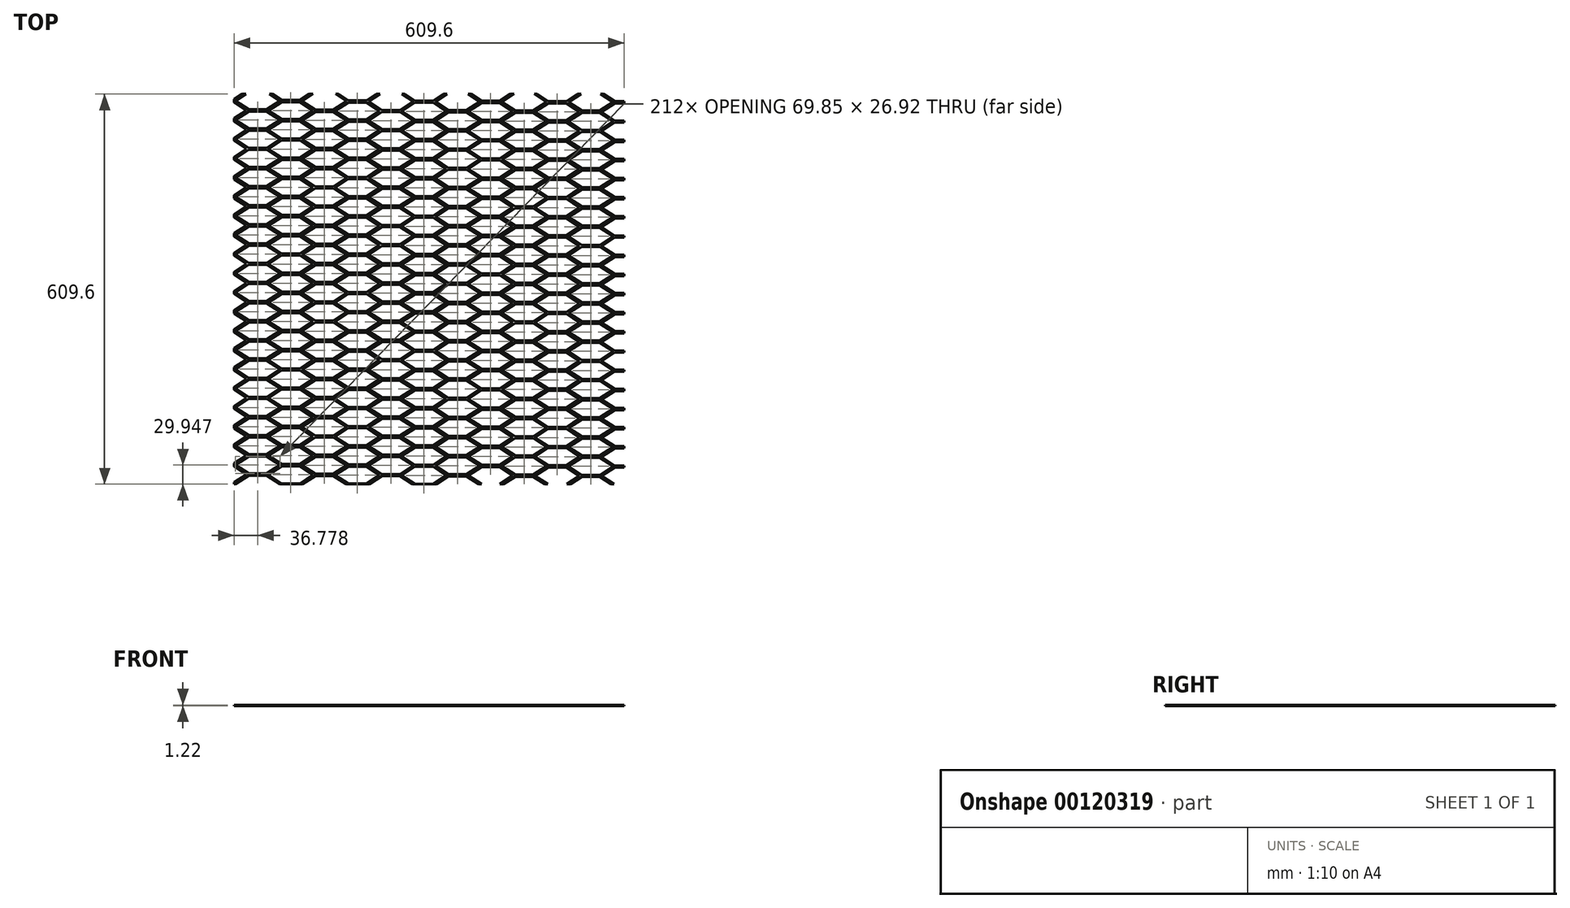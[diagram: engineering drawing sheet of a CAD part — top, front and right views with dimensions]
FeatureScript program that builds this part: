
annotation { "Feature Type Name" : "Feature", "Feature Type Description" : "" }
export const myFeature = defineFeature(function(context is Context, id is Id, definition is map)
    precondition{}
    {
        {
            var Q0;
            Q0=qCreatedBy(makeId("Top.planeOp"),FACE);
            var sketch = newSketch(context, id + "F0", { "sketchPlane" : qUnion([Q0])});
            skLineSegment(sketch, "E0", {"start": v(1.85, 0) * mm, "end": v(22.6, 13.46) * mm});
            skLineSegment(sketch, "E1", {"start": v(22.6, 13.46) * mm, "end": v(50.96, 13.46) * mm});
            skLineSegment(sketch, "E2", {"start": v(50.96, 13.46) * mm, "end": v(71.7, 0) * mm});
            skLineSegment(sketch, "E3", {"start": v(71.7, 0) * mm, "end": v(50.96, -13.46) * mm});
            skLineSegment(sketch, "E4", {"start": v(50.96, -13.46) * mm, "end": v(22.6, -13.46) * mm});
            skLineSegment(sketch, "E5", {"start": v(22.6, -13.46) * mm, "end": v(1.85, 0) * mm});
            skLineSegment(sketch, "E6.0", {"start": v(19.33, -14.95) * mm, "end": v(-1.41, -1.49) * mm});
            skLineSegment(sketch, "E7", {"start": v(-1.41, -1.49) * mm, "end": v(-29.78, -1.49) * mm});
            skLineSegment(sketch, "E8", {"start": v(-29.78, -1.49) * mm, "end": v(-50.52, -14.95) * mm});
            skLineSegment(sketch, "E9", {"start": v(-50.52, -14.95) * mm, "end": v(-29.78, -28.4) * mm});
            skLineSegment(sketch, "E10", {"start": v(-29.78, -28.4) * mm, "end": v(-1.41, -28.4) * mm});
            skLineSegment(sketch, "E11", {"start": v(-1.41, -28.4) * mm, "end": v(19.33, -14.95) * mm});
            skLineSegment(sketch, "E12.0.1.0", {"start": v(1.85, 29.95) * mm, "end": v(22.6, 43.4) * mm});
            skLineSegment(sketch, "E12.0.1.1", {"start": v(22.6, 43.4) * mm, "end": v(50.96, 43.4) * mm});
            skLineSegment(sketch, "E12.0.1.2", {"start": v(50.96, 43.4) * mm, "end": v(71.7, 29.95) * mm});
            skLineSegment(sketch, "E12.0.1.3", {"start": v(22.6, 16.48) * mm, "end": v(1.85, 29.95) * mm});
            skLineSegment(sketch, "E12.0.1.4", {"start": v(71.7, 29.95) * mm, "end": v(50.96, 16.48) * mm});
            skLineSegment(sketch, "E12.0.1.5", {"start": v(19.33, 15) * mm, "end": v(-1.41, 28.46) * mm});
            skLineSegment(sketch, "E12.0.1.6", {"start": v(50.96, 16.48) * mm, "end": v(22.6, 16.48) * mm});
            skLineSegment(sketch, "E12.0.1.7", {"start": v(-1.41, 28.46) * mm, "end": v(-29.78, 28.46) * mm});
            skLineSegment(sketch, "E12.0.1.8", {"start": v(-29.78, 28.46) * mm, "end": v(-50.52, 15) * mm});
            skLineSegment(sketch, "E12.0.1.9", {"start": v(-50.52, 15) * mm, "end": v(-29.78, 1.54) * mm});
            skLineSegment(sketch, "E12.0.1.10", {"start": v(-29.78, 1.54) * mm, "end": v(-1.41, 1.54) * mm});
            skLineSegment(sketch, "E12.0.1.11", {"start": v(-1.41, 1.54) * mm, "end": v(19.33, 15) * mm});
            skLineSegment(sketch, "E12.1.0.0", {"start": v(105.98, -0.4) * mm, "end": v(126.72, 13.06) * mm});
            skLineSegment(sketch, "E12.1.0.1", {"start": v(126.72, 13.06) * mm, "end": v(155.1, 13.06) * mm});
            skLineSegment(sketch, "E12.1.0.2", {"start": v(155.1, 13.06) * mm, "end": v(175.83, -0.4) * mm});
            skLineSegment(sketch, "E12.1.0.3", {"start": v(126.72, -13.87) * mm, "end": v(105.98, -0.4) * mm});
            skLineSegment(sketch, "E12.1.0.4", {"start": v(175.83, -0.4) * mm, "end": v(155.1, -13.87) * mm});
            skLineSegment(sketch, "E12.1.0.5", {"start": v(123.46, -15.35) * mm, "end": v(102.72, -1.89) * mm});
            skLineSegment(sketch, "E12.1.0.6", {"start": v(155.1, -13.87) * mm, "end": v(126.72, -13.87) * mm});
            skLineSegment(sketch, "E12.1.0.7", {"start": v(102.72, -1.89) * mm, "end": v(74.34, -1.89) * mm});
            skLineSegment(sketch, "E12.1.0.8", {"start": v(74.34, -1.89) * mm, "end": v(53.6, -15.35) * mm});
            skLineSegment(sketch, "E12.1.0.9", {"start": v(53.6, -15.35) * mm, "end": v(74.34, -28.81) * mm});
            skLineSegment(sketch, "E12.1.0.10", {"start": v(74.34, -28.81) * mm, "end": v(102.72, -28.81) * mm});
            skLineSegment(sketch, "E12.1.0.11", {"start": v(102.72, -28.81) * mm, "end": v(123.46, -15.35) * mm});
            skLineSegment(sketch, "E12.1.1.0", {"start": v(105.98, 29.54) * mm, "end": v(126.72, 43) * mm});
            skLineSegment(sketch, "E12.1.1.1", {"start": v(126.72, 43) * mm, "end": v(155.1, 43) * mm});
            skLineSegment(sketch, "E12.1.1.2", {"start": v(155.1, 43) * mm, "end": v(175.83, 29.54) * mm});
            skLineSegment(sketch, "E12.1.1.3", {"start": v(126.72, 16.08) * mm, "end": v(105.98, 29.54) * mm});
            skLineSegment(sketch, "E12.1.1.4", {"start": v(175.83, 29.54) * mm, "end": v(155.1, 16.08) * mm});
            skLineSegment(sketch, "E12.1.1.5", {"start": v(123.46, 14.6) * mm, "end": v(102.72, 28.06) * mm});
            skLineSegment(sketch, "E12.1.1.6", {"start": v(155.1, 16.08) * mm, "end": v(126.72, 16.08) * mm});
            skLineSegment(sketch, "E12.1.1.7", {"start": v(102.72, 28.06) * mm, "end": v(74.34, 28.06) * mm});
            skLineSegment(sketch, "E12.1.1.8", {"start": v(74.34, 28.06) * mm, "end": v(53.6, 14.6) * mm});
            skLineSegment(sketch, "E12.1.1.9", {"start": v(53.6, 14.6) * mm, "end": v(74.34, 1.13) * mm});
            skLineSegment(sketch, "E12.1.1.10", {"start": v(74.34, 1.13) * mm, "end": v(102.72, 1.13) * mm});
            skLineSegment(sketch, "E12.1.1.11", {"start": v(102.72, 1.13) * mm, "end": v(123.46, 14.6) * mm});
            skLineSegment(sketch, "E12.2.0.0", {"start": v(210.1, -0.8) * mm, "end": v(230.85, 12.66) * mm});
            skLineSegment(sketch, "E12.2.0.1", {"start": v(230.85, 12.66) * mm, "end": v(259.22, 12.66) * mm});
            skLineSegment(sketch, "E12.2.0.2", {"start": v(259.22, 12.66) * mm, "end": v(279.96, -0.8) * mm});
            skLineSegment(sketch, "E12.2.0.3", {"start": v(230.85, -14.27) * mm, "end": v(210.1, -0.8) * mm});
            skLineSegment(sketch, "E12.2.0.4", {"start": v(279.96, -0.8) * mm, "end": v(259.22, -14.27) * mm});
            skLineSegment(sketch, "E12.2.0.5", {"start": v(227.58, -15.75) * mm, "end": v(206.85, -2.3) * mm});
            skLineSegment(sketch, "E12.2.0.6", {"start": v(259.22, -14.27) * mm, "end": v(230.85, -14.27) * mm});
            skLineSegment(sketch, "E12.2.0.7", {"start": v(206.85, -2.3) * mm, "end": v(178.47, -2.3) * mm});
            skLineSegment(sketch, "E12.2.0.8", {"start": v(178.47, -2.3) * mm, "end": v(157.73, -15.75) * mm});
            skLineSegment(sketch, "E12.2.0.9", {"start": v(157.73, -15.75) * mm, "end": v(178.47, -29.22) * mm});
            skLineSegment(sketch, "E12.2.0.10", {"start": v(178.47, -29.22) * mm, "end": v(206.85, -29.22) * mm});
            skLineSegment(sketch, "E12.2.0.11", {"start": v(206.85, -29.22) * mm, "end": v(227.58, -15.75) * mm});
            skLineSegment(sketch, "E12.2.1.0", {"start": v(210.1, 29.14) * mm, "end": v(230.85, 42.6) * mm});
            skLineSegment(sketch, "E12.2.1.1", {"start": v(230.85, 42.6) * mm, "end": v(259.22, 42.6) * mm});
            skLineSegment(sketch, "E12.2.1.2", {"start": v(259.22, 42.6) * mm, "end": v(279.96, 29.14) * mm});
            skLineSegment(sketch, "E12.2.1.3", {"start": v(230.85, 15.68) * mm, "end": v(210.1, 29.14) * mm});
            skLineSegment(sketch, "E12.2.1.4", {"start": v(279.96, 29.14) * mm, "end": v(259.22, 15.68) * mm});
            skLineSegment(sketch, "E12.2.1.5", {"start": v(227.58, 14.2) * mm, "end": v(206.85, 27.65) * mm});
            skLineSegment(sketch, "E12.2.1.6", {"start": v(259.22, 15.68) * mm, "end": v(230.85, 15.68) * mm});
            skLineSegment(sketch, "E12.2.1.7", {"start": v(206.85, 27.65) * mm, "end": v(178.47, 27.65) * mm});
            skLineSegment(sketch, "E12.2.1.8", {"start": v(178.47, 27.65) * mm, "end": v(157.73, 14.2) * mm});
            skLineSegment(sketch, "E12.2.1.9", {"start": v(157.73, 14.2) * mm, "end": v(178.47, 0.73) * mm});
            skLineSegment(sketch, "E12.2.1.10", {"start": v(178.47, 0.73) * mm, "end": v(206.85, 0.73) * mm});
            skLineSegment(sketch, "E12.2.1.11", {"start": v(206.85, 0.73) * mm, "end": v(227.58, 14.2) * mm});
            skLineSegment(sketch, "E12.direction1", {"start": v(-50.52, -14.95) * mm, "end": v(53.6, -15.35) * mm, "construction": true});
            skLineSegment(sketch, "E12.direction2", {"start": v(-50.52, -14.95) * mm, "end": v(-50.52, 15) * mm, "construction": true});
            skLineSegment(sketch, "E13.0.3.0", {"start": v(314.24, -1.21) * mm, "end": v(334.98, 12.25) * mm});
            skLineSegment(sketch, "E13.3.3.0", {"start": v(334.98, 12.25) * mm, "end": v(363.35, 12.25) * mm});
            skLineSegment(sketch, "E13.6.3.0", {"start": v(363.35, 12.25) * mm, "end": v(384.09, -1.21) * mm});
            skLineSegment(sketch, "E13.9.3.0", {"start": v(334.98, -14.67) * mm, "end": v(314.24, -1.21) * mm});
            skLineSegment(sketch, "E13.12.3.0", {"start": v(384.09, -1.21) * mm, "end": v(363.35, -14.67) * mm});
            skLineSegment(sketch, "E13.15.3.0", {"start": v(331.71, -16.16) * mm, "end": v(310.97, -2.7) * mm});
            skLineSegment(sketch, "E13.18.3.0", {"start": v(363.35, -14.67) * mm, "end": v(334.98, -14.67) * mm});
            skLineSegment(sketch, "E13.21.3.0", {"start": v(310.97, -2.7) * mm, "end": v(282.6, -2.7) * mm});
            skLineSegment(sketch, "E13.24.3.0", {"start": v(282.6, -2.7) * mm, "end": v(261.86, -16.16) * mm});
            skLineSegment(sketch, "E13.27.3.0", {"start": v(261.86, -16.16) * mm, "end": v(282.6, -29.62) * mm});
            skLineSegment(sketch, "E13.30.3.0", {"start": v(282.6, -29.62) * mm, "end": v(310.97, -29.62) * mm});
            skLineSegment(sketch, "E13.33.3.0", {"start": v(310.97, -29.62) * mm, "end": v(331.71, -16.16) * mm});
            skLineSegment(sketch, "E13.0.3.1", {"start": v(314.24, 28.74) * mm, "end": v(334.98, 42.2) * mm});
            skLineSegment(sketch, "E13.3.3.1", {"start": v(334.98, 42.2) * mm, "end": v(363.35, 42.2) * mm});
            skLineSegment(sketch, "E13.6.3.1", {"start": v(363.35, 42.2) * mm, "end": v(384.09, 28.74) * mm});
            skLineSegment(sketch, "E13.9.3.1", {"start": v(334.98, 15.27) * mm, "end": v(314.24, 28.74) * mm});
            skLineSegment(sketch, "E13.12.3.1", {"start": v(384.09, 28.74) * mm, "end": v(363.35, 15.27) * mm});
            skLineSegment(sketch, "E13.15.3.1", {"start": v(331.71, 13.79) * mm, "end": v(310.97, 27.25) * mm});
            skLineSegment(sketch, "E13.18.3.1", {"start": v(363.35, 15.27) * mm, "end": v(334.98, 15.27) * mm});
            skLineSegment(sketch, "E13.21.3.1", {"start": v(310.97, 27.25) * mm, "end": v(282.6, 27.25) * mm});
            skLineSegment(sketch, "E13.24.3.1", {"start": v(282.6, 27.25) * mm, "end": v(261.86, 13.79) * mm});
            skLineSegment(sketch, "E13.27.3.1", {"start": v(261.86, 13.79) * mm, "end": v(282.6, 0.33) * mm});
            skLineSegment(sketch, "E13.30.3.1", {"start": v(282.6, 0.33) * mm, "end": v(310.97, 0.33) * mm});
            skLineSegment(sketch, "E13.33.3.1", {"start": v(310.97, 0.33) * mm, "end": v(331.71, 13.79) * mm});
            skLineSegment(sketch, "E13.0.4.0", {"start": v(418.37, -1.61) * mm, "end": v(439.1, 11.85) * mm});
            skLineSegment(sketch, "E13.3.4.0", {"start": v(439.1, 11.85) * mm, "end": v(467.48, 11.85) * mm});
            skLineSegment(sketch, "E13.6.4.0", {"start": v(467.48, 11.85) * mm, "end": v(488.22, -1.61) * mm});
            skLineSegment(sketch, "E13.9.4.0", {"start": v(439.1, -15.08) * mm, "end": v(418.37, -1.61) * mm});
            skLineSegment(sketch, "E13.12.4.0", {"start": v(488.22, -1.61) * mm, "end": v(467.48, -15.08) * mm});
            skLineSegment(sketch, "E13.15.4.0", {"start": v(435.84, -16.56) * mm, "end": v(415.1, -3.1) * mm});
            skLineSegment(sketch, "E13.18.4.0", {"start": v(467.48, -15.08) * mm, "end": v(439.1, -15.08) * mm});
            skLineSegment(sketch, "E13.21.4.0", {"start": v(415.1, -3.1) * mm, "end": v(386.73, -3.1) * mm});
            skLineSegment(sketch, "E13.24.4.0", {"start": v(386.73, -3.1) * mm, "end": v(366, -16.56) * mm});
            skLineSegment(sketch, "E13.27.4.0", {"start": v(366, -16.56) * mm, "end": v(386.73, -30.02) * mm});
            skLineSegment(sketch, "E13.30.4.0", {"start": v(386.73, -30.02) * mm, "end": v(415.1, -30.02) * mm});
            skLineSegment(sketch, "E13.33.4.0", {"start": v(415.1, -30.02) * mm, "end": v(435.84, -16.56) * mm});
            skLineSegment(sketch, "E13.0.4.1", {"start": v(418.37, 28.33) * mm, "end": v(439.1, 41.8) * mm});
            skLineSegment(sketch, "E13.3.4.1", {"start": v(439.1, 41.8) * mm, "end": v(467.48, 41.8) * mm});
            skLineSegment(sketch, "E13.6.4.1", {"start": v(467.48, 41.8) * mm, "end": v(488.22, 28.33) * mm});
            skLineSegment(sketch, "E13.9.4.1", {"start": v(439.1, 14.87) * mm, "end": v(418.37, 28.33) * mm});
            skLineSegment(sketch, "E13.12.4.1", {"start": v(488.22, 28.33) * mm, "end": v(467.48, 14.87) * mm});
            skLineSegment(sketch, "E13.15.4.1", {"start": v(435.84, 13.39) * mm, "end": v(415.1, 26.85) * mm});
            skLineSegment(sketch, "E13.18.4.1", {"start": v(467.48, 14.87) * mm, "end": v(439.1, 14.87) * mm});
            skLineSegment(sketch, "E13.21.4.1", {"start": v(415.1, 26.85) * mm, "end": v(386.73, 26.85) * mm});
            skLineSegment(sketch, "E13.24.4.1", {"start": v(386.73, 26.85) * mm, "end": v(366, 13.39) * mm});
            skLineSegment(sketch, "E13.27.4.1", {"start": v(366, 13.39) * mm, "end": v(386.73, -0.08) * mm});
            skLineSegment(sketch, "E13.30.4.1", {"start": v(386.73, -0.08) * mm, "end": v(415.1, -0.08) * mm});
            skLineSegment(sketch, "E13.33.4.1", {"start": v(415.1, -0.08) * mm, "end": v(435.84, 13.39) * mm});
            skLineSegment(sketch, "E13.0.5.0", {"start": v(522.5, -2.02) * mm, "end": v(543.23, 11.44) * mm});
            skLineSegment(sketch, "E13.3.5.0", {"start": v(543.23, 11.44) * mm, "end": v(571.6, 11.44) * mm});
            skLineSegment(sketch, "E13.6.5.0", {"start": v(571.6, 11.44) * mm, "end": v(592.34, -2.02) * mm});
            skLineSegment(sketch, "E13.9.5.0", {"start": v(543.23, -15.48) * mm, "end": v(522.5, -2.02) * mm});
            skLineSegment(sketch, "E13.12.5.0", {"start": v(592.34, -2.02) * mm, "end": v(571.6, -15.48) * mm});
            skLineSegment(sketch, "E13.15.5.0", {"start": v(539.97, -16.96) * mm, "end": v(519.23, -3.5) * mm});
            skLineSegment(sketch, "E13.18.5.0", {"start": v(571.6, -15.48) * mm, "end": v(543.23, -15.48) * mm});
            skLineSegment(sketch, "E13.21.5.0", {"start": v(519.23, -3.5) * mm, "end": v(490.86, -3.5) * mm});
            skLineSegment(sketch, "E13.24.5.0", {"start": v(490.86, -3.5) * mm, "end": v(470.12, -16.96) * mm});
            skLineSegment(sketch, "E13.27.5.0", {"start": v(470.12, -16.96) * mm, "end": v(490.86, -30.43) * mm});
            skLineSegment(sketch, "E13.30.5.0", {"start": v(490.86, -30.43) * mm, "end": v(519.23, -30.43) * mm});
            skLineSegment(sketch, "E13.33.5.0", {"start": v(519.23, -30.43) * mm, "end": v(539.97, -16.96) * mm});
            skLineSegment(sketch, "E13.0.5.1", {"start": v(522.5, 27.93) * mm, "end": v(543.23, 41.4) * mm});
            skLineSegment(sketch, "E13.3.5.1", {"start": v(543.23, 41.4) * mm, "end": v(571.6, 41.4) * mm});
            skLineSegment(sketch, "E13.6.5.1", {"start": v(571.6, 41.4) * mm, "end": v(592.34, 27.93) * mm});
            skLineSegment(sketch, "E13.9.5.1", {"start": v(543.23, 14.47) * mm, "end": v(522.5, 27.93) * mm});
            skLineSegment(sketch, "E13.12.5.1", {"start": v(592.34, 27.93) * mm, "end": v(571.6, 14.47) * mm});
            skLineSegment(sketch, "E13.15.5.1", {"start": v(539.97, 12.98) * mm, "end": v(519.23, 26.44) * mm});
            skLineSegment(sketch, "E13.18.5.1", {"start": v(571.6, 14.47) * mm, "end": v(543.23, 14.47) * mm});
            skLineSegment(sketch, "E13.21.5.1", {"start": v(519.23, 26.44) * mm, "end": v(490.86, 26.44) * mm});
            skLineSegment(sketch, "E13.24.5.1", {"start": v(490.86, 26.44) * mm, "end": v(470.12, 12.98) * mm});
            skLineSegment(sketch, "E13.27.5.1", {"start": v(470.12, 12.98) * mm, "end": v(490.86, -0.48) * mm});
            skLineSegment(sketch, "E13.30.5.1", {"start": v(490.86, -0.48) * mm, "end": v(519.23, -0.48) * mm});
            skLineSegment(sketch, "E13.33.5.1", {"start": v(519.23, -0.48) * mm, "end": v(539.97, 12.98) * mm});
            skLineSegment(sketch, "E13.0.6.0", {"start": v(626.62, -2.42) * mm, "end": v(647.36, 11.04) * mm});
            skLineSegment(sketch, "E13.3.6.0", {"start": v(647.36, 11.04) * mm, "end": v(675.73, 11.04) * mm});
            skLineSegment(sketch, "E13.6.6.0", {"start": v(675.73, 11.04) * mm, "end": v(696.47, -2.42) * mm});
            skLineSegment(sketch, "E13.9.6.0", {"start": v(647.36, -15.88) * mm, "end": v(626.62, -2.42) * mm});
            skLineSegment(sketch, "E13.12.6.0", {"start": v(696.47, -2.42) * mm, "end": v(675.73, -15.88) * mm});
            skLineSegment(sketch, "E13.15.6.0", {"start": v(644.1, -17.37) * mm, "end": v(623.36, -3.9) * mm});
            skLineSegment(sketch, "E13.18.6.0", {"start": v(675.73, -15.88) * mm, "end": v(647.36, -15.88) * mm});
            skLineSegment(sketch, "E13.21.6.0", {"start": v(623.36, -3.9) * mm, "end": v(594.99, -3.9) * mm});
            skLineSegment(sketch, "E13.24.6.0", {"start": v(594.99, -3.9) * mm, "end": v(574.25, -17.37) * mm});
            skLineSegment(sketch, "E13.27.6.0", {"start": v(574.25, -17.37) * mm, "end": v(594.99, -30.83) * mm});
            skLineSegment(sketch, "E13.30.6.0", {"start": v(594.99, -30.83) * mm, "end": v(623.36, -30.83) * mm});
            skLineSegment(sketch, "E13.33.6.0", {"start": v(623.36, -30.83) * mm, "end": v(644.1, -17.37) * mm});
            skLineSegment(sketch, "E13.0.6.1", {"start": v(626.62, 27.53) * mm, "end": v(647.36, 40.99) * mm});
            skLineSegment(sketch, "E13.3.6.1", {"start": v(647.36, 40.99) * mm, "end": v(675.73, 40.99) * mm});
            skLineSegment(sketch, "E13.6.6.1", {"start": v(675.73, 40.99) * mm, "end": v(696.47, 27.53) * mm});
            skLineSegment(sketch, "E13.9.6.1", {"start": v(647.36, 14.06) * mm, "end": v(626.62, 27.53) * mm});
            skLineSegment(sketch, "E13.12.6.1", {"start": v(696.47, 27.53) * mm, "end": v(675.73, 14.06) * mm});
            skLineSegment(sketch, "E13.15.6.1", {"start": v(644.1, 12.58) * mm, "end": v(623.36, 26.04) * mm});
            skLineSegment(sketch, "E13.18.6.1", {"start": v(675.73, 14.06) * mm, "end": v(647.36, 14.06) * mm});
            skLineSegment(sketch, "E13.21.6.1", {"start": v(623.36, 26.04) * mm, "end": v(594.99, 26.04) * mm});
            skLineSegment(sketch, "E13.24.6.1", {"start": v(594.99, 26.04) * mm, "end": v(574.25, 12.58) * mm});
            skLineSegment(sketch, "E13.27.6.1", {"start": v(574.25, 12.58) * mm, "end": v(594.99, -0.88) * mm});
            skLineSegment(sketch, "E13.30.6.1", {"start": v(594.99, -0.88) * mm, "end": v(623.36, -0.88) * mm});
            skLineSegment(sketch, "E13.33.6.1", {"start": v(623.36, -0.88) * mm, "end": v(644.1, 12.58) * mm});
            skLineSegment(sketch, "E14.0.0.2", {"start": v(1.85, 59.9) * mm, "end": v(22.6, 73.36) * mm});
            skLineSegment(sketch, "E14.3.0.2", {"start": v(22.6, 73.36) * mm, "end": v(50.96, 73.36) * mm});
            skLineSegment(sketch, "E14.6.0.2", {"start": v(50.96, 73.36) * mm, "end": v(71.7, 59.9) * mm});
            skLineSegment(sketch, "E14.9.0.2", {"start": v(22.6, 46.43) * mm, "end": v(1.85, 59.9) * mm});
            skLineSegment(sketch, "E14.12.0.2", {"start": v(71.7, 59.9) * mm, "end": v(50.96, 46.43) * mm});
            skLineSegment(sketch, "E14.15.0.2", {"start": v(19.33, 44.95) * mm, "end": v(-1.41, 58.4) * mm});
            skLineSegment(sketch, "E14.18.0.2", {"start": v(50.96, 46.43) * mm, "end": v(22.6, 46.43) * mm});
            skLineSegment(sketch, "E14.21.0.2", {"start": v(-1.41, 58.4) * mm, "end": v(-29.78, 58.4) * mm});
            skLineSegment(sketch, "E14.24.0.2", {"start": v(-29.78, 58.4) * mm, "end": v(-50.52, 44.95) * mm});
            skLineSegment(sketch, "E14.27.0.2", {"start": v(-50.52, 44.95) * mm, "end": v(-29.78, 31.48) * mm});
            skLineSegment(sketch, "E14.30.0.2", {"start": v(-29.78, 31.48) * mm, "end": v(-1.41, 31.48) * mm});
            skLineSegment(sketch, "E14.33.0.2", {"start": v(-1.41, 31.48) * mm, "end": v(19.33, 44.95) * mm});
            skLineSegment(sketch, "E14.0.0.3", {"start": v(1.85, 89.84) * mm, "end": v(22.6, 103.3) * mm});
            skLineSegment(sketch, "E14.3.0.3", {"start": v(22.6, 103.3) * mm, "end": v(50.96, 103.3) * mm});
            skLineSegment(sketch, "E14.6.0.3", {"start": v(50.96, 103.3) * mm, "end": v(71.7, 89.84) * mm});
            skLineSegment(sketch, "E14.9.0.3", {"start": v(22.6, 76.38) * mm, "end": v(1.85, 89.84) * mm});
            skLineSegment(sketch, "E14.12.0.3", {"start": v(71.7, 89.84) * mm, "end": v(50.96, 76.38) * mm});
            skLineSegment(sketch, "E14.15.0.3", {"start": v(19.33, 74.9) * mm, "end": v(-1.41, 88.35) * mm});
            skLineSegment(sketch, "E14.18.0.3", {"start": v(50.96, 76.38) * mm, "end": v(22.6, 76.38) * mm});
            skLineSegment(sketch, "E14.21.0.3", {"start": v(-1.41, 88.35) * mm, "end": v(-29.78, 88.35) * mm});
            skLineSegment(sketch, "E14.24.0.3", {"start": v(-29.78, 88.35) * mm, "end": v(-50.52, 74.9) * mm});
            skLineSegment(sketch, "E14.27.0.3", {"start": v(-50.52, 74.9) * mm, "end": v(-29.78, 61.43) * mm});
            skLineSegment(sketch, "E14.30.0.3", {"start": v(-29.78, 61.43) * mm, "end": v(-1.41, 61.43) * mm});
            skLineSegment(sketch, "E14.33.0.3", {"start": v(-1.41, 61.43) * mm, "end": v(19.33, 74.9) * mm});
            skLineSegment(sketch, "E14.0.0.4", {"start": v(1.85, 119.79) * mm, "end": v(22.6, 133.25) * mm});
            skLineSegment(sketch, "E14.3.0.4", {"start": v(22.6, 133.25) * mm, "end": v(50.96, 133.25) * mm});
            skLineSegment(sketch, "E14.6.0.4", {"start": v(50.96, 133.25) * mm, "end": v(71.7, 119.79) * mm});
            skLineSegment(sketch, "E14.9.0.4", {"start": v(22.6, 106.32) * mm, "end": v(1.85, 119.79) * mm});
            skLineSegment(sketch, "E14.12.0.4", {"start": v(71.7, 119.79) * mm, "end": v(50.96, 106.32) * mm});
            skLineSegment(sketch, "E14.15.0.4", {"start": v(19.33, 104.84) * mm, "end": v(-1.41, 118.3) * mm});
            skLineSegment(sketch, "E14.18.0.4", {"start": v(50.96, 106.32) * mm, "end": v(22.6, 106.32) * mm});
            skLineSegment(sketch, "E14.21.0.4", {"start": v(-1.41, 118.3) * mm, "end": v(-29.78, 118.3) * mm});
            skLineSegment(sketch, "E14.24.0.4", {"start": v(-29.78, 118.3) * mm, "end": v(-50.52, 104.84) * mm});
            skLineSegment(sketch, "E14.27.0.4", {"start": v(-50.52, 104.84) * mm, "end": v(-29.78, 91.38) * mm});
            skLineSegment(sketch, "E14.30.0.4", {"start": v(-29.78, 91.38) * mm, "end": v(-1.41, 91.38) * mm});
            skLineSegment(sketch, "E14.33.0.4", {"start": v(-1.41, 91.38) * mm, "end": v(19.33, 104.84) * mm});
            skLineSegment(sketch, "E14.0.0.5", {"start": v(1.85, 149.73) * mm, "end": v(22.6, 163.2) * mm});
            skLineSegment(sketch, "E14.3.0.5", {"start": v(22.6, 163.2) * mm, "end": v(50.96, 163.2) * mm});
            skLineSegment(sketch, "E14.6.0.5", {"start": v(50.96, 163.2) * mm, "end": v(71.7, 149.73) * mm});
            skLineSegment(sketch, "E14.9.0.5", {"start": v(22.6, 136.27) * mm, "end": v(1.85, 149.73) * mm});
            skLineSegment(sketch, "E14.12.0.5", {"start": v(71.7, 149.73) * mm, "end": v(50.96, 136.27) * mm});
            skLineSegment(sketch, "E14.15.0.5", {"start": v(19.33, 134.79) * mm, "end": v(-1.41, 148.25) * mm});
            skLineSegment(sketch, "E14.18.0.5", {"start": v(50.96, 136.27) * mm, "end": v(22.6, 136.27) * mm});
            skLineSegment(sketch, "E14.21.0.5", {"start": v(-1.41, 148.25) * mm, "end": v(-29.78, 148.25) * mm});
            skLineSegment(sketch, "E14.24.0.5", {"start": v(-29.78, 148.25) * mm, "end": v(-50.52, 134.79) * mm});
            skLineSegment(sketch, "E14.27.0.5", {"start": v(-50.52, 134.79) * mm, "end": v(-29.78, 121.32) * mm});
            skLineSegment(sketch, "E14.30.0.5", {"start": v(-29.78, 121.32) * mm, "end": v(-1.41, 121.32) * mm});
            skLineSegment(sketch, "E14.33.0.5", {"start": v(-1.41, 121.32) * mm, "end": v(19.33, 134.79) * mm});
            skLineSegment(sketch, "E14.0.0.6", {"start": v(1.85, 179.68) * mm, "end": v(22.6, 193.14) * mm});
            skLineSegment(sketch, "E14.3.0.6", {"start": v(22.6, 193.14) * mm, "end": v(50.96, 193.14) * mm});
            skLineSegment(sketch, "E14.6.0.6", {"start": v(50.96, 193.14) * mm, "end": v(71.7, 179.68) * mm});
            skLineSegment(sketch, "E14.9.0.6", {"start": v(22.6, 166.22) * mm, "end": v(1.85, 179.68) * mm});
            skLineSegment(sketch, "E14.12.0.6", {"start": v(71.7, 179.68) * mm, "end": v(50.96, 166.22) * mm});
            skLineSegment(sketch, "E14.15.0.6", {"start": v(19.33, 164.73) * mm, "end": v(-1.41, 178.2) * mm});
            skLineSegment(sketch, "E14.18.0.6", {"start": v(50.96, 166.22) * mm, "end": v(22.6, 166.22) * mm});
            skLineSegment(sketch, "E14.21.0.6", {"start": v(-1.41, 178.2) * mm, "end": v(-29.78, 178.2) * mm});
            skLineSegment(sketch, "E14.24.0.6", {"start": v(-29.78, 178.2) * mm, "end": v(-50.52, 164.73) * mm});
            skLineSegment(sketch, "E14.27.0.6", {"start": v(-50.52, 164.73) * mm, "end": v(-29.78, 151.27) * mm});
            skLineSegment(sketch, "E14.30.0.6", {"start": v(-29.78, 151.27) * mm, "end": v(-1.41, 151.27) * mm});
            skLineSegment(sketch, "E14.33.0.6", {"start": v(-1.41, 151.27) * mm, "end": v(19.33, 164.73) * mm});
            skLineSegment(sketch, "E14.0.0.7", {"start": v(1.85, 209.63) * mm, "end": v(22.6, 223.09) * mm});
            skLineSegment(sketch, "E14.3.0.7", {"start": v(22.6, 223.09) * mm, "end": v(50.96, 223.09) * mm});
            skLineSegment(sketch, "E14.6.0.7", {"start": v(50.96, 223.09) * mm, "end": v(71.7, 209.63) * mm});
            skLineSegment(sketch, "E14.9.0.7", {"start": v(22.6, 196.16) * mm, "end": v(1.85, 209.63) * mm});
            skLineSegment(sketch, "E14.12.0.7", {"start": v(71.7, 209.63) * mm, "end": v(50.96, 196.16) * mm});
            skLineSegment(sketch, "E14.15.0.7", {"start": v(19.33, 194.68) * mm, "end": v(-1.41, 208.14) * mm});
            skLineSegment(sketch, "E14.18.0.7", {"start": v(50.96, 196.16) * mm, "end": v(22.6, 196.16) * mm});
            skLineSegment(sketch, "E14.21.0.7", {"start": v(-1.41, 208.14) * mm, "end": v(-29.78, 208.14) * mm});
            skLineSegment(sketch, "E14.24.0.7", {"start": v(-29.78, 208.14) * mm, "end": v(-50.52, 194.68) * mm});
            skLineSegment(sketch, "E14.27.0.7", {"start": v(-50.52, 194.68) * mm, "end": v(-29.78, 181.22) * mm});
            skLineSegment(sketch, "E14.30.0.7", {"start": v(-29.78, 181.22) * mm, "end": v(-1.41, 181.22) * mm});
            skLineSegment(sketch, "E14.33.0.7", {"start": v(-1.41, 181.22) * mm, "end": v(19.33, 194.68) * mm});
            skLineSegment(sketch, "E14.0.0.8", {"start": v(1.85, 239.57) * mm, "end": v(22.6, 253.03) * mm});
            skLineSegment(sketch, "E14.3.0.8", {"start": v(22.6, 253.03) * mm, "end": v(50.96, 253.03) * mm});
            skLineSegment(sketch, "E14.6.0.8", {"start": v(50.96, 253.03) * mm, "end": v(71.7, 239.57) * mm});
            skLineSegment(sketch, "E14.9.0.8", {"start": v(22.6, 226.11) * mm, "end": v(1.85, 239.57) * mm});
            skLineSegment(sketch, "E14.12.0.8", {"start": v(71.7, 239.57) * mm, "end": v(50.96, 226.11) * mm});
            skLineSegment(sketch, "E14.15.0.8", {"start": v(19.33, 224.63) * mm, "end": v(-1.41, 238.09) * mm});
            skLineSegment(sketch, "E14.18.0.8", {"start": v(50.96, 226.11) * mm, "end": v(22.6, 226.11) * mm});
            skLineSegment(sketch, "E14.21.0.8", {"start": v(-1.41, 238.09) * mm, "end": v(-29.78, 238.09) * mm});
            skLineSegment(sketch, "E14.24.0.8", {"start": v(-29.78, 238.09) * mm, "end": v(-50.52, 224.63) * mm});
            skLineSegment(sketch, "E14.27.0.8", {"start": v(-50.52, 224.63) * mm, "end": v(-29.78, 211.16) * mm});
            skLineSegment(sketch, "E14.30.0.8", {"start": v(-29.78, 211.16) * mm, "end": v(-1.41, 211.16) * mm});
            skLineSegment(sketch, "E14.33.0.8", {"start": v(-1.41, 211.16) * mm, "end": v(19.33, 224.63) * mm});
            skLineSegment(sketch, "E14.0.0.9", {"start": v(1.85, 269.52) * mm, "end": v(22.6, 282.98) * mm});
            skLineSegment(sketch, "E14.3.0.9", {"start": v(22.6, 282.98) * mm, "end": v(50.96, 282.98) * mm});
            skLineSegment(sketch, "E14.6.0.9", {"start": v(50.96, 282.98) * mm, "end": v(71.7, 269.52) * mm});
            skLineSegment(sketch, "E14.9.0.9", {"start": v(22.6, 256.06) * mm, "end": v(1.85, 269.52) * mm});
            skLineSegment(sketch, "E14.12.0.9", {"start": v(71.7, 269.52) * mm, "end": v(50.96, 256.06) * mm});
            skLineSegment(sketch, "E14.15.0.9", {"start": v(19.33, 254.57) * mm, "end": v(-1.41, 268.03) * mm});
            skLineSegment(sketch, "E14.18.0.9", {"start": v(50.96, 256.06) * mm, "end": v(22.6, 256.06) * mm});
            skLineSegment(sketch, "E14.21.0.9", {"start": v(-1.41, 268.03) * mm, "end": v(-29.78, 268.03) * mm});
            skLineSegment(sketch, "E14.24.0.9", {"start": v(-29.78, 268.03) * mm, "end": v(-50.52, 254.57) * mm});
            skLineSegment(sketch, "E14.27.0.9", {"start": v(-50.52, 254.57) * mm, "end": v(-29.78, 241.1) * mm});
            skLineSegment(sketch, "E14.30.0.9", {"start": v(-29.78, 241.1) * mm, "end": v(-1.41, 241.1) * mm});
            skLineSegment(sketch, "E14.33.0.9", {"start": v(-1.41, 241.1) * mm, "end": v(19.33, 254.57) * mm});
            skLineSegment(sketch, "E14.0.0.10", {"start": v(1.85, 299.47) * mm, "end": v(22.6, 312.93) * mm});
            skLineSegment(sketch, "E14.3.0.10", {"start": v(22.6, 312.93) * mm, "end": v(50.96, 312.93) * mm});
            skLineSegment(sketch, "E14.6.0.10", {"start": v(50.96, 312.93) * mm, "end": v(71.7, 299.47) * mm});
            skLineSegment(sketch, "E14.9.0.10", {"start": v(22.6, 286) * mm, "end": v(1.85, 299.47) * mm});
            skLineSegment(sketch, "E14.12.0.10", {"start": v(71.7, 299.47) * mm, "end": v(50.96, 286) * mm});
            skLineSegment(sketch, "E14.15.0.10", {"start": v(19.33, 284.52) * mm, "end": v(-1.41, 297.98) * mm});
            skLineSegment(sketch, "E14.18.0.10", {"start": v(50.96, 286) * mm, "end": v(22.6, 286) * mm});
            skLineSegment(sketch, "E14.21.0.10", {"start": v(-1.41, 297.98) * mm, "end": v(-29.78, 297.98) * mm});
            skLineSegment(sketch, "E14.24.0.10", {"start": v(-29.78, 297.98) * mm, "end": v(-50.52, 284.52) * mm});
            skLineSegment(sketch, "E14.27.0.10", {"start": v(-50.52, 284.52) * mm, "end": v(-29.78, 271.06) * mm});
            skLineSegment(sketch, "E14.30.0.10", {"start": v(-29.78, 271.06) * mm, "end": v(-1.41, 271.06) * mm});
            skLineSegment(sketch, "E14.33.0.10", {"start": v(-1.41, 271.06) * mm, "end": v(19.33, 284.52) * mm});
            skLineSegment(sketch, "E14.0.0.11", {"start": v(1.85, 329.41) * mm, "end": v(22.6, 342.87) * mm});
            skLineSegment(sketch, "E14.3.0.11", {"start": v(22.6, 342.87) * mm, "end": v(50.96, 342.87) * mm});
            skLineSegment(sketch, "E14.6.0.11", {"start": v(50.96, 342.87) * mm, "end": v(71.7, 329.41) * mm});
            skLineSegment(sketch, "E14.9.0.11", {"start": v(22.6, 315.95) * mm, "end": v(1.85, 329.41) * mm});
            skLineSegment(sketch, "E14.12.0.11", {"start": v(71.7, 329.41) * mm, "end": v(50.96, 315.95) * mm});
            skLineSegment(sketch, "E14.15.0.11", {"start": v(19.33, 314.47) * mm, "end": v(-1.41, 327.93) * mm});
            skLineSegment(sketch, "E14.18.0.11", {"start": v(50.96, 315.95) * mm, "end": v(22.6, 315.95) * mm});
            skLineSegment(sketch, "E14.21.0.11", {"start": v(-1.41, 327.93) * mm, "end": v(-29.78, 327.93) * mm});
            skLineSegment(sketch, "E14.24.0.11", {"start": v(-29.78, 327.93) * mm, "end": v(-50.52, 314.47) * mm});
            skLineSegment(sketch, "E14.27.0.11", {"start": v(-50.52, 314.47) * mm, "end": v(-29.78, 301) * mm});
            skLineSegment(sketch, "E14.30.0.11", {"start": v(-29.78, 301) * mm, "end": v(-1.41, 301) * mm});
            skLineSegment(sketch, "E14.33.0.11", {"start": v(-1.41, 301) * mm, "end": v(19.33, 314.47) * mm});
            skLineSegment(sketch, "E14.0.0.12", {"start": v(1.85, 359.36) * mm, "end": v(22.6, 372.82) * mm});
            skLineSegment(sketch, "E14.3.0.12", {"start": v(22.6, 372.82) * mm, "end": v(50.96, 372.82) * mm});
            skLineSegment(sketch, "E14.6.0.12", {"start": v(50.96, 372.82) * mm, "end": v(71.7, 359.36) * mm});
            skLineSegment(sketch, "E14.9.0.12", {"start": v(22.6, 345.9) * mm, "end": v(1.85, 359.36) * mm});
            skLineSegment(sketch, "E14.12.0.12", {"start": v(71.7, 359.36) * mm, "end": v(50.96, 345.9) * mm});
            skLineSegment(sketch, "E14.15.0.12", {"start": v(19.33, 344.41) * mm, "end": v(-1.41, 357.87) * mm});
            skLineSegment(sketch, "E14.18.0.12", {"start": v(50.96, 345.9) * mm, "end": v(22.6, 345.9) * mm});
            skLineSegment(sketch, "E14.21.0.12", {"start": v(-1.41, 357.87) * mm, "end": v(-29.78, 357.87) * mm});
            skLineSegment(sketch, "E14.24.0.12", {"start": v(-29.78, 357.87) * mm, "end": v(-50.52, 344.41) * mm});
            skLineSegment(sketch, "E14.27.0.12", {"start": v(-50.52, 344.41) * mm, "end": v(-29.78, 330.95) * mm});
            skLineSegment(sketch, "E14.30.0.12", {"start": v(-29.78, 330.95) * mm, "end": v(-1.41, 330.95) * mm});
            skLineSegment(sketch, "E14.33.0.12", {"start": v(-1.41, 330.95) * mm, "end": v(19.33, 344.41) * mm});
            skLineSegment(sketch, "E14.0.0.13", {"start": v(1.85, 389.3) * mm, "end": v(22.6, 402.77) * mm});
            skLineSegment(sketch, "E14.3.0.13", {"start": v(22.6, 402.77) * mm, "end": v(50.96, 402.77) * mm});
            skLineSegment(sketch, "E14.6.0.13", {"start": v(50.96, 402.77) * mm, "end": v(71.7, 389.3) * mm});
            skLineSegment(sketch, "E14.9.0.13", {"start": v(22.6, 375.84) * mm, "end": v(1.85, 389.3) * mm});
            skLineSegment(sketch, "E14.12.0.13", {"start": v(71.7, 389.3) * mm, "end": v(50.96, 375.84) * mm});
            skLineSegment(sketch, "E14.15.0.13", {"start": v(19.33, 374.36) * mm, "end": v(-1.41, 387.82) * mm});
            skLineSegment(sketch, "E14.18.0.13", {"start": v(50.96, 375.84) * mm, "end": v(22.6, 375.84) * mm});
            skLineSegment(sketch, "E14.21.0.13", {"start": v(-1.41, 387.82) * mm, "end": v(-29.78, 387.82) * mm});
            skLineSegment(sketch, "E14.24.0.13", {"start": v(-29.78, 387.82) * mm, "end": v(-50.52, 374.36) * mm});
            skLineSegment(sketch, "E14.27.0.13", {"start": v(-50.52, 374.36) * mm, "end": v(-29.78, 360.9) * mm});
            skLineSegment(sketch, "E14.30.0.13", {"start": v(-29.78, 360.9) * mm, "end": v(-1.41, 360.9) * mm});
            skLineSegment(sketch, "E14.33.0.13", {"start": v(-1.41, 360.9) * mm, "end": v(19.33, 374.36) * mm});
            skLineSegment(sketch, "E14.0.0.14", {"start": v(1.85, 419.25) * mm, "end": v(22.6, 432.71) * mm});
            skLineSegment(sketch, "E14.3.0.14", {"start": v(22.6, 432.71) * mm, "end": v(50.96, 432.71) * mm});
            skLineSegment(sketch, "E14.6.0.14", {"start": v(50.96, 432.71) * mm, "end": v(71.7, 419.25) * mm});
            skLineSegment(sketch, "E14.9.0.14", {"start": v(22.6, 405.8) * mm, "end": v(1.85, 419.25) * mm});
            skLineSegment(sketch, "E14.12.0.14", {"start": v(71.7, 419.25) * mm, "end": v(50.96, 405.8) * mm});
            skLineSegment(sketch, "E14.15.0.14", {"start": v(19.33, 404.3) * mm, "end": v(-1.41, 417.77) * mm});
            skLineSegment(sketch, "E14.18.0.14", {"start": v(50.96, 405.8) * mm, "end": v(22.6, 405.8) * mm});
            skLineSegment(sketch, "E14.21.0.14", {"start": v(-1.41, 417.77) * mm, "end": v(-29.78, 417.77) * mm});
            skLineSegment(sketch, "E14.24.0.14", {"start": v(-29.78, 417.77) * mm, "end": v(-50.52, 404.3) * mm});
            skLineSegment(sketch, "E14.27.0.14", {"start": v(-50.52, 404.3) * mm, "end": v(-29.78, 390.84) * mm});
            skLineSegment(sketch, "E14.30.0.14", {"start": v(-29.78, 390.84) * mm, "end": v(-1.41, 390.84) * mm});
            skLineSegment(sketch, "E14.33.0.14", {"start": v(-1.41, 390.84) * mm, "end": v(19.33, 404.3) * mm});
            skLineSegment(sketch, "E14.0.0.15", {"start": v(1.85, 449.2) * mm, "end": v(22.6, 462.66) * mm});
            skLineSegment(sketch, "E14.3.0.15", {"start": v(22.6, 462.66) * mm, "end": v(50.96, 462.66) * mm});
            skLineSegment(sketch, "E14.6.0.15", {"start": v(50.96, 462.66) * mm, "end": v(71.7, 449.2) * mm});
            skLineSegment(sketch, "E14.9.0.15", {"start": v(22.6, 435.74) * mm, "end": v(1.85, 449.2) * mm});
            skLineSegment(sketch, "E14.12.0.15", {"start": v(71.7, 449.2) * mm, "end": v(50.96, 435.74) * mm});
            skLineSegment(sketch, "E14.15.0.15", {"start": v(19.33, 434.25) * mm, "end": v(-1.41, 447.71) * mm});
            skLineSegment(sketch, "E14.18.0.15", {"start": v(50.96, 435.74) * mm, "end": v(22.6, 435.74) * mm});
            skLineSegment(sketch, "E14.21.0.15", {"start": v(-1.41, 447.71) * mm, "end": v(-29.78, 447.71) * mm});
            skLineSegment(sketch, "E14.24.0.15", {"start": v(-29.78, 447.71) * mm, "end": v(-50.52, 434.25) * mm});
            skLineSegment(sketch, "E14.27.0.15", {"start": v(-50.52, 434.25) * mm, "end": v(-29.78, 420.79) * mm});
            skLineSegment(sketch, "E14.30.0.15", {"start": v(-29.78, 420.79) * mm, "end": v(-1.41, 420.79) * mm});
            skLineSegment(sketch, "E14.33.0.15", {"start": v(-1.41, 420.79) * mm, "end": v(19.33, 434.25) * mm});
            skLineSegment(sketch, "E14.0.0.16", {"start": v(1.85, 479.15) * mm, "end": v(22.6, 492.6) * mm});
            skLineSegment(sketch, "E14.3.0.16", {"start": v(22.6, 492.6) * mm, "end": v(50.96, 492.6) * mm});
            skLineSegment(sketch, "E14.6.0.16", {"start": v(50.96, 492.6) * mm, "end": v(71.7, 479.15) * mm});
            skLineSegment(sketch, "E14.9.0.16", {"start": v(22.6, 465.68) * mm, "end": v(1.85, 479.15) * mm});
            skLineSegment(sketch, "E14.12.0.16", {"start": v(71.7, 479.15) * mm, "end": v(50.96, 465.68) * mm});
            skLineSegment(sketch, "E14.15.0.16", {"start": v(19.33, 464.2) * mm, "end": v(-1.41, 477.66) * mm});
            skLineSegment(sketch, "E14.18.0.16", {"start": v(50.96, 465.68) * mm, "end": v(22.6, 465.68) * mm});
            skLineSegment(sketch, "E14.21.0.16", {"start": v(-1.41, 477.66) * mm, "end": v(-29.78, 477.66) * mm});
            skLineSegment(sketch, "E14.24.0.16", {"start": v(-29.78, 477.66) * mm, "end": v(-50.52, 464.2) * mm});
            skLineSegment(sketch, "E14.27.0.16", {"start": v(-50.52, 464.2) * mm, "end": v(-29.78, 450.74) * mm});
            skLineSegment(sketch, "E14.30.0.16", {"start": v(-29.78, 450.74) * mm, "end": v(-1.41, 450.74) * mm});
            skLineSegment(sketch, "E14.33.0.16", {"start": v(-1.41, 450.74) * mm, "end": v(19.33, 464.2) * mm});
            skLineSegment(sketch, "E14.0.1.2", {"start": v(105.98, 59.49) * mm, "end": v(126.72, 72.95) * mm});
            skLineSegment(sketch, "E14.3.1.2", {"start": v(126.72, 72.95) * mm, "end": v(155.1, 72.95) * mm});
            skLineSegment(sketch, "E14.6.1.2", {"start": v(155.1, 72.95) * mm, "end": v(175.83, 59.49) * mm});
            skLineSegment(sketch, "E14.9.1.2", {"start": v(126.72, 46.03) * mm, "end": v(105.98, 59.49) * mm});
            skLineSegment(sketch, "E14.12.1.2", {"start": v(175.83, 59.49) * mm, "end": v(155.1, 46.03) * mm});
            skLineSegment(sketch, "E14.15.1.2", {"start": v(123.46, 44.54) * mm, "end": v(102.72, 58) * mm});
            skLineSegment(sketch, "E14.18.1.2", {"start": v(155.1, 46.03) * mm, "end": v(126.72, 46.03) * mm});
            skLineSegment(sketch, "E14.21.1.2", {"start": v(102.72, 58) * mm, "end": v(74.34, 58) * mm});
            skLineSegment(sketch, "E14.24.1.2", {"start": v(74.34, 58) * mm, "end": v(53.6, 44.54) * mm});
            skLineSegment(sketch, "E14.27.1.2", {"start": v(53.6, 44.54) * mm, "end": v(74.34, 31.08) * mm});
            skLineSegment(sketch, "E14.30.1.2", {"start": v(74.34, 31.08) * mm, "end": v(102.72, 31.08) * mm});
            skLineSegment(sketch, "E14.33.1.2", {"start": v(102.72, 31.08) * mm, "end": v(123.46, 44.54) * mm});
            skLineSegment(sketch, "E14.0.1.3", {"start": v(105.98, 89.44) * mm, "end": v(126.72, 102.9) * mm});
            skLineSegment(sketch, "E14.3.1.3", {"start": v(126.72, 102.9) * mm, "end": v(155.1, 102.9) * mm});
            skLineSegment(sketch, "E14.6.1.3", {"start": v(155.1, 102.9) * mm, "end": v(175.83, 89.44) * mm});
            skLineSegment(sketch, "E14.9.1.3", {"start": v(126.72, 75.97) * mm, "end": v(105.98, 89.44) * mm});
            skLineSegment(sketch, "E14.12.1.3", {"start": v(175.83, 89.44) * mm, "end": v(155.1, 75.97) * mm});
            skLineSegment(sketch, "E14.15.1.3", {"start": v(123.46, 74.49) * mm, "end": v(102.72, 87.95) * mm});
            skLineSegment(sketch, "E14.18.1.3", {"start": v(155.1, 75.97) * mm, "end": v(126.72, 75.97) * mm});
            skLineSegment(sketch, "E14.21.1.3", {"start": v(102.72, 87.95) * mm, "end": v(74.34, 87.95) * mm});
            skLineSegment(sketch, "E14.24.1.3", {"start": v(74.34, 87.95) * mm, "end": v(53.6, 74.49) * mm});
            skLineSegment(sketch, "E14.27.1.3", {"start": v(53.6, 74.49) * mm, "end": v(74.34, 61.03) * mm});
            skLineSegment(sketch, "E14.30.1.3", {"start": v(74.34, 61.03) * mm, "end": v(102.72, 61.03) * mm});
            skLineSegment(sketch, "E14.33.1.3", {"start": v(102.72, 61.03) * mm, "end": v(123.46, 74.49) * mm});
            skLineSegment(sketch, "E14.0.1.4", {"start": v(105.98, 119.38) * mm, "end": v(126.72, 132.84) * mm});
            skLineSegment(sketch, "E14.3.1.4", {"start": v(126.72, 132.84) * mm, "end": v(155.1, 132.84) * mm});
            skLineSegment(sketch, "E14.6.1.4", {"start": v(155.1, 132.84) * mm, "end": v(175.83, 119.38) * mm});
            skLineSegment(sketch, "E14.9.1.4", {"start": v(126.72, 105.92) * mm, "end": v(105.98, 119.38) * mm});
            skLineSegment(sketch, "E14.12.1.4", {"start": v(175.83, 119.38) * mm, "end": v(155.1, 105.92) * mm});
            skLineSegment(sketch, "E14.15.1.4", {"start": v(123.46, 104.44) * mm, "end": v(102.72, 117.9) * mm});
            skLineSegment(sketch, "E14.18.1.4", {"start": v(155.1, 105.92) * mm, "end": v(126.72, 105.92) * mm});
            skLineSegment(sketch, "E14.21.1.4", {"start": v(102.72, 117.9) * mm, "end": v(74.34, 117.9) * mm});
            skLineSegment(sketch, "E14.24.1.4", {"start": v(74.34, 117.9) * mm, "end": v(53.6, 104.44) * mm});
            skLineSegment(sketch, "E14.27.1.4", {"start": v(53.6, 104.44) * mm, "end": v(74.34, 90.97) * mm});
            skLineSegment(sketch, "E14.30.1.4", {"start": v(74.34, 90.97) * mm, "end": v(102.72, 90.97) * mm});
            skLineSegment(sketch, "E14.33.1.4", {"start": v(102.72, 90.97) * mm, "end": v(123.46, 104.44) * mm});
            skLineSegment(sketch, "E14.0.1.5", {"start": v(105.98, 149.33) * mm, "end": v(126.72, 162.8) * mm});
            skLineSegment(sketch, "E14.3.1.5", {"start": v(126.72, 162.8) * mm, "end": v(155.1, 162.8) * mm});
            skLineSegment(sketch, "E14.6.1.5", {"start": v(155.1, 162.8) * mm, "end": v(175.83, 149.33) * mm});
            skLineSegment(sketch, "E14.9.1.5", {"start": v(126.72, 135.87) * mm, "end": v(105.98, 149.33) * mm});
            skLineSegment(sketch, "E14.12.1.5", {"start": v(175.83, 149.33) * mm, "end": v(155.1, 135.87) * mm});
            skLineSegment(sketch, "E14.15.1.5", {"start": v(123.46, 134.38) * mm, "end": v(102.72, 147.84) * mm});
            skLineSegment(sketch, "E14.18.1.5", {"start": v(155.1, 135.87) * mm, "end": v(126.72, 135.87) * mm});
            skLineSegment(sketch, "E14.21.1.5", {"start": v(102.72, 147.84) * mm, "end": v(74.34, 147.84) * mm});
            skLineSegment(sketch, "E14.24.1.5", {"start": v(74.34, 147.84) * mm, "end": v(53.6, 134.38) * mm});
            skLineSegment(sketch, "E14.27.1.5", {"start": v(53.6, 134.38) * mm, "end": v(74.34, 120.92) * mm});
            skLineSegment(sketch, "E14.30.1.5", {"start": v(74.34, 120.92) * mm, "end": v(102.72, 120.92) * mm});
            skLineSegment(sketch, "E14.33.1.5", {"start": v(102.72, 120.92) * mm, "end": v(123.46, 134.38) * mm});
            skLineSegment(sketch, "E14.0.1.6", {"start": v(105.98, 179.28) * mm, "end": v(126.72, 192.74) * mm});
            skLineSegment(sketch, "E14.3.1.6", {"start": v(126.72, 192.74) * mm, "end": v(155.1, 192.74) * mm});
            skLineSegment(sketch, "E14.6.1.6", {"start": v(155.1, 192.74) * mm, "end": v(175.83, 179.28) * mm});
            skLineSegment(sketch, "E14.9.1.6", {"start": v(126.72, 165.81) * mm, "end": v(105.98, 179.28) * mm});
            skLineSegment(sketch, "E14.12.1.6", {"start": v(175.83, 179.28) * mm, "end": v(155.1, 165.81) * mm});
            skLineSegment(sketch, "E14.15.1.6", {"start": v(123.46, 164.33) * mm, "end": v(102.72, 177.8) * mm});
            skLineSegment(sketch, "E14.18.1.6", {"start": v(155.1, 165.81) * mm, "end": v(126.72, 165.81) * mm});
            skLineSegment(sketch, "E14.21.1.6", {"start": v(102.72, 177.8) * mm, "end": v(74.34, 177.8) * mm});
            skLineSegment(sketch, "E14.24.1.6", {"start": v(74.34, 177.8) * mm, "end": v(53.6, 164.33) * mm});
            skLineSegment(sketch, "E14.27.1.6", {"start": v(53.6, 164.33) * mm, "end": v(74.34, 150.87) * mm});
            skLineSegment(sketch, "E14.30.1.6", {"start": v(74.34, 150.87) * mm, "end": v(102.72, 150.87) * mm});
            skLineSegment(sketch, "E14.33.1.6", {"start": v(102.72, 150.87) * mm, "end": v(123.46, 164.33) * mm});
            skLineSegment(sketch, "E14.0.1.7", {"start": v(105.98, 209.22) * mm, "end": v(126.72, 222.68) * mm});
            skLineSegment(sketch, "E14.3.1.7", {"start": v(126.72, 222.68) * mm, "end": v(155.1, 222.68) * mm});
            skLineSegment(sketch, "E14.6.1.7", {"start": v(155.1, 222.68) * mm, "end": v(175.83, 209.22) * mm});
            skLineSegment(sketch, "E14.9.1.7", {"start": v(126.72, 195.76) * mm, "end": v(105.98, 209.22) * mm});
            skLineSegment(sketch, "E14.12.1.7", {"start": v(175.83, 209.22) * mm, "end": v(155.1, 195.76) * mm});
            skLineSegment(sketch, "E14.15.1.7", {"start": v(123.46, 194.28) * mm, "end": v(102.72, 207.74) * mm});
            skLineSegment(sketch, "E14.18.1.7", {"start": v(155.1, 195.76) * mm, "end": v(126.72, 195.76) * mm});
            skLineSegment(sketch, "E14.21.1.7", {"start": v(102.72, 207.74) * mm, "end": v(74.34, 207.74) * mm});
            skLineSegment(sketch, "E14.24.1.7", {"start": v(74.34, 207.74) * mm, "end": v(53.6, 194.28) * mm});
            skLineSegment(sketch, "E14.27.1.7", {"start": v(53.6, 194.28) * mm, "end": v(74.34, 180.81) * mm});
            skLineSegment(sketch, "E14.30.1.7", {"start": v(74.34, 180.81) * mm, "end": v(102.72, 180.81) * mm});
            skLineSegment(sketch, "E14.33.1.7", {"start": v(102.72, 180.81) * mm, "end": v(123.46, 194.28) * mm});
            skLineSegment(sketch, "E14.0.1.8", {"start": v(105.98, 239.17) * mm, "end": v(126.72, 252.63) * mm});
            skLineSegment(sketch, "E14.3.1.8", {"start": v(126.72, 252.63) * mm, "end": v(155.1, 252.63) * mm});
            skLineSegment(sketch, "E14.6.1.8", {"start": v(155.1, 252.63) * mm, "end": v(175.83, 239.17) * mm});
            skLineSegment(sketch, "E14.9.1.8", {"start": v(126.72, 225.7) * mm, "end": v(105.98, 239.17) * mm});
            skLineSegment(sketch, "E14.12.1.8", {"start": v(175.83, 239.17) * mm, "end": v(155.1, 225.7) * mm});
            skLineSegment(sketch, "E14.15.1.8", {"start": v(123.46, 224.22) * mm, "end": v(102.72, 237.68) * mm});
            skLineSegment(sketch, "E14.18.1.8", {"start": v(155.1, 225.7) * mm, "end": v(126.72, 225.7) * mm});
            skLineSegment(sketch, "E14.21.1.8", {"start": v(102.72, 237.68) * mm, "end": v(74.34, 237.68) * mm});
            skLineSegment(sketch, "E14.24.1.8", {"start": v(74.34, 237.68) * mm, "end": v(53.6, 224.22) * mm});
            skLineSegment(sketch, "E14.27.1.8", {"start": v(53.6, 224.22) * mm, "end": v(74.34, 210.76) * mm});
            skLineSegment(sketch, "E14.30.1.8", {"start": v(74.34, 210.76) * mm, "end": v(102.72, 210.76) * mm});
            skLineSegment(sketch, "E14.33.1.8", {"start": v(102.72, 210.76) * mm, "end": v(123.46, 224.22) * mm});
            skLineSegment(sketch, "E14.0.1.9", {"start": v(105.98, 269.12) * mm, "end": v(126.72, 282.58) * mm});
            skLineSegment(sketch, "E14.3.1.9", {"start": v(126.72, 282.58) * mm, "end": v(155.1, 282.58) * mm});
            skLineSegment(sketch, "E14.6.1.9", {"start": v(155.1, 282.58) * mm, "end": v(175.83, 269.12) * mm});
            skLineSegment(sketch, "E14.9.1.9", {"start": v(126.72, 255.65) * mm, "end": v(105.98, 269.12) * mm});
            skLineSegment(sketch, "E14.12.1.9", {"start": v(175.83, 269.12) * mm, "end": v(155.1, 255.65) * mm});
            skLineSegment(sketch, "E14.15.1.9", {"start": v(123.46, 254.17) * mm, "end": v(102.72, 267.63) * mm});
            skLineSegment(sketch, "E14.18.1.9", {"start": v(155.1, 255.65) * mm, "end": v(126.72, 255.65) * mm});
            skLineSegment(sketch, "E14.21.1.9", {"start": v(102.72, 267.63) * mm, "end": v(74.34, 267.63) * mm});
            skLineSegment(sketch, "E14.24.1.9", {"start": v(74.34, 267.63) * mm, "end": v(53.6, 254.17) * mm});
            skLineSegment(sketch, "E14.27.1.9", {"start": v(53.6, 254.17) * mm, "end": v(74.34, 240.7) * mm});
            skLineSegment(sketch, "E14.30.1.9", {"start": v(74.34, 240.7) * mm, "end": v(102.72, 240.7) * mm});
            skLineSegment(sketch, "E14.33.1.9", {"start": v(102.72, 240.7) * mm, "end": v(123.46, 254.17) * mm});
            skLineSegment(sketch, "E14.0.1.10", {"start": v(105.98, 299.06) * mm, "end": v(126.72, 312.52) * mm});
            skLineSegment(sketch, "E14.3.1.10", {"start": v(126.72, 312.52) * mm, "end": v(155.1, 312.52) * mm});
            skLineSegment(sketch, "E14.6.1.10", {"start": v(155.1, 312.52) * mm, "end": v(175.83, 299.06) * mm});
            skLineSegment(sketch, "E14.9.1.10", {"start": v(126.72, 285.6) * mm, "end": v(105.98, 299.06) * mm});
            skLineSegment(sketch, "E14.12.1.10", {"start": v(175.83, 299.06) * mm, "end": v(155.1, 285.6) * mm});
            skLineSegment(sketch, "E14.15.1.10", {"start": v(123.46, 284.12) * mm, "end": v(102.72, 297.58) * mm});
            skLineSegment(sketch, "E14.18.1.10", {"start": v(155.1, 285.6) * mm, "end": v(126.72, 285.6) * mm});
            skLineSegment(sketch, "E14.21.1.10", {"start": v(102.72, 297.58) * mm, "end": v(74.34, 297.58) * mm});
            skLineSegment(sketch, "E14.24.1.10", {"start": v(74.34, 297.58) * mm, "end": v(53.6, 284.12) * mm});
            skLineSegment(sketch, "E14.27.1.10", {"start": v(53.6, 284.12) * mm, "end": v(74.34, 270.65) * mm});
            skLineSegment(sketch, "E14.30.1.10", {"start": v(74.34, 270.65) * mm, "end": v(102.72, 270.65) * mm});
            skLineSegment(sketch, "E14.33.1.10", {"start": v(102.72, 270.65) * mm, "end": v(123.46, 284.12) * mm});
            skLineSegment(sketch, "E14.0.1.11", {"start": v(105.98, 329) * mm, "end": v(126.72, 342.47) * mm});
            skLineSegment(sketch, "E14.3.1.11", {"start": v(126.72, 342.47) * mm, "end": v(155.1, 342.47) * mm});
            skLineSegment(sketch, "E14.6.1.11", {"start": v(155.1, 342.47) * mm, "end": v(175.83, 329) * mm});
            skLineSegment(sketch, "E14.9.1.11", {"start": v(126.72, 315.55) * mm, "end": v(105.98, 329) * mm});
            skLineSegment(sketch, "E14.12.1.11", {"start": v(175.83, 329) * mm, "end": v(155.1, 315.55) * mm});
            skLineSegment(sketch, "E14.15.1.11", {"start": v(123.46, 314.06) * mm, "end": v(102.72, 327.52) * mm});
            skLineSegment(sketch, "E14.18.1.11", {"start": v(155.1, 315.55) * mm, "end": v(126.72, 315.55) * mm});
            skLineSegment(sketch, "E14.21.1.11", {"start": v(102.72, 327.52) * mm, "end": v(74.34, 327.52) * mm});
            skLineSegment(sketch, "E14.24.1.11", {"start": v(74.34, 327.52) * mm, "end": v(53.6, 314.06) * mm});
            skLineSegment(sketch, "E14.27.1.11", {"start": v(53.6, 314.06) * mm, "end": v(74.34, 300.6) * mm});
            skLineSegment(sketch, "E14.30.1.11", {"start": v(74.34, 300.6) * mm, "end": v(102.72, 300.6) * mm});
            skLineSegment(sketch, "E14.33.1.11", {"start": v(102.72, 300.6) * mm, "end": v(123.46, 314.06) * mm});
            skLineSegment(sketch, "E14.0.1.12", {"start": v(105.98, 358.96) * mm, "end": v(126.72, 372.42) * mm});
            skLineSegment(sketch, "E14.3.1.12", {"start": v(126.72, 372.42) * mm, "end": v(155.1, 372.42) * mm});
            skLineSegment(sketch, "E14.6.1.12", {"start": v(155.1, 372.42) * mm, "end": v(175.83, 358.96) * mm});
            skLineSegment(sketch, "E14.9.1.12", {"start": v(126.72, 345.5) * mm, "end": v(105.98, 358.96) * mm});
            skLineSegment(sketch, "E14.12.1.12", {"start": v(175.83, 358.96) * mm, "end": v(155.1, 345.5) * mm});
            skLineSegment(sketch, "E14.15.1.12", {"start": v(123.46, 344) * mm, "end": v(102.72, 357.47) * mm});
            skLineSegment(sketch, "E14.18.1.12", {"start": v(155.1, 345.5) * mm, "end": v(126.72, 345.5) * mm});
            skLineSegment(sketch, "E14.21.1.12", {"start": v(102.72, 357.47) * mm, "end": v(74.34, 357.47) * mm});
            skLineSegment(sketch, "E14.24.1.12", {"start": v(74.34, 357.47) * mm, "end": v(53.6, 344) * mm});
            skLineSegment(sketch, "E14.27.1.12", {"start": v(53.6, 344) * mm, "end": v(74.34, 330.55) * mm});
            skLineSegment(sketch, "E14.30.1.12", {"start": v(74.34, 330.55) * mm, "end": v(102.72, 330.55) * mm});
            skLineSegment(sketch, "E14.33.1.12", {"start": v(102.72, 330.55) * mm, "end": v(123.46, 344) * mm});
            skLineSegment(sketch, "E14.0.1.13", {"start": v(105.98, 388.9) * mm, "end": v(126.72, 402.36) * mm});
            skLineSegment(sketch, "E14.3.1.13", {"start": v(126.72, 402.36) * mm, "end": v(155.1, 402.36) * mm});
            skLineSegment(sketch, "E14.6.1.13", {"start": v(155.1, 402.36) * mm, "end": v(175.83, 388.9) * mm});
            skLineSegment(sketch, "E14.9.1.13", {"start": v(126.72, 375.44) * mm, "end": v(105.98, 388.9) * mm});
            skLineSegment(sketch, "E14.12.1.13", {"start": v(175.83, 388.9) * mm, "end": v(155.1, 375.44) * mm});
            skLineSegment(sketch, "E14.15.1.13", {"start": v(123.46, 373.95) * mm, "end": v(102.72, 387.42) * mm});
            skLineSegment(sketch, "E14.18.1.13", {"start": v(155.1, 375.44) * mm, "end": v(126.72, 375.44) * mm});
            skLineSegment(sketch, "E14.21.1.13", {"start": v(102.72, 387.42) * mm, "end": v(74.34, 387.42) * mm});
            skLineSegment(sketch, "E14.24.1.13", {"start": v(74.34, 387.42) * mm, "end": v(53.6, 373.95) * mm});
            skLineSegment(sketch, "E14.27.1.13", {"start": v(53.6, 373.95) * mm, "end": v(74.34, 360.5) * mm});
            skLineSegment(sketch, "E14.30.1.13", {"start": v(74.34, 360.5) * mm, "end": v(102.72, 360.5) * mm});
            skLineSegment(sketch, "E14.33.1.13", {"start": v(102.72, 360.5) * mm, "end": v(123.46, 373.95) * mm});
            skLineSegment(sketch, "E14.0.1.14", {"start": v(105.98, 418.85) * mm, "end": v(126.72, 432.31) * mm});
            skLineSegment(sketch, "E14.3.1.14", {"start": v(126.72, 432.31) * mm, "end": v(155.1, 432.31) * mm});
            skLineSegment(sketch, "E14.6.1.14", {"start": v(155.1, 432.31) * mm, "end": v(175.83, 418.85) * mm});
            skLineSegment(sketch, "E14.9.1.14", {"start": v(126.72, 405.39) * mm, "end": v(105.98, 418.85) * mm});
            skLineSegment(sketch, "E14.12.1.14", {"start": v(175.83, 418.85) * mm, "end": v(155.1, 405.39) * mm});
            skLineSegment(sketch, "E14.15.1.14", {"start": v(123.46, 403.9) * mm, "end": v(102.72, 417.36) * mm});
            skLineSegment(sketch, "E14.18.1.14", {"start": v(155.1, 405.39) * mm, "end": v(126.72, 405.39) * mm});
            skLineSegment(sketch, "E14.21.1.14", {"start": v(102.72, 417.36) * mm, "end": v(74.34, 417.36) * mm});
            skLineSegment(sketch, "E14.24.1.14", {"start": v(74.34, 417.36) * mm, "end": v(53.6, 403.9) * mm});
            skLineSegment(sketch, "E14.27.1.14", {"start": v(53.6, 403.9) * mm, "end": v(74.34, 390.44) * mm});
            skLineSegment(sketch, "E14.30.1.14", {"start": v(74.34, 390.44) * mm, "end": v(102.72, 390.44) * mm});
            skLineSegment(sketch, "E14.33.1.14", {"start": v(102.72, 390.44) * mm, "end": v(123.46, 403.9) * mm});
            skLineSegment(sketch, "E14.0.1.15", {"start": v(105.98, 448.8) * mm, "end": v(126.72, 462.26) * mm});
            skLineSegment(sketch, "E14.3.1.15", {"start": v(126.72, 462.26) * mm, "end": v(155.1, 462.26) * mm});
            skLineSegment(sketch, "E14.6.1.15", {"start": v(155.1, 462.26) * mm, "end": v(175.83, 448.8) * mm});
            skLineSegment(sketch, "E14.9.1.15", {"start": v(126.72, 435.33) * mm, "end": v(105.98, 448.8) * mm});
            skLineSegment(sketch, "E14.12.1.15", {"start": v(175.83, 448.8) * mm, "end": v(155.1, 435.33) * mm});
            skLineSegment(sketch, "E14.15.1.15", {"start": v(123.46, 433.85) * mm, "end": v(102.72, 447.31) * mm});
            skLineSegment(sketch, "E14.18.1.15", {"start": v(155.1, 435.33) * mm, "end": v(126.72, 435.33) * mm});
            skLineSegment(sketch, "E14.21.1.15", {"start": v(102.72, 447.31) * mm, "end": v(74.34, 447.31) * mm});
            skLineSegment(sketch, "E14.24.1.15", {"start": v(74.34, 447.31) * mm, "end": v(53.6, 433.85) * mm});
            skLineSegment(sketch, "E14.27.1.15", {"start": v(53.6, 433.85) * mm, "end": v(74.34, 420.39) * mm});
            skLineSegment(sketch, "E14.30.1.15", {"start": v(74.34, 420.39) * mm, "end": v(102.72, 420.39) * mm});
            skLineSegment(sketch, "E14.33.1.15", {"start": v(102.72, 420.39) * mm, "end": v(123.46, 433.85) * mm});
            skLineSegment(sketch, "E14.0.1.16", {"start": v(105.98, 478.74) * mm, "end": v(126.72, 492.2) * mm});
            skLineSegment(sketch, "E14.3.1.16", {"start": v(126.72, 492.2) * mm, "end": v(155.1, 492.2) * mm});
            skLineSegment(sketch, "E14.6.1.16", {"start": v(155.1, 492.2) * mm, "end": v(175.83, 478.74) * mm});
            skLineSegment(sketch, "E14.9.1.16", {"start": v(126.72, 465.28) * mm, "end": v(105.98, 478.74) * mm});
            skLineSegment(sketch, "E14.12.1.16", {"start": v(175.83, 478.74) * mm, "end": v(155.1, 465.28) * mm});
            skLineSegment(sketch, "E14.15.1.16", {"start": v(123.46, 463.8) * mm, "end": v(102.72, 477.26) * mm});
            skLineSegment(sketch, "E14.18.1.16", {"start": v(155.1, 465.28) * mm, "end": v(126.72, 465.28) * mm});
            skLineSegment(sketch, "E14.21.1.16", {"start": v(102.72, 477.26) * mm, "end": v(74.34, 477.26) * mm});
            skLineSegment(sketch, "E14.24.1.16", {"start": v(74.34, 477.26) * mm, "end": v(53.6, 463.8) * mm});
            skLineSegment(sketch, "E14.27.1.16", {"start": v(53.6, 463.8) * mm, "end": v(74.34, 450.33) * mm});
            skLineSegment(sketch, "E14.30.1.16", {"start": v(74.34, 450.33) * mm, "end": v(102.72, 450.33) * mm});
            skLineSegment(sketch, "E14.33.1.16", {"start": v(102.72, 450.33) * mm, "end": v(123.46, 463.8) * mm});
            skLineSegment(sketch, "E14.0.2.2", {"start": v(210.1, 59.09) * mm, "end": v(230.85, 72.55) * mm});
            skLineSegment(sketch, "E14.3.2.2", {"start": v(230.85, 72.55) * mm, "end": v(259.22, 72.55) * mm});
            skLineSegment(sketch, "E14.6.2.2", {"start": v(259.22, 72.55) * mm, "end": v(279.96, 59.09) * mm});
            skLineSegment(sketch, "E14.9.2.2", {"start": v(230.85, 45.62) * mm, "end": v(210.1, 59.09) * mm});
            skLineSegment(sketch, "E14.12.2.2", {"start": v(279.96, 59.09) * mm, "end": v(259.22, 45.62) * mm});
            skLineSegment(sketch, "E14.15.2.2", {"start": v(227.58, 44.14) * mm, "end": v(206.85, 57.6) * mm});
            skLineSegment(sketch, "E14.18.2.2", {"start": v(259.22, 45.62) * mm, "end": v(230.85, 45.62) * mm});
            skLineSegment(sketch, "E14.21.2.2", {"start": v(206.85, 57.6) * mm, "end": v(178.47, 57.6) * mm});
            skLineSegment(sketch, "E14.24.2.2", {"start": v(178.47, 57.6) * mm, "end": v(157.73, 44.14) * mm});
            skLineSegment(sketch, "E14.27.2.2", {"start": v(157.73, 44.14) * mm, "end": v(178.47, 30.68) * mm});
            skLineSegment(sketch, "E14.30.2.2", {"start": v(178.47, 30.68) * mm, "end": v(206.85, 30.68) * mm});
            skLineSegment(sketch, "E14.33.2.2", {"start": v(206.85, 30.68) * mm, "end": v(227.58, 44.14) * mm});
            skLineSegment(sketch, "E14.0.2.3", {"start": v(210.1, 89.03) * mm, "end": v(230.85, 102.5) * mm});
            skLineSegment(sketch, "E14.3.2.3", {"start": v(230.85, 102.5) * mm, "end": v(259.22, 102.5) * mm});
            skLineSegment(sketch, "E14.6.2.3", {"start": v(259.22, 102.5) * mm, "end": v(279.96, 89.03) * mm});
            skLineSegment(sketch, "E14.9.2.3", {"start": v(230.85, 75.57) * mm, "end": v(210.1, 89.03) * mm});
            skLineSegment(sketch, "E14.12.2.3", {"start": v(279.96, 89.03) * mm, "end": v(259.22, 75.57) * mm});
            skLineSegment(sketch, "E14.15.2.3", {"start": v(227.58, 74.09) * mm, "end": v(206.85, 87.55) * mm});
            skLineSegment(sketch, "E14.18.2.3", {"start": v(259.22, 75.57) * mm, "end": v(230.85, 75.57) * mm});
            skLineSegment(sketch, "E14.21.2.3", {"start": v(206.85, 87.55) * mm, "end": v(178.47, 87.55) * mm});
            skLineSegment(sketch, "E14.24.2.3", {"start": v(178.47, 87.55) * mm, "end": v(157.73, 74.09) * mm});
            skLineSegment(sketch, "E14.27.2.3", {"start": v(157.73, 74.09) * mm, "end": v(178.47, 60.62) * mm});
            skLineSegment(sketch, "E14.30.2.3", {"start": v(178.47, 60.62) * mm, "end": v(206.85, 60.62) * mm});
            skLineSegment(sketch, "E14.33.2.3", {"start": v(206.85, 60.62) * mm, "end": v(227.58, 74.09) * mm});
            skLineSegment(sketch, "E14.0.2.4", {"start": v(210.1, 118.98) * mm, "end": v(230.85, 132.44) * mm});
            skLineSegment(sketch, "E14.3.2.4", {"start": v(230.85, 132.44) * mm, "end": v(259.22, 132.44) * mm});
            skLineSegment(sketch, "E14.6.2.4", {"start": v(259.22, 132.44) * mm, "end": v(279.96, 118.98) * mm});
            skLineSegment(sketch, "E14.9.2.4", {"start": v(230.85, 105.52) * mm, "end": v(210.1, 118.98) * mm});
            skLineSegment(sketch, "E14.12.2.4", {"start": v(279.96, 118.98) * mm, "end": v(259.22, 105.52) * mm});
            skLineSegment(sketch, "E14.15.2.4", {"start": v(227.58, 104.03) * mm, "end": v(206.85, 117.5) * mm});
            skLineSegment(sketch, "E14.18.2.4", {"start": v(259.22, 105.52) * mm, "end": v(230.85, 105.52) * mm});
            skLineSegment(sketch, "E14.21.2.4", {"start": v(206.85, 117.5) * mm, "end": v(178.47, 117.5) * mm});
            skLineSegment(sketch, "E14.24.2.4", {"start": v(178.47, 117.5) * mm, "end": v(157.73, 104.03) * mm});
            skLineSegment(sketch, "E14.27.2.4", {"start": v(157.73, 104.03) * mm, "end": v(178.47, 90.57) * mm});
            skLineSegment(sketch, "E14.30.2.4", {"start": v(178.47, 90.57) * mm, "end": v(206.85, 90.57) * mm});
            skLineSegment(sketch, "E14.33.2.4", {"start": v(206.85, 90.57) * mm, "end": v(227.58, 104.03) * mm});
            skLineSegment(sketch, "E14.0.2.5", {"start": v(210.1, 148.93) * mm, "end": v(230.85, 162.39) * mm});
            skLineSegment(sketch, "E14.3.2.5", {"start": v(230.85, 162.39) * mm, "end": v(259.22, 162.39) * mm});
            skLineSegment(sketch, "E14.6.2.5", {"start": v(259.22, 162.39) * mm, "end": v(279.96, 148.93) * mm});
            skLineSegment(sketch, "E14.9.2.5", {"start": v(230.85, 135.46) * mm, "end": v(210.1, 148.93) * mm});
            skLineSegment(sketch, "E14.12.2.5", {"start": v(279.96, 148.93) * mm, "end": v(259.22, 135.46) * mm});
            skLineSegment(sketch, "E14.15.2.5", {"start": v(227.58, 133.98) * mm, "end": v(206.85, 147.44) * mm});
            skLineSegment(sketch, "E14.18.2.5", {"start": v(259.22, 135.46) * mm, "end": v(230.85, 135.46) * mm});
            skLineSegment(sketch, "E14.21.2.5", {"start": v(206.85, 147.44) * mm, "end": v(178.47, 147.44) * mm});
            skLineSegment(sketch, "E14.24.2.5", {"start": v(178.47, 147.44) * mm, "end": v(157.73, 133.98) * mm});
            skLineSegment(sketch, "E14.27.2.5", {"start": v(157.73, 133.98) * mm, "end": v(178.47, 120.52) * mm});
            skLineSegment(sketch, "E14.30.2.5", {"start": v(178.47, 120.52) * mm, "end": v(206.85, 120.52) * mm});
            skLineSegment(sketch, "E14.33.2.5", {"start": v(206.85, 120.52) * mm, "end": v(227.58, 133.98) * mm});
            skLineSegment(sketch, "E14.0.2.6", {"start": v(210.1, 178.87) * mm, "end": v(230.85, 192.33) * mm});
            skLineSegment(sketch, "E14.3.2.6", {"start": v(230.85, 192.33) * mm, "end": v(259.22, 192.33) * mm});
            skLineSegment(sketch, "E14.6.2.6", {"start": v(259.22, 192.33) * mm, "end": v(279.96, 178.87) * mm});
            skLineSegment(sketch, "E14.9.2.6", {"start": v(230.85, 165.41) * mm, "end": v(210.1, 178.87) * mm});
            skLineSegment(sketch, "E14.12.2.6", {"start": v(279.96, 178.87) * mm, "end": v(259.22, 165.41) * mm});
            skLineSegment(sketch, "E14.15.2.6", {"start": v(227.58, 163.93) * mm, "end": v(206.85, 177.39) * mm});
            skLineSegment(sketch, "E14.18.2.6", {"start": v(259.22, 165.41) * mm, "end": v(230.85, 165.41) * mm});
            skLineSegment(sketch, "E14.21.2.6", {"start": v(206.85, 177.39) * mm, "end": v(178.47, 177.39) * mm});
            skLineSegment(sketch, "E14.24.2.6", {"start": v(178.47, 177.39) * mm, "end": v(157.73, 163.93) * mm});
            skLineSegment(sketch, "E14.27.2.6", {"start": v(157.73, 163.93) * mm, "end": v(178.47, 150.46) * mm});
            skLineSegment(sketch, "E14.30.2.6", {"start": v(178.47, 150.46) * mm, "end": v(206.85, 150.46) * mm});
            skLineSegment(sketch, "E14.33.2.6", {"start": v(206.85, 150.46) * mm, "end": v(227.58, 163.93) * mm});
            skLineSegment(sketch, "E14.0.2.7", {"start": v(210.1, 208.82) * mm, "end": v(230.85, 222.28) * mm});
            skLineSegment(sketch, "E14.3.2.7", {"start": v(230.85, 222.28) * mm, "end": v(259.22, 222.28) * mm});
            skLineSegment(sketch, "E14.6.2.7", {"start": v(259.22, 222.28) * mm, "end": v(279.96, 208.82) * mm});
            skLineSegment(sketch, "E14.9.2.7", {"start": v(230.85, 195.36) * mm, "end": v(210.1, 208.82) * mm});
            skLineSegment(sketch, "E14.12.2.7", {"start": v(279.96, 208.82) * mm, "end": v(259.22, 195.36) * mm});
            skLineSegment(sketch, "E14.15.2.7", {"start": v(227.58, 193.87) * mm, "end": v(206.85, 207.33) * mm});
            skLineSegment(sketch, "E14.18.2.7", {"start": v(259.22, 195.36) * mm, "end": v(230.85, 195.36) * mm});
            skLineSegment(sketch, "E14.21.2.7", {"start": v(206.85, 207.33) * mm, "end": v(178.47, 207.33) * mm});
            skLineSegment(sketch, "E14.24.2.7", {"start": v(178.47, 207.33) * mm, "end": v(157.73, 193.87) * mm});
            skLineSegment(sketch, "E14.27.2.7", {"start": v(157.73, 193.87) * mm, "end": v(178.47, 180.4) * mm});
            skLineSegment(sketch, "E14.30.2.7", {"start": v(178.47, 180.4) * mm, "end": v(206.85, 180.4) * mm});
            skLineSegment(sketch, "E14.33.2.7", {"start": v(206.85, 180.4) * mm, "end": v(227.58, 193.87) * mm});
            skLineSegment(sketch, "E14.0.2.8", {"start": v(210.1, 238.77) * mm, "end": v(230.85, 252.23) * mm});
            skLineSegment(sketch, "E14.3.2.8", {"start": v(230.85, 252.23) * mm, "end": v(259.22, 252.23) * mm});
            skLineSegment(sketch, "E14.6.2.8", {"start": v(259.22, 252.23) * mm, "end": v(279.96, 238.77) * mm});
            skLineSegment(sketch, "E14.9.2.8", {"start": v(230.85, 225.3) * mm, "end": v(210.1, 238.77) * mm});
            skLineSegment(sketch, "E14.12.2.8", {"start": v(279.96, 238.77) * mm, "end": v(259.22, 225.3) * mm});
            skLineSegment(sketch, "E14.15.2.8", {"start": v(227.58, 223.82) * mm, "end": v(206.85, 237.28) * mm});
            skLineSegment(sketch, "E14.18.2.8", {"start": v(259.22, 225.3) * mm, "end": v(230.85, 225.3) * mm});
            skLineSegment(sketch, "E14.21.2.8", {"start": v(206.85, 237.28) * mm, "end": v(178.47, 237.28) * mm});
            skLineSegment(sketch, "E14.24.2.8", {"start": v(178.47, 237.28) * mm, "end": v(157.73, 223.82) * mm});
            skLineSegment(sketch, "E14.27.2.8", {"start": v(157.73, 223.82) * mm, "end": v(178.47, 210.36) * mm});
            skLineSegment(sketch, "E14.30.2.8", {"start": v(178.47, 210.36) * mm, "end": v(206.85, 210.36) * mm});
            skLineSegment(sketch, "E14.33.2.8", {"start": v(206.85, 210.36) * mm, "end": v(227.58, 223.82) * mm});
            skLineSegment(sketch, "E14.0.2.9", {"start": v(210.1, 268.71) * mm, "end": v(230.85, 282.17) * mm});
            skLineSegment(sketch, "E14.3.2.9", {"start": v(230.85, 282.17) * mm, "end": v(259.22, 282.17) * mm});
            skLineSegment(sketch, "E14.6.2.9", {"start": v(259.22, 282.17) * mm, "end": v(279.96, 268.71) * mm});
            skLineSegment(sketch, "E14.9.2.9", {"start": v(230.85, 255.25) * mm, "end": v(210.1, 268.71) * mm});
            skLineSegment(sketch, "E14.12.2.9", {"start": v(279.96, 268.71) * mm, "end": v(259.22, 255.25) * mm});
            skLineSegment(sketch, "E14.15.2.9", {"start": v(227.58, 253.77) * mm, "end": v(206.85, 267.23) * mm});
            skLineSegment(sketch, "E14.18.2.9", {"start": v(259.22, 255.25) * mm, "end": v(230.85, 255.25) * mm});
            skLineSegment(sketch, "E14.21.2.9", {"start": v(206.85, 267.23) * mm, "end": v(178.47, 267.23) * mm});
            skLineSegment(sketch, "E14.24.2.9", {"start": v(178.47, 267.23) * mm, "end": v(157.73, 253.77) * mm});
            skLineSegment(sketch, "E14.27.2.9", {"start": v(157.73, 253.77) * mm, "end": v(178.47, 240.3) * mm});
            skLineSegment(sketch, "E14.30.2.9", {"start": v(178.47, 240.3) * mm, "end": v(206.85, 240.3) * mm});
            skLineSegment(sketch, "E14.33.2.9", {"start": v(206.85, 240.3) * mm, "end": v(227.58, 253.77) * mm});
            skLineSegment(sketch, "E14.0.2.10", {"start": v(210.1, 298.66) * mm, "end": v(230.85, 312.12) * mm});
            skLineSegment(sketch, "E14.3.2.10", {"start": v(230.85, 312.12) * mm, "end": v(259.22, 312.12) * mm});
            skLineSegment(sketch, "E14.6.2.10", {"start": v(259.22, 312.12) * mm, "end": v(279.96, 298.66) * mm});
            skLineSegment(sketch, "E14.9.2.10", {"start": v(230.85, 285.2) * mm, "end": v(210.1, 298.66) * mm});
            skLineSegment(sketch, "E14.12.2.10", {"start": v(279.96, 298.66) * mm, "end": v(259.22, 285.2) * mm});
            skLineSegment(sketch, "E14.15.2.10", {"start": v(227.58, 283.71) * mm, "end": v(206.85, 297.17) * mm});
            skLineSegment(sketch, "E14.18.2.10", {"start": v(259.22, 285.2) * mm, "end": v(230.85, 285.2) * mm});
            skLineSegment(sketch, "E14.21.2.10", {"start": v(206.85, 297.17) * mm, "end": v(178.47, 297.17) * mm});
            skLineSegment(sketch, "E14.24.2.10", {"start": v(178.47, 297.17) * mm, "end": v(157.73, 283.71) * mm});
            skLineSegment(sketch, "E14.27.2.10", {"start": v(157.73, 283.71) * mm, "end": v(178.47, 270.25) * mm});
            skLineSegment(sketch, "E14.30.2.10", {"start": v(178.47, 270.25) * mm, "end": v(206.85, 270.25) * mm});
            skLineSegment(sketch, "E14.33.2.10", {"start": v(206.85, 270.25) * mm, "end": v(227.58, 283.71) * mm});
            skLineSegment(sketch, "E14.0.2.11", {"start": v(210.1, 328.6) * mm, "end": v(230.85, 342.07) * mm});
            skLineSegment(sketch, "E14.3.2.11", {"start": v(230.85, 342.07) * mm, "end": v(259.22, 342.07) * mm});
            skLineSegment(sketch, "E14.6.2.11", {"start": v(259.22, 342.07) * mm, "end": v(279.96, 328.6) * mm});
            skLineSegment(sketch, "E14.9.2.11", {"start": v(230.85, 315.14) * mm, "end": v(210.1, 328.6) * mm});
            skLineSegment(sketch, "E14.12.2.11", {"start": v(279.96, 328.6) * mm, "end": v(259.22, 315.14) * mm});
            skLineSegment(sketch, "E14.15.2.11", {"start": v(227.58, 313.66) * mm, "end": v(206.85, 327.12) * mm});
            skLineSegment(sketch, "E14.18.2.11", {"start": v(259.22, 315.14) * mm, "end": v(230.85, 315.14) * mm});
            skLineSegment(sketch, "E14.21.2.11", {"start": v(206.85, 327.12) * mm, "end": v(178.47, 327.12) * mm});
            skLineSegment(sketch, "E14.24.2.11", {"start": v(178.47, 327.12) * mm, "end": v(157.73, 313.66) * mm});
            skLineSegment(sketch, "E14.27.2.11", {"start": v(157.73, 313.66) * mm, "end": v(178.47, 300.2) * mm});
            skLineSegment(sketch, "E14.30.2.11", {"start": v(178.47, 300.2) * mm, "end": v(206.85, 300.2) * mm});
            skLineSegment(sketch, "E14.33.2.11", {"start": v(206.85, 300.2) * mm, "end": v(227.58, 313.66) * mm});
            skLineSegment(sketch, "E14.0.2.12", {"start": v(210.1, 358.55) * mm, "end": v(230.85, 372.01) * mm});
            skLineSegment(sketch, "E14.3.2.12", {"start": v(230.85, 372.01) * mm, "end": v(259.22, 372.01) * mm});
            skLineSegment(sketch, "E14.6.2.12", {"start": v(259.22, 372.01) * mm, "end": v(279.96, 358.55) * mm});
            skLineSegment(sketch, "E14.9.2.12", {"start": v(230.85, 345.1) * mm, "end": v(210.1, 358.55) * mm});
            skLineSegment(sketch, "E14.12.2.12", {"start": v(279.96, 358.55) * mm, "end": v(259.22, 345.1) * mm});
            skLineSegment(sketch, "E14.15.2.12", {"start": v(227.58, 343.6) * mm, "end": v(206.85, 357.07) * mm});
            skLineSegment(sketch, "E14.18.2.12", {"start": v(259.22, 345.1) * mm, "end": v(230.85, 345.1) * mm});
            skLineSegment(sketch, "E14.21.2.12", {"start": v(206.85, 357.07) * mm, "end": v(178.47, 357.07) * mm});
            skLineSegment(sketch, "E14.24.2.12", {"start": v(178.47, 357.07) * mm, "end": v(157.73, 343.6) * mm});
            skLineSegment(sketch, "E14.27.2.12", {"start": v(157.73, 343.6) * mm, "end": v(178.47, 330.14) * mm});
            skLineSegment(sketch, "E14.30.2.12", {"start": v(178.47, 330.14) * mm, "end": v(206.85, 330.14) * mm});
            skLineSegment(sketch, "E14.33.2.12", {"start": v(206.85, 330.14) * mm, "end": v(227.58, 343.6) * mm});
            skLineSegment(sketch, "E14.0.2.13", {"start": v(210.1, 388.5) * mm, "end": v(230.85, 401.96) * mm});
            skLineSegment(sketch, "E14.3.2.13", {"start": v(230.85, 401.96) * mm, "end": v(259.22, 401.96) * mm});
            skLineSegment(sketch, "E14.6.2.13", {"start": v(259.22, 401.96) * mm, "end": v(279.96, 388.5) * mm});
            skLineSegment(sketch, "E14.9.2.13", {"start": v(230.85, 375.04) * mm, "end": v(210.1, 388.5) * mm});
            skLineSegment(sketch, "E14.12.2.13", {"start": v(279.96, 388.5) * mm, "end": v(259.22, 375.04) * mm});
            skLineSegment(sketch, "E14.15.2.13", {"start": v(227.58, 373.55) * mm, "end": v(206.85, 387.01) * mm});
            skLineSegment(sketch, "E14.18.2.13", {"start": v(259.22, 375.04) * mm, "end": v(230.85, 375.04) * mm});
            skLineSegment(sketch, "E14.21.2.13", {"start": v(206.85, 387.01) * mm, "end": v(178.47, 387.01) * mm});
            skLineSegment(sketch, "E14.24.2.13", {"start": v(178.47, 387.01) * mm, "end": v(157.73, 373.55) * mm});
            skLineSegment(sketch, "E14.27.2.13", {"start": v(157.73, 373.55) * mm, "end": v(178.47, 360.09) * mm});
            skLineSegment(sketch, "E14.30.2.13", {"start": v(178.47, 360.09) * mm, "end": v(206.85, 360.09) * mm});
            skLineSegment(sketch, "E14.33.2.13", {"start": v(206.85, 360.09) * mm, "end": v(227.58, 373.55) * mm});
            skLineSegment(sketch, "E14.0.2.14", {"start": v(210.1, 418.45) * mm, "end": v(230.85, 431.9) * mm});
            skLineSegment(sketch, "E14.3.2.14", {"start": v(230.85, 431.9) * mm, "end": v(259.22, 431.9) * mm});
            skLineSegment(sketch, "E14.6.2.14", {"start": v(259.22, 431.9) * mm, "end": v(279.96, 418.45) * mm});
            skLineSegment(sketch, "E14.9.2.14", {"start": v(230.85, 404.98) * mm, "end": v(210.1, 418.45) * mm});
            skLineSegment(sketch, "E14.12.2.14", {"start": v(279.96, 418.45) * mm, "end": v(259.22, 404.98) * mm});
            skLineSegment(sketch, "E14.15.2.14", {"start": v(227.58, 403.5) * mm, "end": v(206.85, 416.96) * mm});
            skLineSegment(sketch, "E14.18.2.14", {"start": v(259.22, 404.98) * mm, "end": v(230.85, 404.98) * mm});
            skLineSegment(sketch, "E14.21.2.14", {"start": v(206.85, 416.96) * mm, "end": v(178.47, 416.96) * mm});
            skLineSegment(sketch, "E14.24.2.14", {"start": v(178.47, 416.96) * mm, "end": v(157.73, 403.5) * mm});
            skLineSegment(sketch, "E14.27.2.14", {"start": v(157.73, 403.5) * mm, "end": v(178.47, 390.04) * mm});
            skLineSegment(sketch, "E14.30.2.14", {"start": v(178.47, 390.04) * mm, "end": v(206.85, 390.04) * mm});
            skLineSegment(sketch, "E14.33.2.14", {"start": v(206.85, 390.04) * mm, "end": v(227.58, 403.5) * mm});
            skLineSegment(sketch, "E14.0.2.15", {"start": v(210.1, 448.4) * mm, "end": v(230.85, 461.85) * mm});
            skLineSegment(sketch, "E14.3.2.15", {"start": v(230.85, 461.85) * mm, "end": v(259.22, 461.85) * mm});
            skLineSegment(sketch, "E14.6.2.15", {"start": v(259.22, 461.85) * mm, "end": v(279.96, 448.4) * mm});
            skLineSegment(sketch, "E14.9.2.15", {"start": v(230.85, 434.93) * mm, "end": v(210.1, 448.4) * mm});
            skLineSegment(sketch, "E14.12.2.15", {"start": v(279.96, 448.4) * mm, "end": v(259.22, 434.93) * mm});
            skLineSegment(sketch, "E14.15.2.15", {"start": v(227.58, 433.44) * mm, "end": v(206.85, 446.9) * mm});
            skLineSegment(sketch, "E14.18.2.15", {"start": v(259.22, 434.93) * mm, "end": v(230.85, 434.93) * mm});
            skLineSegment(sketch, "E14.21.2.15", {"start": v(206.85, 446.9) * mm, "end": v(178.47, 446.9) * mm});
            skLineSegment(sketch, "E14.24.2.15", {"start": v(178.47, 446.9) * mm, "end": v(157.73, 433.44) * mm});
            skLineSegment(sketch, "E14.27.2.15", {"start": v(157.73, 433.44) * mm, "end": v(178.47, 419.98) * mm});
            skLineSegment(sketch, "E14.30.2.15", {"start": v(178.47, 419.98) * mm, "end": v(206.85, 419.98) * mm});
            skLineSegment(sketch, "E14.33.2.15", {"start": v(206.85, 419.98) * mm, "end": v(227.58, 433.44) * mm});
            skLineSegment(sketch, "E14.0.2.16", {"start": v(210.1, 478.34) * mm, "end": v(230.85, 491.8) * mm});
            skLineSegment(sketch, "E14.3.2.16", {"start": v(230.85, 491.8) * mm, "end": v(259.22, 491.8) * mm});
            skLineSegment(sketch, "E14.6.2.16", {"start": v(259.22, 491.8) * mm, "end": v(279.96, 478.34) * mm});
            skLineSegment(sketch, "E14.9.2.16", {"start": v(230.85, 464.88) * mm, "end": v(210.1, 478.34) * mm});
            skLineSegment(sketch, "E14.12.2.16", {"start": v(279.96, 478.34) * mm, "end": v(259.22, 464.88) * mm});
            skLineSegment(sketch, "E14.15.2.16", {"start": v(227.58, 463.4) * mm, "end": v(206.85, 476.85) * mm});
            skLineSegment(sketch, "E14.18.2.16", {"start": v(259.22, 464.88) * mm, "end": v(230.85, 464.88) * mm});
            skLineSegment(sketch, "E14.21.2.16", {"start": v(206.85, 476.85) * mm, "end": v(178.47, 476.85) * mm});
            skLineSegment(sketch, "E14.24.2.16", {"start": v(178.47, 476.85) * mm, "end": v(157.73, 463.4) * mm});
            skLineSegment(sketch, "E14.27.2.16", {"start": v(157.73, 463.4) * mm, "end": v(178.47, 449.93) * mm});
            skLineSegment(sketch, "E14.30.2.16", {"start": v(178.47, 449.93) * mm, "end": v(206.85, 449.93) * mm});
            skLineSegment(sketch, "E14.33.2.16", {"start": v(206.85, 449.93) * mm, "end": v(227.58, 463.4) * mm});
            skLineSegment(sketch, "E14.0.3.2", {"start": v(314.24, 58.68) * mm, "end": v(334.98, 72.14) * mm});
            skLineSegment(sketch, "E14.3.3.2", {"start": v(334.98, 72.14) * mm, "end": v(363.35, 72.14) * mm});
            skLineSegment(sketch, "E14.6.3.2", {"start": v(363.35, 72.14) * mm, "end": v(384.09, 58.68) * mm});
            skLineSegment(sketch, "E14.9.3.2", {"start": v(334.98, 45.22) * mm, "end": v(314.24, 58.68) * mm});
            skLineSegment(sketch, "E14.12.3.2", {"start": v(384.09, 58.68) * mm, "end": v(363.35, 45.22) * mm});
            skLineSegment(sketch, "E14.15.3.2", {"start": v(331.71, 43.74) * mm, "end": v(310.97, 57.2) * mm});
            skLineSegment(sketch, "E14.18.3.2", {"start": v(363.35, 45.22) * mm, "end": v(334.98, 45.22) * mm});
            skLineSegment(sketch, "E14.21.3.2", {"start": v(310.97, 57.2) * mm, "end": v(282.6, 57.2) * mm});
            skLineSegment(sketch, "E14.24.3.2", {"start": v(282.6, 57.2) * mm, "end": v(261.86, 43.74) * mm});
            skLineSegment(sketch, "E14.27.3.2", {"start": v(261.86, 43.74) * mm, "end": v(282.6, 30.27) * mm});
            skLineSegment(sketch, "E14.30.3.2", {"start": v(282.6, 30.27) * mm, "end": v(310.97, 30.27) * mm});
            skLineSegment(sketch, "E14.33.3.2", {"start": v(310.97, 30.27) * mm, "end": v(331.71, 43.74) * mm});
            skLineSegment(sketch, "E14.0.3.3", {"start": v(314.24, 88.63) * mm, "end": v(334.98, 102.1) * mm});
            skLineSegment(sketch, "E14.3.3.3", {"start": v(334.98, 102.1) * mm, "end": v(363.35, 102.1) * mm});
            skLineSegment(sketch, "E14.6.3.3", {"start": v(363.35, 102.1) * mm, "end": v(384.09, 88.63) * mm});
            skLineSegment(sketch, "E14.9.3.3", {"start": v(334.98, 75.17) * mm, "end": v(314.24, 88.63) * mm});
            skLineSegment(sketch, "E14.12.3.3", {"start": v(384.09, 88.63) * mm, "end": v(363.35, 75.17) * mm});
            skLineSegment(sketch, "E14.15.3.3", {"start": v(331.71, 73.68) * mm, "end": v(310.97, 87.14) * mm});
            skLineSegment(sketch, "E14.18.3.3", {"start": v(363.35, 75.17) * mm, "end": v(334.98, 75.17) * mm});
            skLineSegment(sketch, "E14.21.3.3", {"start": v(310.97, 87.14) * mm, "end": v(282.6, 87.14) * mm});
            skLineSegment(sketch, "E14.24.3.3", {"start": v(282.6, 87.14) * mm, "end": v(261.86, 73.68) * mm});
            skLineSegment(sketch, "E14.27.3.3", {"start": v(261.86, 73.68) * mm, "end": v(282.6, 60.22) * mm});
            skLineSegment(sketch, "E14.30.3.3", {"start": v(282.6, 60.22) * mm, "end": v(310.97, 60.22) * mm});
            skLineSegment(sketch, "E14.33.3.3", {"start": v(310.97, 60.22) * mm, "end": v(331.71, 73.68) * mm});
            skLineSegment(sketch, "E14.0.3.4", {"start": v(314.24, 118.58) * mm, "end": v(334.98, 132.04) * mm});
            skLineSegment(sketch, "E14.3.3.4", {"start": v(334.98, 132.04) * mm, "end": v(363.35, 132.04) * mm});
            skLineSegment(sketch, "E14.6.3.4", {"start": v(363.35, 132.04) * mm, "end": v(384.09, 118.58) * mm});
            skLineSegment(sketch, "E14.9.3.4", {"start": v(334.98, 105.11) * mm, "end": v(314.24, 118.58) * mm});
            skLineSegment(sketch, "E14.12.3.4", {"start": v(384.09, 118.58) * mm, "end": v(363.35, 105.11) * mm});
            skLineSegment(sketch, "E14.15.3.4", {"start": v(331.71, 103.63) * mm, "end": v(310.97, 117.1) * mm});
            skLineSegment(sketch, "E14.18.3.4", {"start": v(363.35, 105.11) * mm, "end": v(334.98, 105.11) * mm});
            skLineSegment(sketch, "E14.21.3.4", {"start": v(310.97, 117.1) * mm, "end": v(282.6, 117.1) * mm});
            skLineSegment(sketch, "E14.24.3.4", {"start": v(282.6, 117.1) * mm, "end": v(261.86, 103.63) * mm});
            skLineSegment(sketch, "E14.27.3.4", {"start": v(261.86, 103.63) * mm, "end": v(282.6, 90.17) * mm});
            skLineSegment(sketch, "E14.30.3.4", {"start": v(282.6, 90.17) * mm, "end": v(310.97, 90.17) * mm});
            skLineSegment(sketch, "E14.33.3.4", {"start": v(310.97, 90.17) * mm, "end": v(331.71, 103.63) * mm});
            skLineSegment(sketch, "E14.0.3.5", {"start": v(314.24, 148.52) * mm, "end": v(334.98, 161.98) * mm});
            skLineSegment(sketch, "E14.3.3.5", {"start": v(334.98, 161.98) * mm, "end": v(363.35, 161.98) * mm});
            skLineSegment(sketch, "E14.6.3.5", {"start": v(363.35, 161.98) * mm, "end": v(384.09, 148.52) * mm});
            skLineSegment(sketch, "E14.9.3.5", {"start": v(334.98, 135.06) * mm, "end": v(314.24, 148.52) * mm});
            skLineSegment(sketch, "E14.12.3.5", {"start": v(384.09, 148.52) * mm, "end": v(363.35, 135.06) * mm});
            skLineSegment(sketch, "E14.15.3.5", {"start": v(331.71, 133.58) * mm, "end": v(310.97, 147.04) * mm});
            skLineSegment(sketch, "E14.18.3.5", {"start": v(363.35, 135.06) * mm, "end": v(334.98, 135.06) * mm});
            skLineSegment(sketch, "E14.21.3.5", {"start": v(310.97, 147.04) * mm, "end": v(282.6, 147.04) * mm});
            skLineSegment(sketch, "E14.24.3.5", {"start": v(282.6, 147.04) * mm, "end": v(261.86, 133.58) * mm});
            skLineSegment(sketch, "E14.27.3.5", {"start": v(261.86, 133.58) * mm, "end": v(282.6, 120.11) * mm});
            skLineSegment(sketch, "E14.30.3.5", {"start": v(282.6, 120.11) * mm, "end": v(310.97, 120.11) * mm});
            skLineSegment(sketch, "E14.33.3.5", {"start": v(310.97, 120.11) * mm, "end": v(331.71, 133.58) * mm});
            skLineSegment(sketch, "E14.0.3.6", {"start": v(314.24, 178.47) * mm, "end": v(334.98, 191.93) * mm});
            skLineSegment(sketch, "E14.3.3.6", {"start": v(334.98, 191.93) * mm, "end": v(363.35, 191.93) * mm});
            skLineSegment(sketch, "E14.6.3.6", {"start": v(363.35, 191.93) * mm, "end": v(384.09, 178.47) * mm});
            skLineSegment(sketch, "E14.9.3.6", {"start": v(334.98, 165) * mm, "end": v(314.24, 178.47) * mm});
            skLineSegment(sketch, "E14.12.3.6", {"start": v(384.09, 178.47) * mm, "end": v(363.35, 165) * mm});
            skLineSegment(sketch, "E14.15.3.6", {"start": v(331.71, 163.52) * mm, "end": v(310.97, 176.98) * mm});
            skLineSegment(sketch, "E14.18.3.6", {"start": v(363.35, 165) * mm, "end": v(334.98, 165) * mm});
            skLineSegment(sketch, "E14.21.3.6", {"start": v(310.97, 176.98) * mm, "end": v(282.6, 176.98) * mm});
            skLineSegment(sketch, "E14.24.3.6", {"start": v(282.6, 176.98) * mm, "end": v(261.86, 163.52) * mm});
            skLineSegment(sketch, "E14.27.3.6", {"start": v(261.86, 163.52) * mm, "end": v(282.6, 150.06) * mm});
            skLineSegment(sketch, "E14.30.3.6", {"start": v(282.6, 150.06) * mm, "end": v(310.97, 150.06) * mm});
            skLineSegment(sketch, "E14.33.3.6", {"start": v(310.97, 150.06) * mm, "end": v(331.71, 163.52) * mm});
            skLineSegment(sketch, "E14.0.3.7", {"start": v(314.24, 208.42) * mm, "end": v(334.98, 221.88) * mm});
            skLineSegment(sketch, "E14.3.3.7", {"start": v(334.98, 221.88) * mm, "end": v(363.35, 221.88) * mm});
            skLineSegment(sketch, "E14.6.3.7", {"start": v(363.35, 221.88) * mm, "end": v(384.09, 208.42) * mm});
            skLineSegment(sketch, "E14.9.3.7", {"start": v(334.98, 194.95) * mm, "end": v(314.24, 208.42) * mm});
            skLineSegment(sketch, "E14.12.3.7", {"start": v(384.09, 208.42) * mm, "end": v(363.35, 194.95) * mm});
            skLineSegment(sketch, "E14.15.3.7", {"start": v(331.71, 193.47) * mm, "end": v(310.97, 206.93) * mm});
            skLineSegment(sketch, "E14.18.3.7", {"start": v(363.35, 194.95) * mm, "end": v(334.98, 194.95) * mm});
            skLineSegment(sketch, "E14.21.3.7", {"start": v(310.97, 206.93) * mm, "end": v(282.6, 206.93) * mm});
            skLineSegment(sketch, "E14.24.3.7", {"start": v(282.6, 206.93) * mm, "end": v(261.86, 193.47) * mm});
            skLineSegment(sketch, "E14.27.3.7", {"start": v(261.86, 193.47) * mm, "end": v(282.6, 180) * mm});
            skLineSegment(sketch, "E14.30.3.7", {"start": v(282.6, 180) * mm, "end": v(310.97, 180) * mm});
            skLineSegment(sketch, "E14.33.3.7", {"start": v(310.97, 180) * mm, "end": v(331.71, 193.47) * mm});
            skLineSegment(sketch, "E14.0.3.8", {"start": v(314.24, 238.36) * mm, "end": v(334.98, 251.82) * mm});
            skLineSegment(sketch, "E14.3.3.8", {"start": v(334.98, 251.82) * mm, "end": v(363.35, 251.82) * mm});
            skLineSegment(sketch, "E14.6.3.8", {"start": v(363.35, 251.82) * mm, "end": v(384.09, 238.36) * mm});
            skLineSegment(sketch, "E14.9.3.8", {"start": v(334.98, 224.9) * mm, "end": v(314.24, 238.36) * mm});
            skLineSegment(sketch, "E14.12.3.8", {"start": v(384.09, 238.36) * mm, "end": v(363.35, 224.9) * mm});
            skLineSegment(sketch, "E14.15.3.8", {"start": v(331.71, 223.42) * mm, "end": v(310.97, 236.88) * mm});
            skLineSegment(sketch, "E14.18.3.8", {"start": v(363.35, 224.9) * mm, "end": v(334.98, 224.9) * mm});
            skLineSegment(sketch, "E14.21.3.8", {"start": v(310.97, 236.88) * mm, "end": v(282.6, 236.88) * mm});
            skLineSegment(sketch, "E14.24.3.8", {"start": v(282.6, 236.88) * mm, "end": v(261.86, 223.42) * mm});
            skLineSegment(sketch, "E14.27.3.8", {"start": v(261.86, 223.42) * mm, "end": v(282.6, 209.95) * mm});
            skLineSegment(sketch, "E14.30.3.8", {"start": v(282.6, 209.95) * mm, "end": v(310.97, 209.95) * mm});
            skLineSegment(sketch, "E14.33.3.8", {"start": v(310.97, 209.95) * mm, "end": v(331.71, 223.42) * mm});
            skLineSegment(sketch, "E14.0.3.9", {"start": v(314.24, 268.3) * mm, "end": v(334.98, 281.77) * mm});
            skLineSegment(sketch, "E14.3.3.9", {"start": v(334.98, 281.77) * mm, "end": v(363.35, 281.77) * mm});
            skLineSegment(sketch, "E14.6.3.9", {"start": v(363.35, 281.77) * mm, "end": v(384.09, 268.3) * mm});
            skLineSegment(sketch, "E14.9.3.9", {"start": v(334.98, 254.85) * mm, "end": v(314.24, 268.3) * mm});
            skLineSegment(sketch, "E14.12.3.9", {"start": v(384.09, 268.3) * mm, "end": v(363.35, 254.85) * mm});
            skLineSegment(sketch, "E14.15.3.9", {"start": v(331.71, 253.36) * mm, "end": v(310.97, 266.82) * mm});
            skLineSegment(sketch, "E14.18.3.9", {"start": v(363.35, 254.85) * mm, "end": v(334.98, 254.85) * mm});
            skLineSegment(sketch, "E14.21.3.9", {"start": v(310.97, 266.82) * mm, "end": v(282.6, 266.82) * mm});
            skLineSegment(sketch, "E14.24.3.9", {"start": v(282.6, 266.82) * mm, "end": v(261.86, 253.36) * mm});
            skLineSegment(sketch, "E14.27.3.9", {"start": v(261.86, 253.36) * mm, "end": v(282.6, 239.9) * mm});
            skLineSegment(sketch, "E14.30.3.9", {"start": v(282.6, 239.9) * mm, "end": v(310.97, 239.9) * mm});
            skLineSegment(sketch, "E14.33.3.9", {"start": v(310.97, 239.9) * mm, "end": v(331.71, 253.36) * mm});
            skLineSegment(sketch, "E14.0.3.10", {"start": v(314.24, 298.26) * mm, "end": v(334.98, 311.72) * mm});
            skLineSegment(sketch, "E14.3.3.10", {"start": v(334.98, 311.72) * mm, "end": v(363.35, 311.72) * mm});
            skLineSegment(sketch, "E14.6.3.10", {"start": v(363.35, 311.72) * mm, "end": v(384.09, 298.26) * mm});
            skLineSegment(sketch, "E14.9.3.10", {"start": v(334.98, 284.8) * mm, "end": v(314.24, 298.26) * mm});
            skLineSegment(sketch, "E14.12.3.10", {"start": v(384.09, 298.26) * mm, "end": v(363.35, 284.8) * mm});
            skLineSegment(sketch, "E14.15.3.10", {"start": v(331.71, 283.3) * mm, "end": v(310.97, 296.77) * mm});
            skLineSegment(sketch, "E14.18.3.10", {"start": v(363.35, 284.8) * mm, "end": v(334.98, 284.8) * mm});
            skLineSegment(sketch, "E14.21.3.10", {"start": v(310.97, 296.77) * mm, "end": v(282.6, 296.77) * mm});
            skLineSegment(sketch, "E14.24.3.10", {"start": v(282.6, 296.77) * mm, "end": v(261.86, 283.3) * mm});
            skLineSegment(sketch, "E14.27.3.10", {"start": v(261.86, 283.3) * mm, "end": v(282.6, 269.85) * mm});
            skLineSegment(sketch, "E14.30.3.10", {"start": v(282.6, 269.85) * mm, "end": v(310.97, 269.85) * mm});
            skLineSegment(sketch, "E14.33.3.10", {"start": v(310.97, 269.85) * mm, "end": v(331.71, 283.3) * mm});
            skLineSegment(sketch, "E14.0.3.11", {"start": v(314.24, 328.2) * mm, "end": v(334.98, 341.66) * mm});
            skLineSegment(sketch, "E14.3.3.11", {"start": v(334.98, 341.66) * mm, "end": v(363.35, 341.66) * mm});
            skLineSegment(sketch, "E14.6.3.11", {"start": v(363.35, 341.66) * mm, "end": v(384.09, 328.2) * mm});
            skLineSegment(sketch, "E14.9.3.11", {"start": v(334.98, 314.74) * mm, "end": v(314.24, 328.2) * mm});
            skLineSegment(sketch, "E14.12.3.11", {"start": v(384.09, 328.2) * mm, "end": v(363.35, 314.74) * mm});
            skLineSegment(sketch, "E14.15.3.11", {"start": v(331.71, 313.25) * mm, "end": v(310.97, 326.72) * mm});
            skLineSegment(sketch, "E14.18.3.11", {"start": v(363.35, 314.74) * mm, "end": v(334.98, 314.74) * mm});
            skLineSegment(sketch, "E14.21.3.11", {"start": v(310.97, 326.72) * mm, "end": v(282.6, 326.72) * mm});
            skLineSegment(sketch, "E14.24.3.11", {"start": v(282.6, 326.72) * mm, "end": v(261.86, 313.25) * mm});
            skLineSegment(sketch, "E14.27.3.11", {"start": v(261.86, 313.25) * mm, "end": v(282.6, 299.8) * mm});
            skLineSegment(sketch, "E14.30.3.11", {"start": v(282.6, 299.8) * mm, "end": v(310.97, 299.8) * mm});
            skLineSegment(sketch, "E14.33.3.11", {"start": v(310.97, 299.8) * mm, "end": v(331.71, 313.25) * mm});
            skLineSegment(sketch, "E14.0.3.12", {"start": v(314.24, 358.15) * mm, "end": v(334.98, 371.61) * mm});
            skLineSegment(sketch, "E14.3.3.12", {"start": v(334.98, 371.61) * mm, "end": v(363.35, 371.61) * mm});
            skLineSegment(sketch, "E14.6.3.12", {"start": v(363.35, 371.61) * mm, "end": v(384.09, 358.15) * mm});
            skLineSegment(sketch, "E14.9.3.12", {"start": v(334.98, 344.69) * mm, "end": v(314.24, 358.15) * mm});
            skLineSegment(sketch, "E14.12.3.12", {"start": v(384.09, 358.15) * mm, "end": v(363.35, 344.69) * mm});
            skLineSegment(sketch, "E14.15.3.12", {"start": v(331.71, 343.2) * mm, "end": v(310.97, 356.66) * mm});
            skLineSegment(sketch, "E14.18.3.12", {"start": v(363.35, 344.69) * mm, "end": v(334.98, 344.69) * mm});
            skLineSegment(sketch, "E14.21.3.12", {"start": v(310.97, 356.66) * mm, "end": v(282.6, 356.66) * mm});
            skLineSegment(sketch, "E14.24.3.12", {"start": v(282.6, 356.66) * mm, "end": v(261.86, 343.2) * mm});
            skLineSegment(sketch, "E14.27.3.12", {"start": v(261.86, 343.2) * mm, "end": v(282.6, 329.74) * mm});
            skLineSegment(sketch, "E14.30.3.12", {"start": v(282.6, 329.74) * mm, "end": v(310.97, 329.74) * mm});
            skLineSegment(sketch, "E14.33.3.12", {"start": v(310.97, 329.74) * mm, "end": v(331.71, 343.2) * mm});
            skLineSegment(sketch, "E14.0.3.13", {"start": v(314.24, 388.1) * mm, "end": v(334.98, 401.56) * mm});
            skLineSegment(sketch, "E14.3.3.13", {"start": v(334.98, 401.56) * mm, "end": v(363.35, 401.56) * mm});
            skLineSegment(sketch, "E14.6.3.13", {"start": v(363.35, 401.56) * mm, "end": v(384.09, 388.1) * mm});
            skLineSegment(sketch, "E14.9.3.13", {"start": v(334.98, 374.63) * mm, "end": v(314.24, 388.1) * mm});
            skLineSegment(sketch, "E14.12.3.13", {"start": v(384.09, 388.1) * mm, "end": v(363.35, 374.63) * mm});
            skLineSegment(sketch, "E14.15.3.13", {"start": v(331.71, 373.15) * mm, "end": v(310.97, 386.61) * mm});
            skLineSegment(sketch, "E14.18.3.13", {"start": v(363.35, 374.63) * mm, "end": v(334.98, 374.63) * mm});
            skLineSegment(sketch, "E14.21.3.13", {"start": v(310.97, 386.61) * mm, "end": v(282.6, 386.61) * mm});
            skLineSegment(sketch, "E14.24.3.13", {"start": v(282.6, 386.61) * mm, "end": v(261.86, 373.15) * mm});
            skLineSegment(sketch, "E14.27.3.13", {"start": v(261.86, 373.15) * mm, "end": v(282.6, 359.69) * mm});
            skLineSegment(sketch, "E14.30.3.13", {"start": v(282.6, 359.69) * mm, "end": v(310.97, 359.69) * mm});
            skLineSegment(sketch, "E14.33.3.13", {"start": v(310.97, 359.69) * mm, "end": v(331.71, 373.15) * mm});
            skLineSegment(sketch, "E14.0.3.14", {"start": v(314.24, 418.04) * mm, "end": v(334.98, 431.5) * mm});
            skLineSegment(sketch, "E14.3.3.14", {"start": v(334.98, 431.5) * mm, "end": v(363.35, 431.5) * mm});
            skLineSegment(sketch, "E14.6.3.14", {"start": v(363.35, 431.5) * mm, "end": v(384.09, 418.04) * mm});
            skLineSegment(sketch, "E14.9.3.14", {"start": v(334.98, 404.58) * mm, "end": v(314.24, 418.04) * mm});
            skLineSegment(sketch, "E14.12.3.14", {"start": v(384.09, 418.04) * mm, "end": v(363.35, 404.58) * mm});
            skLineSegment(sketch, "E14.15.3.14", {"start": v(331.71, 403.1) * mm, "end": v(310.97, 416.56) * mm});
            skLineSegment(sketch, "E14.18.3.14", {"start": v(363.35, 404.58) * mm, "end": v(334.98, 404.58) * mm});
            skLineSegment(sketch, "E14.21.3.14", {"start": v(310.97, 416.56) * mm, "end": v(282.6, 416.56) * mm});
            skLineSegment(sketch, "E14.24.3.14", {"start": v(282.6, 416.56) * mm, "end": v(261.86, 403.1) * mm});
            skLineSegment(sketch, "E14.27.3.14", {"start": v(261.86, 403.1) * mm, "end": v(282.6, 389.63) * mm});
            skLineSegment(sketch, "E14.30.3.14", {"start": v(282.6, 389.63) * mm, "end": v(310.97, 389.63) * mm});
            skLineSegment(sketch, "E14.33.3.14", {"start": v(310.97, 389.63) * mm, "end": v(331.71, 403.1) * mm});
            skLineSegment(sketch, "E14.0.3.15", {"start": v(314.24, 447.99) * mm, "end": v(334.98, 461.45) * mm});
            skLineSegment(sketch, "E14.3.3.15", {"start": v(334.98, 461.45) * mm, "end": v(363.35, 461.45) * mm});
            skLineSegment(sketch, "E14.6.3.15", {"start": v(363.35, 461.45) * mm, "end": v(384.09, 447.99) * mm});
            skLineSegment(sketch, "E14.9.3.15", {"start": v(334.98, 434.53) * mm, "end": v(314.24, 447.99) * mm});
            skLineSegment(sketch, "E14.12.3.15", {"start": v(384.09, 447.99) * mm, "end": v(363.35, 434.53) * mm});
            skLineSegment(sketch, "E14.15.3.15", {"start": v(331.71, 433.04) * mm, "end": v(310.97, 446.5) * mm});
            skLineSegment(sketch, "E14.18.3.15", {"start": v(363.35, 434.53) * mm, "end": v(334.98, 434.53) * mm});
            skLineSegment(sketch, "E14.21.3.15", {"start": v(310.97, 446.5) * mm, "end": v(282.6, 446.5) * mm});
            skLineSegment(sketch, "E14.24.3.15", {"start": v(282.6, 446.5) * mm, "end": v(261.86, 433.04) * mm});
            skLineSegment(sketch, "E14.27.3.15", {"start": v(261.86, 433.04) * mm, "end": v(282.6, 419.58) * mm});
            skLineSegment(sketch, "E14.30.3.15", {"start": v(282.6, 419.58) * mm, "end": v(310.97, 419.58) * mm});
            skLineSegment(sketch, "E14.33.3.15", {"start": v(310.97, 419.58) * mm, "end": v(331.71, 433.04) * mm});
            skLineSegment(sketch, "E14.0.3.16", {"start": v(314.24, 477.94) * mm, "end": v(334.98, 491.4) * mm});
            skLineSegment(sketch, "E14.3.3.16", {"start": v(334.98, 491.4) * mm, "end": v(363.35, 491.4) * mm});
            skLineSegment(sketch, "E14.6.3.16", {"start": v(363.35, 491.4) * mm, "end": v(384.09, 477.94) * mm});
            skLineSegment(sketch, "E14.9.3.16", {"start": v(334.98, 464.47) * mm, "end": v(314.24, 477.94) * mm});
            skLineSegment(sketch, "E14.12.3.16", {"start": v(384.09, 477.94) * mm, "end": v(363.35, 464.47) * mm});
            skLineSegment(sketch, "E14.15.3.16", {"start": v(331.71, 462.99) * mm, "end": v(310.97, 476.45) * mm});
            skLineSegment(sketch, "E14.18.3.16", {"start": v(363.35, 464.47) * mm, "end": v(334.98, 464.47) * mm});
            skLineSegment(sketch, "E14.21.3.16", {"start": v(310.97, 476.45) * mm, "end": v(282.6, 476.45) * mm});
            skLineSegment(sketch, "E14.24.3.16", {"start": v(282.6, 476.45) * mm, "end": v(261.86, 462.99) * mm});
            skLineSegment(sketch, "E14.27.3.16", {"start": v(261.86, 462.99) * mm, "end": v(282.6, 449.53) * mm});
            skLineSegment(sketch, "E14.30.3.16", {"start": v(282.6, 449.53) * mm, "end": v(310.97, 449.53) * mm});
            skLineSegment(sketch, "E14.33.3.16", {"start": v(310.97, 449.53) * mm, "end": v(331.71, 462.99) * mm});
            skLineSegment(sketch, "E14.0.4.2", {"start": v(418.37, 58.28) * mm, "end": v(439.1, 71.74) * mm});
            skLineSegment(sketch, "E14.3.4.2", {"start": v(439.1, 71.74) * mm, "end": v(467.48, 71.74) * mm});
            skLineSegment(sketch, "E14.6.4.2", {"start": v(467.48, 71.74) * mm, "end": v(488.22, 58.28) * mm});
            skLineSegment(sketch, "E14.9.4.2", {"start": v(439.1, 44.82) * mm, "end": v(418.37, 58.28) * mm});
            skLineSegment(sketch, "E14.12.4.2", {"start": v(488.22, 58.28) * mm, "end": v(467.48, 44.82) * mm});
            skLineSegment(sketch, "E14.15.4.2", {"start": v(435.84, 43.33) * mm, "end": v(415.1, 56.8) * mm});
            skLineSegment(sketch, "E14.18.4.2", {"start": v(467.48, 44.82) * mm, "end": v(439.1, 44.82) * mm});
            skLineSegment(sketch, "E14.21.4.2", {"start": v(415.1, 56.8) * mm, "end": v(386.73, 56.8) * mm});
            skLineSegment(sketch, "E14.24.4.2", {"start": v(386.73, 56.8) * mm, "end": v(366, 43.33) * mm});
            skLineSegment(sketch, "E14.27.4.2", {"start": v(366, 43.33) * mm, "end": v(386.73, 29.87) * mm});
            skLineSegment(sketch, "E14.30.4.2", {"start": v(386.73, 29.87) * mm, "end": v(415.1, 29.87) * mm});
            skLineSegment(sketch, "E14.33.4.2", {"start": v(415.1, 29.87) * mm, "end": v(435.84, 43.33) * mm});
            skLineSegment(sketch, "E14.0.4.3", {"start": v(418.37, 88.23) * mm, "end": v(439.1, 101.69) * mm});
            skLineSegment(sketch, "E14.3.4.3", {"start": v(439.1, 101.69) * mm, "end": v(467.48, 101.69) * mm});
            skLineSegment(sketch, "E14.6.4.3", {"start": v(467.48, 101.69) * mm, "end": v(488.22, 88.23) * mm});
            skLineSegment(sketch, "E14.9.4.3", {"start": v(439.1, 74.76) * mm, "end": v(418.37, 88.23) * mm});
            skLineSegment(sketch, "E14.12.4.3", {"start": v(488.22, 88.23) * mm, "end": v(467.48, 74.76) * mm});
            skLineSegment(sketch, "E14.15.4.3", {"start": v(435.84, 73.28) * mm, "end": v(415.1, 86.74) * mm});
            skLineSegment(sketch, "E14.18.4.3", {"start": v(467.48, 74.76) * mm, "end": v(439.1, 74.76) * mm});
            skLineSegment(sketch, "E14.21.4.3", {"start": v(415.1, 86.74) * mm, "end": v(386.73, 86.74) * mm});
            skLineSegment(sketch, "E14.24.4.3", {"start": v(386.73, 86.74) * mm, "end": v(366, 73.28) * mm});
            skLineSegment(sketch, "E14.27.4.3", {"start": v(366, 73.28) * mm, "end": v(386.73, 59.82) * mm});
            skLineSegment(sketch, "E14.30.4.3", {"start": v(386.73, 59.82) * mm, "end": v(415.1, 59.82) * mm});
            skLineSegment(sketch, "E14.33.4.3", {"start": v(415.1, 59.82) * mm, "end": v(435.84, 73.28) * mm});
            skLineSegment(sketch, "E14.0.4.4", {"start": v(418.37, 118.17) * mm, "end": v(439.1, 131.63) * mm});
            skLineSegment(sketch, "E14.3.4.4", {"start": v(439.1, 131.63) * mm, "end": v(467.48, 131.63) * mm});
            skLineSegment(sketch, "E14.6.4.4", {"start": v(467.48, 131.63) * mm, "end": v(488.22, 118.17) * mm});
            skLineSegment(sketch, "E14.9.4.4", {"start": v(439.1, 104.71) * mm, "end": v(418.37, 118.17) * mm});
            skLineSegment(sketch, "E14.12.4.4", {"start": v(488.22, 118.17) * mm, "end": v(467.48, 104.71) * mm});
            skLineSegment(sketch, "E14.15.4.4", {"start": v(435.84, 103.23) * mm, "end": v(415.1, 116.69) * mm});
            skLineSegment(sketch, "E14.18.4.4", {"start": v(467.48, 104.71) * mm, "end": v(439.1, 104.71) * mm});
            skLineSegment(sketch, "E14.21.4.4", {"start": v(415.1, 116.69) * mm, "end": v(386.73, 116.69) * mm});
            skLineSegment(sketch, "E14.24.4.4", {"start": v(386.73, 116.69) * mm, "end": v(366, 103.23) * mm});
            skLineSegment(sketch, "E14.27.4.4", {"start": v(366, 103.23) * mm, "end": v(386.73, 89.76) * mm});
            skLineSegment(sketch, "E14.30.4.4", {"start": v(386.73, 89.76) * mm, "end": v(415.1, 89.76) * mm});
            skLineSegment(sketch, "E14.33.4.4", {"start": v(415.1, 89.76) * mm, "end": v(435.84, 103.23) * mm});
            skLineSegment(sketch, "E14.0.4.5", {"start": v(418.37, 148.12) * mm, "end": v(439.1, 161.58) * mm});
            skLineSegment(sketch, "E14.3.4.5", {"start": v(439.1, 161.58) * mm, "end": v(467.48, 161.58) * mm});
            skLineSegment(sketch, "E14.6.4.5", {"start": v(467.48, 161.58) * mm, "end": v(488.22, 148.12) * mm});
            skLineSegment(sketch, "E14.9.4.5", {"start": v(439.1, 134.66) * mm, "end": v(418.37, 148.12) * mm});
            skLineSegment(sketch, "E14.12.4.5", {"start": v(488.22, 148.12) * mm, "end": v(467.48, 134.66) * mm});
            skLineSegment(sketch, "E14.15.4.5", {"start": v(435.84, 133.17) * mm, "end": v(415.1, 146.63) * mm});
            skLineSegment(sketch, "E14.18.4.5", {"start": v(467.48, 134.66) * mm, "end": v(439.1, 134.66) * mm});
            skLineSegment(sketch, "E14.21.4.5", {"start": v(415.1, 146.63) * mm, "end": v(386.73, 146.63) * mm});
            skLineSegment(sketch, "E14.24.4.5", {"start": v(386.73, 146.63) * mm, "end": v(366, 133.17) * mm});
            skLineSegment(sketch, "E14.27.4.5", {"start": v(366, 133.17) * mm, "end": v(386.73, 119.7) * mm});
            skLineSegment(sketch, "E14.30.4.5", {"start": v(386.73, 119.7) * mm, "end": v(415.1, 119.7) * mm});
            skLineSegment(sketch, "E14.33.4.5", {"start": v(415.1, 119.7) * mm, "end": v(435.84, 133.17) * mm});
            skLineSegment(sketch, "E14.0.4.6", {"start": v(418.37, 178.07) * mm, "end": v(439.1, 191.53) * mm});
            skLineSegment(sketch, "E14.3.4.6", {"start": v(439.1, 191.53) * mm, "end": v(467.48, 191.53) * mm});
            skLineSegment(sketch, "E14.6.4.6", {"start": v(467.48, 191.53) * mm, "end": v(488.22, 178.07) * mm});
            skLineSegment(sketch, "E14.9.4.6", {"start": v(439.1, 164.6) * mm, "end": v(418.37, 178.07) * mm});
            skLineSegment(sketch, "E14.12.4.6", {"start": v(488.22, 178.07) * mm, "end": v(467.48, 164.6) * mm});
            skLineSegment(sketch, "E14.15.4.6", {"start": v(435.84, 163.12) * mm, "end": v(415.1, 176.58) * mm});
            skLineSegment(sketch, "E14.18.4.6", {"start": v(467.48, 164.6) * mm, "end": v(439.1, 164.6) * mm});
            skLineSegment(sketch, "E14.21.4.6", {"start": v(415.1, 176.58) * mm, "end": v(386.73, 176.58) * mm});
            skLineSegment(sketch, "E14.24.4.6", {"start": v(386.73, 176.58) * mm, "end": v(366, 163.12) * mm});
            skLineSegment(sketch, "E14.27.4.6", {"start": v(366, 163.12) * mm, "end": v(386.73, 149.66) * mm});
            skLineSegment(sketch, "E14.30.4.6", {"start": v(386.73, 149.66) * mm, "end": v(415.1, 149.66) * mm});
            skLineSegment(sketch, "E14.33.4.6", {"start": v(415.1, 149.66) * mm, "end": v(435.84, 163.12) * mm});
            skLineSegment(sketch, "E14.0.4.7", {"start": v(418.37, 208.01) * mm, "end": v(439.1, 221.47) * mm});
            skLineSegment(sketch, "E14.3.4.7", {"start": v(439.1, 221.47) * mm, "end": v(467.48, 221.47) * mm});
            skLineSegment(sketch, "E14.6.4.7", {"start": v(467.48, 221.47) * mm, "end": v(488.22, 208.01) * mm});
            skLineSegment(sketch, "E14.9.4.7", {"start": v(439.1, 194.55) * mm, "end": v(418.37, 208.01) * mm});
            skLineSegment(sketch, "E14.12.4.7", {"start": v(488.22, 208.01) * mm, "end": v(467.48, 194.55) * mm});
            skLineSegment(sketch, "E14.15.4.7", {"start": v(435.84, 193.07) * mm, "end": v(415.1, 206.53) * mm});
            skLineSegment(sketch, "E14.18.4.7", {"start": v(467.48, 194.55) * mm, "end": v(439.1, 194.55) * mm});
            skLineSegment(sketch, "E14.21.4.7", {"start": v(415.1, 206.53) * mm, "end": v(386.73, 206.53) * mm});
            skLineSegment(sketch, "E14.24.4.7", {"start": v(386.73, 206.53) * mm, "end": v(366, 193.07) * mm});
            skLineSegment(sketch, "E14.27.4.7", {"start": v(366, 193.07) * mm, "end": v(386.73, 179.6) * mm});
            skLineSegment(sketch, "E14.30.4.7", {"start": v(386.73, 179.6) * mm, "end": v(415.1, 179.6) * mm});
            skLineSegment(sketch, "E14.33.4.7", {"start": v(415.1, 179.6) * mm, "end": v(435.84, 193.07) * mm});
            skLineSegment(sketch, "E14.0.4.8", {"start": v(418.37, 237.96) * mm, "end": v(439.1, 251.42) * mm});
            skLineSegment(sketch, "E14.3.4.8", {"start": v(439.1, 251.42) * mm, "end": v(467.48, 251.42) * mm});
            skLineSegment(sketch, "E14.6.4.8", {"start": v(467.48, 251.42) * mm, "end": v(488.22, 237.96) * mm});
            skLineSegment(sketch, "E14.9.4.8", {"start": v(439.1, 224.5) * mm, "end": v(418.37, 237.96) * mm});
            skLineSegment(sketch, "E14.12.4.8", {"start": v(488.22, 237.96) * mm, "end": v(467.48, 224.5) * mm});
            skLineSegment(sketch, "E14.15.4.8", {"start": v(435.84, 223.01) * mm, "end": v(415.1, 236.47) * mm});
            skLineSegment(sketch, "E14.18.4.8", {"start": v(467.48, 224.5) * mm, "end": v(439.1, 224.5) * mm});
            skLineSegment(sketch, "E14.21.4.8", {"start": v(415.1, 236.47) * mm, "end": v(386.73, 236.47) * mm});
            skLineSegment(sketch, "E14.24.4.8", {"start": v(386.73, 236.47) * mm, "end": v(366, 223.01) * mm});
            skLineSegment(sketch, "E14.27.4.8", {"start": v(366, 223.01) * mm, "end": v(386.73, 209.55) * mm});
            skLineSegment(sketch, "E14.30.4.8", {"start": v(386.73, 209.55) * mm, "end": v(415.1, 209.55) * mm});
            skLineSegment(sketch, "E14.33.4.8", {"start": v(415.1, 209.55) * mm, "end": v(435.84, 223.01) * mm});
            skLineSegment(sketch, "E14.0.4.9", {"start": v(418.37, 267.9) * mm, "end": v(439.1, 281.37) * mm});
            skLineSegment(sketch, "E14.3.4.9", {"start": v(439.1, 281.37) * mm, "end": v(467.48, 281.37) * mm});
            skLineSegment(sketch, "E14.6.4.9", {"start": v(467.48, 281.37) * mm, "end": v(488.22, 267.9) * mm});
            skLineSegment(sketch, "E14.9.4.9", {"start": v(439.1, 254.44) * mm, "end": v(418.37, 267.9) * mm});
            skLineSegment(sketch, "E14.12.4.9", {"start": v(488.22, 267.9) * mm, "end": v(467.48, 254.44) * mm});
            skLineSegment(sketch, "E14.15.4.9", {"start": v(435.84, 252.96) * mm, "end": v(415.1, 266.42) * mm});
            skLineSegment(sketch, "E14.18.4.9", {"start": v(467.48, 254.44) * mm, "end": v(439.1, 254.44) * mm});
            skLineSegment(sketch, "E14.21.4.9", {"start": v(415.1, 266.42) * mm, "end": v(386.73, 266.42) * mm});
            skLineSegment(sketch, "E14.24.4.9", {"start": v(386.73, 266.42) * mm, "end": v(366, 252.96) * mm});
            skLineSegment(sketch, "E14.27.4.9", {"start": v(366, 252.96) * mm, "end": v(386.73, 239.5) * mm});
            skLineSegment(sketch, "E14.30.4.9", {"start": v(386.73, 239.5) * mm, "end": v(415.1, 239.5) * mm});
            skLineSegment(sketch, "E14.33.4.9", {"start": v(415.1, 239.5) * mm, "end": v(435.84, 252.96) * mm});
            skLineSegment(sketch, "E14.0.4.10", {"start": v(418.37, 297.85) * mm, "end": v(439.1, 311.31) * mm});
            skLineSegment(sketch, "E14.3.4.10", {"start": v(439.1, 311.31) * mm, "end": v(467.48, 311.31) * mm});
            skLineSegment(sketch, "E14.6.4.10", {"start": v(467.48, 311.31) * mm, "end": v(488.22, 297.85) * mm});
            skLineSegment(sketch, "E14.9.4.10", {"start": v(439.1, 284.4) * mm, "end": v(418.37, 297.85) * mm});
            skLineSegment(sketch, "E14.12.4.10", {"start": v(488.22, 297.85) * mm, "end": v(467.48, 284.4) * mm});
            skLineSegment(sketch, "E14.15.4.10", {"start": v(435.84, 282.9) * mm, "end": v(415.1, 296.37) * mm});
            skLineSegment(sketch, "E14.18.4.10", {"start": v(467.48, 284.4) * mm, "end": v(439.1, 284.4) * mm});
            skLineSegment(sketch, "E14.21.4.10", {"start": v(415.1, 296.37) * mm, "end": v(386.73, 296.37) * mm});
            skLineSegment(sketch, "E14.24.4.10", {"start": v(386.73, 296.37) * mm, "end": v(366, 282.9) * mm});
            skLineSegment(sketch, "E14.27.4.10", {"start": v(366, 282.9) * mm, "end": v(386.73, 269.44) * mm});
            skLineSegment(sketch, "E14.30.4.10", {"start": v(386.73, 269.44) * mm, "end": v(415.1, 269.44) * mm});
            skLineSegment(sketch, "E14.33.4.10", {"start": v(415.1, 269.44) * mm, "end": v(435.84, 282.9) * mm});
            skLineSegment(sketch, "E14.0.4.11", {"start": v(418.37, 327.8) * mm, "end": v(439.1, 341.26) * mm});
            skLineSegment(sketch, "E14.3.4.11", {"start": v(439.1, 341.26) * mm, "end": v(467.48, 341.26) * mm});
            skLineSegment(sketch, "E14.6.4.11", {"start": v(467.48, 341.26) * mm, "end": v(488.22, 327.8) * mm});
            skLineSegment(sketch, "E14.9.4.11", {"start": v(439.1, 314.34) * mm, "end": v(418.37, 327.8) * mm});
            skLineSegment(sketch, "E14.12.4.11", {"start": v(488.22, 327.8) * mm, "end": v(467.48, 314.34) * mm});
            skLineSegment(sketch, "E14.15.4.11", {"start": v(435.84, 312.85) * mm, "end": v(415.1, 326.31) * mm});
            skLineSegment(sketch, "E14.18.4.11", {"start": v(467.48, 314.34) * mm, "end": v(439.1, 314.34) * mm});
            skLineSegment(sketch, "E14.21.4.11", {"start": v(415.1, 326.31) * mm, "end": v(386.73, 326.31) * mm});
            skLineSegment(sketch, "E14.24.4.11", {"start": v(386.73, 326.31) * mm, "end": v(366, 312.85) * mm});
            skLineSegment(sketch, "E14.27.4.11", {"start": v(366, 312.85) * mm, "end": v(386.73, 299.39) * mm});
            skLineSegment(sketch, "E14.30.4.11", {"start": v(386.73, 299.39) * mm, "end": v(415.1, 299.39) * mm});
            skLineSegment(sketch, "E14.33.4.11", {"start": v(415.1, 299.39) * mm, "end": v(435.84, 312.85) * mm});
            skLineSegment(sketch, "E14.0.4.12", {"start": v(418.37, 357.75) * mm, "end": v(439.1, 371.2) * mm});
            skLineSegment(sketch, "E14.3.4.12", {"start": v(439.1, 371.2) * mm, "end": v(467.48, 371.2) * mm});
            skLineSegment(sketch, "E14.6.4.12", {"start": v(467.48, 371.2) * mm, "end": v(488.22, 357.75) * mm});
            skLineSegment(sketch, "E14.9.4.12", {"start": v(439.1, 344.28) * mm, "end": v(418.37, 357.75) * mm});
            skLineSegment(sketch, "E14.12.4.12", {"start": v(488.22, 357.75) * mm, "end": v(467.48, 344.28) * mm});
            skLineSegment(sketch, "E14.15.4.12", {"start": v(435.84, 342.8) * mm, "end": v(415.1, 356.26) * mm});
            skLineSegment(sketch, "E14.18.4.12", {"start": v(467.48, 344.28) * mm, "end": v(439.1, 344.28) * mm});
            skLineSegment(sketch, "E14.21.4.12", {"start": v(415.1, 356.26) * mm, "end": v(386.73, 356.26) * mm});
            skLineSegment(sketch, "E14.24.4.12", {"start": v(386.73, 356.26) * mm, "end": v(366, 342.8) * mm});
            skLineSegment(sketch, "E14.27.4.12", {"start": v(366, 342.8) * mm, "end": v(386.73, 329.34) * mm});
            skLineSegment(sketch, "E14.30.4.12", {"start": v(386.73, 329.34) * mm, "end": v(415.1, 329.34) * mm});
            skLineSegment(sketch, "E14.33.4.12", {"start": v(415.1, 329.34) * mm, "end": v(435.84, 342.8) * mm});
            skLineSegment(sketch, "E14.0.4.13", {"start": v(418.37, 387.7) * mm, "end": v(439.1, 401.15) * mm});
            skLineSegment(sketch, "E14.3.4.13", {"start": v(439.1, 401.15) * mm, "end": v(467.48, 401.15) * mm});
            skLineSegment(sketch, "E14.6.4.13", {"start": v(467.48, 401.15) * mm, "end": v(488.22, 387.7) * mm});
            skLineSegment(sketch, "E14.9.4.13", {"start": v(439.1, 374.23) * mm, "end": v(418.37, 387.7) * mm});
            skLineSegment(sketch, "E14.12.4.13", {"start": v(488.22, 387.7) * mm, "end": v(467.48, 374.23) * mm});
            skLineSegment(sketch, "E14.15.4.13", {"start": v(435.84, 372.74) * mm, "end": v(415.1, 386.2) * mm});
            skLineSegment(sketch, "E14.18.4.13", {"start": v(467.48, 374.23) * mm, "end": v(439.1, 374.23) * mm});
            skLineSegment(sketch, "E14.21.4.13", {"start": v(415.1, 386.2) * mm, "end": v(386.73, 386.2) * mm});
            skLineSegment(sketch, "E14.24.4.13", {"start": v(386.73, 386.2) * mm, "end": v(366, 372.74) * mm});
            skLineSegment(sketch, "E14.27.4.13", {"start": v(366, 372.74) * mm, "end": v(386.73, 359.28) * mm});
            skLineSegment(sketch, "E14.30.4.13", {"start": v(386.73, 359.28) * mm, "end": v(415.1, 359.28) * mm});
            skLineSegment(sketch, "E14.33.4.13", {"start": v(415.1, 359.28) * mm, "end": v(435.84, 372.74) * mm});
            skLineSegment(sketch, "E14.0.4.14", {"start": v(418.37, 417.64) * mm, "end": v(439.1, 431.1) * mm});
            skLineSegment(sketch, "E14.3.4.14", {"start": v(439.1, 431.1) * mm, "end": v(467.48, 431.1) * mm});
            skLineSegment(sketch, "E14.6.4.14", {"start": v(467.48, 431.1) * mm, "end": v(488.22, 417.64) * mm});
            skLineSegment(sketch, "E14.9.4.14", {"start": v(439.1, 404.18) * mm, "end": v(418.37, 417.64) * mm});
            skLineSegment(sketch, "E14.12.4.14", {"start": v(488.22, 417.64) * mm, "end": v(467.48, 404.18) * mm});
            skLineSegment(sketch, "E14.15.4.14", {"start": v(435.84, 402.7) * mm, "end": v(415.1, 416.15) * mm});
            skLineSegment(sketch, "E14.18.4.14", {"start": v(467.48, 404.18) * mm, "end": v(439.1, 404.18) * mm});
            skLineSegment(sketch, "E14.21.4.14", {"start": v(415.1, 416.15) * mm, "end": v(386.73, 416.15) * mm});
            skLineSegment(sketch, "E14.24.4.14", {"start": v(386.73, 416.15) * mm, "end": v(366, 402.7) * mm});
            skLineSegment(sketch, "E14.27.4.14", {"start": v(366, 402.7) * mm, "end": v(386.73, 389.23) * mm});
            skLineSegment(sketch, "E14.30.4.14", {"start": v(386.73, 389.23) * mm, "end": v(415.1, 389.23) * mm});
            skLineSegment(sketch, "E14.33.4.14", {"start": v(415.1, 389.23) * mm, "end": v(435.84, 402.7) * mm});
            skLineSegment(sketch, "E14.0.4.15", {"start": v(418.37, 447.59) * mm, "end": v(439.1, 461.05) * mm});
            skLineSegment(sketch, "E14.3.4.15", {"start": v(439.1, 461.05) * mm, "end": v(467.48, 461.05) * mm});
            skLineSegment(sketch, "E14.6.4.15", {"start": v(467.48, 461.05) * mm, "end": v(488.22, 447.59) * mm});
            skLineSegment(sketch, "E14.9.4.15", {"start": v(439.1, 434.12) * mm, "end": v(418.37, 447.59) * mm});
            skLineSegment(sketch, "E14.12.4.15", {"start": v(488.22, 447.59) * mm, "end": v(467.48, 434.12) * mm});
            skLineSegment(sketch, "E14.15.4.15", {"start": v(435.84, 432.64) * mm, "end": v(415.1, 446.1) * mm});
            skLineSegment(sketch, "E14.18.4.15", {"start": v(467.48, 434.12) * mm, "end": v(439.1, 434.12) * mm});
            skLineSegment(sketch, "E14.21.4.15", {"start": v(415.1, 446.1) * mm, "end": v(386.73, 446.1) * mm});
            skLineSegment(sketch, "E14.24.4.15", {"start": v(386.73, 446.1) * mm, "end": v(366, 432.64) * mm});
            skLineSegment(sketch, "E14.27.4.15", {"start": v(366, 432.64) * mm, "end": v(386.73, 419.18) * mm});
            skLineSegment(sketch, "E14.30.4.15", {"start": v(386.73, 419.18) * mm, "end": v(415.1, 419.18) * mm});
            skLineSegment(sketch, "E14.33.4.15", {"start": v(415.1, 419.18) * mm, "end": v(435.84, 432.64) * mm});
            skLineSegment(sketch, "E14.0.4.16", {"start": v(418.37, 477.53) * mm, "end": v(439.1, 491) * mm});
            skLineSegment(sketch, "E14.3.4.16", {"start": v(439.1, 491) * mm, "end": v(467.48, 491) * mm});
            skLineSegment(sketch, "E14.6.4.16", {"start": v(467.48, 491) * mm, "end": v(488.22, 477.53) * mm});
            skLineSegment(sketch, "E14.9.4.16", {"start": v(439.1, 464.07) * mm, "end": v(418.37, 477.53) * mm});
            skLineSegment(sketch, "E14.12.4.16", {"start": v(488.22, 477.53) * mm, "end": v(467.48, 464.07) * mm});
            skLineSegment(sketch, "E14.15.4.16", {"start": v(435.84, 462.58) * mm, "end": v(415.1, 476.05) * mm});
            skLineSegment(sketch, "E14.18.4.16", {"start": v(467.48, 464.07) * mm, "end": v(439.1, 464.07) * mm});
            skLineSegment(sketch, "E14.21.4.16", {"start": v(415.1, 476.05) * mm, "end": v(386.73, 476.05) * mm});
            skLineSegment(sketch, "E14.24.4.16", {"start": v(386.73, 476.05) * mm, "end": v(366, 462.58) * mm});
            skLineSegment(sketch, "E14.27.4.16", {"start": v(366, 462.58) * mm, "end": v(386.73, 449.12) * mm});
            skLineSegment(sketch, "E14.30.4.16", {"start": v(386.73, 449.12) * mm, "end": v(415.1, 449.12) * mm});
            skLineSegment(sketch, "E14.33.4.16", {"start": v(415.1, 449.12) * mm, "end": v(435.84, 462.58) * mm});
            skLineSegment(sketch, "E14.0.5.2", {"start": v(522.5, 57.88) * mm, "end": v(543.23, 71.34) * mm});
            skLineSegment(sketch, "E14.3.5.2", {"start": v(543.23, 71.34) * mm, "end": v(571.6, 71.34) * mm});
            skLineSegment(sketch, "E14.6.5.2", {"start": v(571.6, 71.34) * mm, "end": v(592.34, 57.88) * mm});
            skLineSegment(sketch, "E14.9.5.2", {"start": v(543.23, 44.41) * mm, "end": v(522.5, 57.88) * mm});
            skLineSegment(sketch, "E14.12.5.2", {"start": v(592.34, 57.88) * mm, "end": v(571.6, 44.41) * mm});
            skLineSegment(sketch, "E14.15.5.2", {"start": v(539.97, 42.93) * mm, "end": v(519.23, 56.4) * mm});
            skLineSegment(sketch, "E14.18.5.2", {"start": v(571.6, 44.41) * mm, "end": v(543.23, 44.41) * mm});
            skLineSegment(sketch, "E14.21.5.2", {"start": v(519.23, 56.4) * mm, "end": v(490.86, 56.4) * mm});
            skLineSegment(sketch, "E14.24.5.2", {"start": v(490.86, 56.4) * mm, "end": v(470.12, 42.93) * mm});
            skLineSegment(sketch, "E14.27.5.2", {"start": v(470.12, 42.93) * mm, "end": v(490.86, 29.47) * mm});
            skLineSegment(sketch, "E14.30.5.2", {"start": v(490.86, 29.47) * mm, "end": v(519.23, 29.47) * mm});
            skLineSegment(sketch, "E14.33.5.2", {"start": v(519.23, 29.47) * mm, "end": v(539.97, 42.93) * mm});
            skLineSegment(sketch, "E14.0.5.3", {"start": v(522.5, 87.82) * mm, "end": v(543.23, 101.28) * mm});
            skLineSegment(sketch, "E14.3.5.3", {"start": v(543.23, 101.28) * mm, "end": v(571.6, 101.28) * mm});
            skLineSegment(sketch, "E14.6.5.3", {"start": v(571.6, 101.28) * mm, "end": v(592.34, 87.82) * mm});
            skLineSegment(sketch, "E14.9.5.3", {"start": v(543.23, 74.36) * mm, "end": v(522.5, 87.82) * mm});
            skLineSegment(sketch, "E14.12.5.3", {"start": v(592.34, 87.82) * mm, "end": v(571.6, 74.36) * mm});
            skLineSegment(sketch, "E14.15.5.3", {"start": v(539.97, 72.88) * mm, "end": v(519.23, 86.34) * mm});
            skLineSegment(sketch, "E14.18.5.3", {"start": v(571.6, 74.36) * mm, "end": v(543.23, 74.36) * mm});
            skLineSegment(sketch, "E14.21.5.3", {"start": v(519.23, 86.34) * mm, "end": v(490.86, 86.34) * mm});
            skLineSegment(sketch, "E14.24.5.3", {"start": v(490.86, 86.34) * mm, "end": v(470.12, 72.88) * mm});
            skLineSegment(sketch, "E14.27.5.3", {"start": v(470.12, 72.88) * mm, "end": v(490.86, 59.41) * mm});
            skLineSegment(sketch, "E14.30.5.3", {"start": v(490.86, 59.41) * mm, "end": v(519.23, 59.41) * mm});
            skLineSegment(sketch, "E14.33.5.3", {"start": v(519.23, 59.41) * mm, "end": v(539.97, 72.88) * mm});
            skLineSegment(sketch, "E14.0.5.4", {"start": v(522.5, 117.77) * mm, "end": v(543.23, 131.23) * mm});
            skLineSegment(sketch, "E14.3.5.4", {"start": v(543.23, 131.23) * mm, "end": v(571.6, 131.23) * mm});
            skLineSegment(sketch, "E14.6.5.4", {"start": v(571.6, 131.23) * mm, "end": v(592.34, 117.77) * mm});
            skLineSegment(sketch, "E14.9.5.4", {"start": v(543.23, 104.3) * mm, "end": v(522.5, 117.77) * mm});
            skLineSegment(sketch, "E14.12.5.4", {"start": v(592.34, 117.77) * mm, "end": v(571.6, 104.3) * mm});
            skLineSegment(sketch, "E14.15.5.4", {"start": v(539.97, 102.82) * mm, "end": v(519.23, 116.28) * mm});
            skLineSegment(sketch, "E14.18.5.4", {"start": v(571.6, 104.3) * mm, "end": v(543.23, 104.3) * mm});
            skLineSegment(sketch, "E14.21.5.4", {"start": v(519.23, 116.28) * mm, "end": v(490.86, 116.28) * mm});
            skLineSegment(sketch, "E14.24.5.4", {"start": v(490.86, 116.28) * mm, "end": v(470.12, 102.82) * mm});
            skLineSegment(sketch, "E14.27.5.4", {"start": v(470.12, 102.82) * mm, "end": v(490.86, 89.36) * mm});
            skLineSegment(sketch, "E14.30.5.4", {"start": v(490.86, 89.36) * mm, "end": v(519.23, 89.36) * mm});
            skLineSegment(sketch, "E14.33.5.4", {"start": v(519.23, 89.36) * mm, "end": v(539.97, 102.82) * mm});
            skLineSegment(sketch, "E14.0.5.5", {"start": v(522.5, 147.72) * mm, "end": v(543.23, 161.18) * mm});
            skLineSegment(sketch, "E14.3.5.5", {"start": v(543.23, 161.18) * mm, "end": v(571.6, 161.18) * mm});
            skLineSegment(sketch, "E14.6.5.5", {"start": v(571.6, 161.18) * mm, "end": v(592.34, 147.72) * mm});
            skLineSegment(sketch, "E14.9.5.5", {"start": v(543.23, 134.25) * mm, "end": v(522.5, 147.72) * mm});
            skLineSegment(sketch, "E14.12.5.5", {"start": v(592.34, 147.72) * mm, "end": v(571.6, 134.25) * mm});
            skLineSegment(sketch, "E14.15.5.5", {"start": v(539.97, 132.77) * mm, "end": v(519.23, 146.23) * mm});
            skLineSegment(sketch, "E14.18.5.5", {"start": v(571.6, 134.25) * mm, "end": v(543.23, 134.25) * mm});
            skLineSegment(sketch, "E14.21.5.5", {"start": v(519.23, 146.23) * mm, "end": v(490.86, 146.23) * mm});
            skLineSegment(sketch, "E14.24.5.5", {"start": v(490.86, 146.23) * mm, "end": v(470.12, 132.77) * mm});
            skLineSegment(sketch, "E14.27.5.5", {"start": v(470.12, 132.77) * mm, "end": v(490.86, 119.3) * mm});
            skLineSegment(sketch, "E14.30.5.5", {"start": v(490.86, 119.3) * mm, "end": v(519.23, 119.3) * mm});
            skLineSegment(sketch, "E14.33.5.5", {"start": v(519.23, 119.3) * mm, "end": v(539.97, 132.77) * mm});
            skLineSegment(sketch, "E14.0.5.6", {"start": v(522.5, 177.66) * mm, "end": v(543.23, 191.12) * mm});
            skLineSegment(sketch, "E14.3.5.6", {"start": v(543.23, 191.12) * mm, "end": v(571.6, 191.12) * mm});
            skLineSegment(sketch, "E14.6.5.6", {"start": v(571.6, 191.12) * mm, "end": v(592.34, 177.66) * mm});
            skLineSegment(sketch, "E14.9.5.6", {"start": v(543.23, 164.2) * mm, "end": v(522.5, 177.66) * mm});
            skLineSegment(sketch, "E14.12.5.6", {"start": v(592.34, 177.66) * mm, "end": v(571.6, 164.2) * mm});
            skLineSegment(sketch, "E14.15.5.6", {"start": v(539.97, 162.72) * mm, "end": v(519.23, 176.18) * mm});
            skLineSegment(sketch, "E14.18.5.6", {"start": v(571.6, 164.2) * mm, "end": v(543.23, 164.2) * mm});
            skLineSegment(sketch, "E14.21.5.6", {"start": v(519.23, 176.18) * mm, "end": v(490.86, 176.18) * mm});
            skLineSegment(sketch, "E14.24.5.6", {"start": v(490.86, 176.18) * mm, "end": v(470.12, 162.72) * mm});
            skLineSegment(sketch, "E14.27.5.6", {"start": v(470.12, 162.72) * mm, "end": v(490.86, 149.25) * mm});
            skLineSegment(sketch, "E14.30.5.6", {"start": v(490.86, 149.25) * mm, "end": v(519.23, 149.25) * mm});
            skLineSegment(sketch, "E14.33.5.6", {"start": v(519.23, 149.25) * mm, "end": v(539.97, 162.72) * mm});
            skLineSegment(sketch, "E14.0.5.7", {"start": v(522.5, 207.6) * mm, "end": v(543.23, 221.07) * mm});
            skLineSegment(sketch, "E14.3.5.7", {"start": v(543.23, 221.07) * mm, "end": v(571.6, 221.07) * mm});
            skLineSegment(sketch, "E14.6.5.7", {"start": v(571.6, 221.07) * mm, "end": v(592.34, 207.6) * mm});
            skLineSegment(sketch, "E14.9.5.7", {"start": v(543.23, 194.15) * mm, "end": v(522.5, 207.6) * mm});
            skLineSegment(sketch, "E14.12.5.7", {"start": v(592.34, 207.6) * mm, "end": v(571.6, 194.15) * mm});
            skLineSegment(sketch, "E14.15.5.7", {"start": v(539.97, 192.66) * mm, "end": v(519.23, 206.12) * mm});
            skLineSegment(sketch, "E14.18.5.7", {"start": v(571.6, 194.15) * mm, "end": v(543.23, 194.15) * mm});
            skLineSegment(sketch, "E14.21.5.7", {"start": v(519.23, 206.12) * mm, "end": v(490.86, 206.12) * mm});
            skLineSegment(sketch, "E14.24.5.7", {"start": v(490.86, 206.12) * mm, "end": v(470.12, 192.66) * mm});
            skLineSegment(sketch, "E14.27.5.7", {"start": v(470.12, 192.66) * mm, "end": v(490.86, 179.2) * mm});
            skLineSegment(sketch, "E14.30.5.7", {"start": v(490.86, 179.2) * mm, "end": v(519.23, 179.2) * mm});
            skLineSegment(sketch, "E14.33.5.7", {"start": v(519.23, 179.2) * mm, "end": v(539.97, 192.66) * mm});
            skLineSegment(sketch, "E14.0.5.8", {"start": v(522.5, 237.56) * mm, "end": v(543.23, 251.02) * mm});
            skLineSegment(sketch, "E14.3.5.8", {"start": v(543.23, 251.02) * mm, "end": v(571.6, 251.02) * mm});
            skLineSegment(sketch, "E14.6.5.8", {"start": v(571.6, 251.02) * mm, "end": v(592.34, 237.56) * mm});
            skLineSegment(sketch, "E14.9.5.8", {"start": v(543.23, 224.1) * mm, "end": v(522.5, 237.56) * mm});
            skLineSegment(sketch, "E14.12.5.8", {"start": v(592.34, 237.56) * mm, "end": v(571.6, 224.1) * mm});
            skLineSegment(sketch, "E14.15.5.8", {"start": v(539.97, 222.6) * mm, "end": v(519.23, 236.07) * mm});
            skLineSegment(sketch, "E14.18.5.8", {"start": v(571.6, 224.1) * mm, "end": v(543.23, 224.1) * mm});
            skLineSegment(sketch, "E14.21.5.8", {"start": v(519.23, 236.07) * mm, "end": v(490.86, 236.07) * mm});
            skLineSegment(sketch, "E14.24.5.8", {"start": v(490.86, 236.07) * mm, "end": v(470.12, 222.6) * mm});
            skLineSegment(sketch, "E14.27.5.8", {"start": v(470.12, 222.6) * mm, "end": v(490.86, 209.15) * mm});
            skLineSegment(sketch, "E14.30.5.8", {"start": v(490.86, 209.15) * mm, "end": v(519.23, 209.15) * mm});
            skLineSegment(sketch, "E14.33.5.8", {"start": v(519.23, 209.15) * mm, "end": v(539.97, 222.6) * mm});
            skLineSegment(sketch, "E14.0.5.9", {"start": v(522.5, 267.5) * mm, "end": v(543.23, 280.96) * mm});
            skLineSegment(sketch, "E14.3.5.9", {"start": v(543.23, 280.96) * mm, "end": v(571.6, 280.96) * mm});
            skLineSegment(sketch, "E14.6.5.9", {"start": v(571.6, 280.96) * mm, "end": v(592.34, 267.5) * mm});
            skLineSegment(sketch, "E14.9.5.9", {"start": v(543.23, 254.04) * mm, "end": v(522.5, 267.5) * mm});
            skLineSegment(sketch, "E14.12.5.9", {"start": v(592.34, 267.5) * mm, "end": v(571.6, 254.04) * mm});
            skLineSegment(sketch, "E14.15.5.9", {"start": v(539.97, 252.55) * mm, "end": v(519.23, 266.02) * mm});
            skLineSegment(sketch, "E14.18.5.9", {"start": v(571.6, 254.04) * mm, "end": v(543.23, 254.04) * mm});
            skLineSegment(sketch, "E14.21.5.9", {"start": v(519.23, 266.02) * mm, "end": v(490.86, 266.02) * mm});
            skLineSegment(sketch, "E14.24.5.9", {"start": v(490.86, 266.02) * mm, "end": v(470.12, 252.55) * mm});
            skLineSegment(sketch, "E14.27.5.9", {"start": v(470.12, 252.55) * mm, "end": v(490.86, 239.1) * mm});
            skLineSegment(sketch, "E14.30.5.9", {"start": v(490.86, 239.1) * mm, "end": v(519.23, 239.1) * mm});
            skLineSegment(sketch, "E14.33.5.9", {"start": v(519.23, 239.1) * mm, "end": v(539.97, 252.55) * mm});
            skLineSegment(sketch, "E14.0.5.10", {"start": v(522.5, 297.45) * mm, "end": v(543.23, 310.91) * mm});
            skLineSegment(sketch, "E14.3.5.10", {"start": v(543.23, 310.91) * mm, "end": v(571.6, 310.91) * mm});
            skLineSegment(sketch, "E14.6.5.10", {"start": v(571.6, 310.91) * mm, "end": v(592.34, 297.45) * mm});
            skLineSegment(sketch, "E14.9.5.10", {"start": v(543.23, 283.99) * mm, "end": v(522.5, 297.45) * mm});
            skLineSegment(sketch, "E14.12.5.10", {"start": v(592.34, 297.45) * mm, "end": v(571.6, 283.99) * mm});
            skLineSegment(sketch, "E14.15.5.10", {"start": v(539.97, 282.5) * mm, "end": v(519.23, 295.96) * mm});
            skLineSegment(sketch, "E14.18.5.10", {"start": v(571.6, 283.99) * mm, "end": v(543.23, 283.99) * mm});
            skLineSegment(sketch, "E14.21.5.10", {"start": v(519.23, 295.96) * mm, "end": v(490.86, 295.96) * mm});
            skLineSegment(sketch, "E14.24.5.10", {"start": v(490.86, 295.96) * mm, "end": v(470.12, 282.5) * mm});
            skLineSegment(sketch, "E14.27.5.10", {"start": v(470.12, 282.5) * mm, "end": v(490.86, 269.04) * mm});
            skLineSegment(sketch, "E14.30.5.10", {"start": v(490.86, 269.04) * mm, "end": v(519.23, 269.04) * mm});
            skLineSegment(sketch, "E14.33.5.10", {"start": v(519.23, 269.04) * mm, "end": v(539.97, 282.5) * mm});
            skLineSegment(sketch, "E14.0.5.11", {"start": v(522.5, 327.4) * mm, "end": v(543.23, 340.86) * mm});
            skLineSegment(sketch, "E14.3.5.11", {"start": v(543.23, 340.86) * mm, "end": v(571.6, 340.86) * mm});
            skLineSegment(sketch, "E14.6.5.11", {"start": v(571.6, 340.86) * mm, "end": v(592.34, 327.4) * mm});
            skLineSegment(sketch, "E14.9.5.11", {"start": v(543.23, 313.93) * mm, "end": v(522.5, 327.4) * mm});
            skLineSegment(sketch, "E14.12.5.11", {"start": v(592.34, 327.4) * mm, "end": v(571.6, 313.93) * mm});
            skLineSegment(sketch, "E14.15.5.11", {"start": v(539.97, 312.45) * mm, "end": v(519.23, 325.91) * mm});
            skLineSegment(sketch, "E14.18.5.11", {"start": v(571.6, 313.93) * mm, "end": v(543.23, 313.93) * mm});
            skLineSegment(sketch, "E14.21.5.11", {"start": v(519.23, 325.91) * mm, "end": v(490.86, 325.91) * mm});
            skLineSegment(sketch, "E14.24.5.11", {"start": v(490.86, 325.91) * mm, "end": v(470.12, 312.45) * mm});
            skLineSegment(sketch, "E14.27.5.11", {"start": v(470.12, 312.45) * mm, "end": v(490.86, 298.99) * mm});
            skLineSegment(sketch, "E14.30.5.11", {"start": v(490.86, 298.99) * mm, "end": v(519.23, 298.99) * mm});
            skLineSegment(sketch, "E14.33.5.11", {"start": v(519.23, 298.99) * mm, "end": v(539.97, 312.45) * mm});
            skLineSegment(sketch, "E14.0.5.12", {"start": v(522.5, 357.34) * mm, "end": v(543.23, 370.8) * mm});
            skLineSegment(sketch, "E14.3.5.12", {"start": v(543.23, 370.8) * mm, "end": v(571.6, 370.8) * mm});
            skLineSegment(sketch, "E14.6.5.12", {"start": v(571.6, 370.8) * mm, "end": v(592.34, 357.34) * mm});
            skLineSegment(sketch, "E14.9.5.12", {"start": v(543.23, 343.88) * mm, "end": v(522.5, 357.34) * mm});
            skLineSegment(sketch, "E14.12.5.12", {"start": v(592.34, 357.34) * mm, "end": v(571.6, 343.88) * mm});
            skLineSegment(sketch, "E14.15.5.12", {"start": v(539.97, 342.4) * mm, "end": v(519.23, 355.86) * mm});
            skLineSegment(sketch, "E14.18.5.12", {"start": v(571.6, 343.88) * mm, "end": v(543.23, 343.88) * mm});
            skLineSegment(sketch, "E14.21.5.12", {"start": v(519.23, 355.86) * mm, "end": v(490.86, 355.86) * mm});
            skLineSegment(sketch, "E14.24.5.12", {"start": v(490.86, 355.86) * mm, "end": v(470.12, 342.4) * mm});
            skLineSegment(sketch, "E14.27.5.12", {"start": v(470.12, 342.4) * mm, "end": v(490.86, 328.93) * mm});
            skLineSegment(sketch, "E14.30.5.12", {"start": v(490.86, 328.93) * mm, "end": v(519.23, 328.93) * mm});
            skLineSegment(sketch, "E14.33.5.12", {"start": v(519.23, 328.93) * mm, "end": v(539.97, 342.4) * mm});
            skLineSegment(sketch, "E14.0.5.13", {"start": v(522.5, 387.29) * mm, "end": v(543.23, 400.75) * mm});
            skLineSegment(sketch, "E14.3.5.13", {"start": v(543.23, 400.75) * mm, "end": v(571.6, 400.75) * mm});
            skLineSegment(sketch, "E14.6.5.13", {"start": v(571.6, 400.75) * mm, "end": v(592.34, 387.29) * mm});
            skLineSegment(sketch, "E14.9.5.13", {"start": v(543.23, 373.83) * mm, "end": v(522.5, 387.29) * mm});
            skLineSegment(sketch, "E14.12.5.13", {"start": v(592.34, 387.29) * mm, "end": v(571.6, 373.83) * mm});
            skLineSegment(sketch, "E14.15.5.13", {"start": v(539.97, 372.34) * mm, "end": v(519.23, 385.8) * mm});
            skLineSegment(sketch, "E14.18.5.13", {"start": v(571.6, 373.83) * mm, "end": v(543.23, 373.83) * mm});
            skLineSegment(sketch, "E14.21.5.13", {"start": v(519.23, 385.8) * mm, "end": v(490.86, 385.8) * mm});
            skLineSegment(sketch, "E14.24.5.13", {"start": v(490.86, 385.8) * mm, "end": v(470.12, 372.34) * mm});
            skLineSegment(sketch, "E14.27.5.13", {"start": v(470.12, 372.34) * mm, "end": v(490.86, 358.88) * mm});
            skLineSegment(sketch, "E14.30.5.13", {"start": v(490.86, 358.88) * mm, "end": v(519.23, 358.88) * mm});
            skLineSegment(sketch, "E14.33.5.13", {"start": v(519.23, 358.88) * mm, "end": v(539.97, 372.34) * mm});
            skLineSegment(sketch, "E14.0.5.14", {"start": v(522.5, 417.24) * mm, "end": v(543.23, 430.7) * mm});
            skLineSegment(sketch, "E14.3.5.14", {"start": v(543.23, 430.7) * mm, "end": v(571.6, 430.7) * mm});
            skLineSegment(sketch, "E14.6.5.14", {"start": v(571.6, 430.7) * mm, "end": v(592.34, 417.24) * mm});
            skLineSegment(sketch, "E14.9.5.14", {"start": v(543.23, 403.77) * mm, "end": v(522.5, 417.24) * mm});
            skLineSegment(sketch, "E14.12.5.14", {"start": v(592.34, 417.24) * mm, "end": v(571.6, 403.77) * mm});
            skLineSegment(sketch, "E14.15.5.14", {"start": v(539.97, 402.29) * mm, "end": v(519.23, 415.75) * mm});
            skLineSegment(sketch, "E14.18.5.14", {"start": v(571.6, 403.77) * mm, "end": v(543.23, 403.77) * mm});
            skLineSegment(sketch, "E14.21.5.14", {"start": v(519.23, 415.75) * mm, "end": v(490.86, 415.75) * mm});
            skLineSegment(sketch, "E14.24.5.14", {"start": v(490.86, 415.75) * mm, "end": v(470.12, 402.29) * mm});
            skLineSegment(sketch, "E14.27.5.14", {"start": v(470.12, 402.29) * mm, "end": v(490.86, 388.83) * mm});
            skLineSegment(sketch, "E14.30.5.14", {"start": v(490.86, 388.83) * mm, "end": v(519.23, 388.83) * mm});
            skLineSegment(sketch, "E14.33.5.14", {"start": v(519.23, 388.83) * mm, "end": v(539.97, 402.29) * mm});
            skLineSegment(sketch, "E14.0.5.15", {"start": v(522.5, 447.18) * mm, "end": v(543.23, 460.64) * mm});
            skLineSegment(sketch, "E14.3.5.15", {"start": v(543.23, 460.64) * mm, "end": v(571.6, 460.64) * mm});
            skLineSegment(sketch, "E14.6.5.15", {"start": v(571.6, 460.64) * mm, "end": v(592.34, 447.18) * mm});
            skLineSegment(sketch, "E14.9.5.15", {"start": v(543.23, 433.72) * mm, "end": v(522.5, 447.18) * mm});
            skLineSegment(sketch, "E14.12.5.15", {"start": v(592.34, 447.18) * mm, "end": v(571.6, 433.72) * mm});
            skLineSegment(sketch, "E14.15.5.15", {"start": v(539.97, 432.23) * mm, "end": v(519.23, 445.7) * mm});
            skLineSegment(sketch, "E14.18.5.15", {"start": v(571.6, 433.72) * mm, "end": v(543.23, 433.72) * mm});
            skLineSegment(sketch, "E14.21.5.15", {"start": v(519.23, 445.7) * mm, "end": v(490.86, 445.7) * mm});
            skLineSegment(sketch, "E14.24.5.15", {"start": v(490.86, 445.7) * mm, "end": v(470.12, 432.23) * mm});
            skLineSegment(sketch, "E14.27.5.15", {"start": v(470.12, 432.23) * mm, "end": v(490.86, 418.77) * mm});
            skLineSegment(sketch, "E14.30.5.15", {"start": v(490.86, 418.77) * mm, "end": v(519.23, 418.77) * mm});
            skLineSegment(sketch, "E14.33.5.15", {"start": v(519.23, 418.77) * mm, "end": v(539.97, 432.23) * mm});
            skLineSegment(sketch, "E14.0.5.16", {"start": v(522.5, 477.13) * mm, "end": v(543.23, 490.6) * mm});
            skLineSegment(sketch, "E14.3.5.16", {"start": v(543.23, 490.6) * mm, "end": v(571.6, 490.6) * mm});
            skLineSegment(sketch, "E14.6.5.16", {"start": v(571.6, 490.6) * mm, "end": v(592.34, 477.13) * mm});
            skLineSegment(sketch, "E14.9.5.16", {"start": v(543.23, 463.67) * mm, "end": v(522.5, 477.13) * mm});
            skLineSegment(sketch, "E14.12.5.16", {"start": v(592.34, 477.13) * mm, "end": v(571.6, 463.67) * mm});
            skLineSegment(sketch, "E14.15.5.16", {"start": v(539.97, 462.18) * mm, "end": v(519.23, 475.64) * mm});
            skLineSegment(sketch, "E14.18.5.16", {"start": v(571.6, 463.67) * mm, "end": v(543.23, 463.67) * mm});
            skLineSegment(sketch, "E14.21.5.16", {"start": v(519.23, 475.64) * mm, "end": v(490.86, 475.64) * mm});
            skLineSegment(sketch, "E14.24.5.16", {"start": v(490.86, 475.64) * mm, "end": v(470.12, 462.18) * mm});
            skLineSegment(sketch, "E14.27.5.16", {"start": v(470.12, 462.18) * mm, "end": v(490.86, 448.72) * mm});
            skLineSegment(sketch, "E14.30.5.16", {"start": v(490.86, 448.72) * mm, "end": v(519.23, 448.72) * mm});
            skLineSegment(sketch, "E14.33.5.16", {"start": v(519.23, 448.72) * mm, "end": v(539.97, 462.18) * mm});
            skLineSegment(sketch, "E14.0.6.2", {"start": v(626.62, 57.47) * mm, "end": v(647.36, 70.93) * mm});
            skLineSegment(sketch, "E14.3.6.2", {"start": v(647.36, 70.93) * mm, "end": v(675.73, 70.93) * mm});
            skLineSegment(sketch, "E14.6.6.2", {"start": v(675.73, 70.93) * mm, "end": v(696.47, 57.47) * mm});
            skLineSegment(sketch, "E14.9.6.2", {"start": v(647.36, 44.01) * mm, "end": v(626.62, 57.47) * mm});
            skLineSegment(sketch, "E14.12.6.2", {"start": v(696.47, 57.47) * mm, "end": v(675.73, 44.01) * mm});
            skLineSegment(sketch, "E14.15.6.2", {"start": v(644.1, 42.53) * mm, "end": v(623.36, 55.99) * mm});
            skLineSegment(sketch, "E14.18.6.2", {"start": v(675.73, 44.01) * mm, "end": v(647.36, 44.01) * mm});
            skLineSegment(sketch, "E14.21.6.2", {"start": v(623.36, 55.99) * mm, "end": v(594.99, 55.99) * mm});
            skLineSegment(sketch, "E14.24.6.2", {"start": v(594.99, 55.99) * mm, "end": v(574.25, 42.53) * mm});
            skLineSegment(sketch, "E14.27.6.2", {"start": v(574.25, 42.53) * mm, "end": v(594.99, 29.06) * mm});
            skLineSegment(sketch, "E14.30.6.2", {"start": v(594.99, 29.06) * mm, "end": v(623.36, 29.06) * mm});
            skLineSegment(sketch, "E14.33.6.2", {"start": v(623.36, 29.06) * mm, "end": v(644.1, 42.53) * mm});
            skLineSegment(sketch, "E14.0.6.3", {"start": v(626.62, 87.42) * mm, "end": v(647.36, 100.88) * mm});
            skLineSegment(sketch, "E14.3.6.3", {"start": v(647.36, 100.88) * mm, "end": v(675.73, 100.88) * mm});
            skLineSegment(sketch, "E14.6.6.3", {"start": v(675.73, 100.88) * mm, "end": v(696.47, 87.42) * mm});
            skLineSegment(sketch, "E14.9.6.3", {"start": v(647.36, 73.96) * mm, "end": v(626.62, 87.42) * mm});
            skLineSegment(sketch, "E14.12.6.3", {"start": v(696.47, 87.42) * mm, "end": v(675.73, 73.96) * mm});
            skLineSegment(sketch, "E14.15.6.3", {"start": v(644.1, 72.47) * mm, "end": v(623.36, 85.93) * mm});
            skLineSegment(sketch, "E14.18.6.3", {"start": v(675.73, 73.96) * mm, "end": v(647.36, 73.96) * mm});
            skLineSegment(sketch, "E14.21.6.3", {"start": v(623.36, 85.93) * mm, "end": v(594.99, 85.93) * mm});
            skLineSegment(sketch, "E14.24.6.3", {"start": v(594.99, 85.93) * mm, "end": v(574.25, 72.47) * mm});
            skLineSegment(sketch, "E14.27.6.3", {"start": v(574.25, 72.47) * mm, "end": v(594.99, 59) * mm});
            skLineSegment(sketch, "E14.30.6.3", {"start": v(594.99, 59) * mm, "end": v(623.36, 59) * mm});
            skLineSegment(sketch, "E14.33.6.3", {"start": v(623.36, 59) * mm, "end": v(644.1, 72.47) * mm});
            skLineSegment(sketch, "E14.0.6.4", {"start": v(626.62, 117.37) * mm, "end": v(647.36, 130.83) * mm});
            skLineSegment(sketch, "E14.3.6.4", {"start": v(647.36, 130.83) * mm, "end": v(675.73, 130.83) * mm});
            skLineSegment(sketch, "E14.6.6.4", {"start": v(675.73, 130.83) * mm, "end": v(696.47, 117.37) * mm});
            skLineSegment(sketch, "E14.9.6.4", {"start": v(647.36, 103.9) * mm, "end": v(626.62, 117.37) * mm});
            skLineSegment(sketch, "E14.12.6.4", {"start": v(696.47, 117.37) * mm, "end": v(675.73, 103.9) * mm});
            skLineSegment(sketch, "E14.15.6.4", {"start": v(644.1, 102.42) * mm, "end": v(623.36, 115.88) * mm});
            skLineSegment(sketch, "E14.18.6.4", {"start": v(675.73, 103.9) * mm, "end": v(647.36, 103.9) * mm});
            skLineSegment(sketch, "E14.21.6.4", {"start": v(623.36, 115.88) * mm, "end": v(594.99, 115.88) * mm});
            skLineSegment(sketch, "E14.24.6.4", {"start": v(594.99, 115.88) * mm, "end": v(574.25, 102.42) * mm});
            skLineSegment(sketch, "E14.27.6.4", {"start": v(574.25, 102.42) * mm, "end": v(594.99, 88.96) * mm});
            skLineSegment(sketch, "E14.30.6.4", {"start": v(594.99, 88.96) * mm, "end": v(623.36, 88.96) * mm});
            skLineSegment(sketch, "E14.33.6.4", {"start": v(623.36, 88.96) * mm, "end": v(644.1, 102.42) * mm});
            skLineSegment(sketch, "E14.0.6.5", {"start": v(626.62, 147.31) * mm, "end": v(647.36, 160.77) * mm});
            skLineSegment(sketch, "E14.3.6.5", {"start": v(647.36, 160.77) * mm, "end": v(675.73, 160.77) * mm});
            skLineSegment(sketch, "E14.6.6.5", {"start": v(675.73, 160.77) * mm, "end": v(696.47, 147.31) * mm});
            skLineSegment(sketch, "E14.9.6.5", {"start": v(647.36, 133.85) * mm, "end": v(626.62, 147.31) * mm});
            skLineSegment(sketch, "E14.12.6.5", {"start": v(696.47, 147.31) * mm, "end": v(675.73, 133.85) * mm});
            skLineSegment(sketch, "E14.15.6.5", {"start": v(644.1, 132.37) * mm, "end": v(623.36, 145.83) * mm});
            skLineSegment(sketch, "E14.18.6.5", {"start": v(675.73, 133.85) * mm, "end": v(647.36, 133.85) * mm});
            skLineSegment(sketch, "E14.21.6.5", {"start": v(623.36, 145.83) * mm, "end": v(594.99, 145.83) * mm});
            skLineSegment(sketch, "E14.24.6.5", {"start": v(594.99, 145.83) * mm, "end": v(574.25, 132.37) * mm});
            skLineSegment(sketch, "E14.27.6.5", {"start": v(574.25, 132.37) * mm, "end": v(594.99, 118.9) * mm});
            skLineSegment(sketch, "E14.30.6.5", {"start": v(594.99, 118.9) * mm, "end": v(623.36, 118.9) * mm});
            skLineSegment(sketch, "E14.33.6.5", {"start": v(623.36, 118.9) * mm, "end": v(644.1, 132.37) * mm});
            skLineSegment(sketch, "E14.0.6.6", {"start": v(626.62, 177.26) * mm, "end": v(647.36, 190.72) * mm});
            skLineSegment(sketch, "E14.3.6.6", {"start": v(647.36, 190.72) * mm, "end": v(675.73, 190.72) * mm});
            skLineSegment(sketch, "E14.6.6.6", {"start": v(675.73, 190.72) * mm, "end": v(696.47, 177.26) * mm});
            skLineSegment(sketch, "E14.9.6.6", {"start": v(647.36, 163.8) * mm, "end": v(626.62, 177.26) * mm});
            skLineSegment(sketch, "E14.12.6.6", {"start": v(696.47, 177.26) * mm, "end": v(675.73, 163.8) * mm});
            skLineSegment(sketch, "E14.15.6.6", {"start": v(644.1, 162.31) * mm, "end": v(623.36, 175.77) * mm});
            skLineSegment(sketch, "E14.18.6.6", {"start": v(675.73, 163.8) * mm, "end": v(647.36, 163.8) * mm});
            skLineSegment(sketch, "E14.21.6.6", {"start": v(623.36, 175.77) * mm, "end": v(594.99, 175.77) * mm});
            skLineSegment(sketch, "E14.24.6.6", {"start": v(594.99, 175.77) * mm, "end": v(574.25, 162.31) * mm});
            skLineSegment(sketch, "E14.27.6.6", {"start": v(574.25, 162.31) * mm, "end": v(594.99, 148.85) * mm});
            skLineSegment(sketch, "E14.30.6.6", {"start": v(594.99, 148.85) * mm, "end": v(623.36, 148.85) * mm});
            skLineSegment(sketch, "E14.33.6.6", {"start": v(623.36, 148.85) * mm, "end": v(644.1, 162.31) * mm});
            skLineSegment(sketch, "E14.0.6.7", {"start": v(626.62, 207.2) * mm, "end": v(647.36, 220.67) * mm});
            skLineSegment(sketch, "E14.3.6.7", {"start": v(647.36, 220.67) * mm, "end": v(675.73, 220.67) * mm});
            skLineSegment(sketch, "E14.6.6.7", {"start": v(675.73, 220.67) * mm, "end": v(696.47, 207.2) * mm});
            skLineSegment(sketch, "E14.9.6.7", {"start": v(647.36, 193.74) * mm, "end": v(626.62, 207.2) * mm});
            skLineSegment(sketch, "E14.12.6.7", {"start": v(696.47, 207.2) * mm, "end": v(675.73, 193.74) * mm});
            skLineSegment(sketch, "E14.15.6.7", {"start": v(644.1, 192.26) * mm, "end": v(623.36, 205.72) * mm});
            skLineSegment(sketch, "E14.18.6.7", {"start": v(675.73, 193.74) * mm, "end": v(647.36, 193.74) * mm});
            skLineSegment(sketch, "E14.21.6.7", {"start": v(623.36, 205.72) * mm, "end": v(594.99, 205.72) * mm});
            skLineSegment(sketch, "E14.24.6.7", {"start": v(594.99, 205.72) * mm, "end": v(574.25, 192.26) * mm});
            skLineSegment(sketch, "E14.27.6.7", {"start": v(574.25, 192.26) * mm, "end": v(594.99, 178.8) * mm});
            skLineSegment(sketch, "E14.30.6.7", {"start": v(594.99, 178.8) * mm, "end": v(623.36, 178.8) * mm});
            skLineSegment(sketch, "E14.33.6.7", {"start": v(623.36, 178.8) * mm, "end": v(644.1, 192.26) * mm});
            skLineSegment(sketch, "E14.0.6.8", {"start": v(626.62, 237.15) * mm, "end": v(647.36, 250.61) * mm});
            skLineSegment(sketch, "E14.3.6.8", {"start": v(647.36, 250.61) * mm, "end": v(675.73, 250.61) * mm});
            skLineSegment(sketch, "E14.6.6.8", {"start": v(675.73, 250.61) * mm, "end": v(696.47, 237.15) * mm});
            skLineSegment(sketch, "E14.9.6.8", {"start": v(647.36, 223.7) * mm, "end": v(626.62, 237.15) * mm});
            skLineSegment(sketch, "E14.12.6.8", {"start": v(696.47, 237.15) * mm, "end": v(675.73, 223.7) * mm});
            skLineSegment(sketch, "E14.15.6.8", {"start": v(644.1, 222.2) * mm, "end": v(623.36, 235.67) * mm});
            skLineSegment(sketch, "E14.18.6.8", {"start": v(675.73, 223.7) * mm, "end": v(647.36, 223.7) * mm});
            skLineSegment(sketch, "E14.21.6.8", {"start": v(623.36, 235.67) * mm, "end": v(594.99, 235.67) * mm});
            skLineSegment(sketch, "E14.24.6.8", {"start": v(594.99, 235.67) * mm, "end": v(574.25, 222.2) * mm});
            skLineSegment(sketch, "E14.27.6.8", {"start": v(574.25, 222.2) * mm, "end": v(594.99, 208.74) * mm});
            skLineSegment(sketch, "E14.30.6.8", {"start": v(594.99, 208.74) * mm, "end": v(623.36, 208.74) * mm});
            skLineSegment(sketch, "E14.33.6.8", {"start": v(623.36, 208.74) * mm, "end": v(644.1, 222.2) * mm});
            skLineSegment(sketch, "E14.0.6.9", {"start": v(626.62, 267.1) * mm, "end": v(647.36, 280.56) * mm});
            skLineSegment(sketch, "E14.3.6.9", {"start": v(647.36, 280.56) * mm, "end": v(675.73, 280.56) * mm});
            skLineSegment(sketch, "E14.6.6.9", {"start": v(675.73, 280.56) * mm, "end": v(696.47, 267.1) * mm});
            skLineSegment(sketch, "E14.9.6.9", {"start": v(647.36, 253.64) * mm, "end": v(626.62, 267.1) * mm});
            skLineSegment(sketch, "E14.12.6.9", {"start": v(696.47, 267.1) * mm, "end": v(675.73, 253.64) * mm});
            skLineSegment(sketch, "E14.15.6.9", {"start": v(644.1, 252.15) * mm, "end": v(623.36, 265.61) * mm});
            skLineSegment(sketch, "E14.18.6.9", {"start": v(675.73, 253.64) * mm, "end": v(647.36, 253.64) * mm});
            skLineSegment(sketch, "E14.21.6.9", {"start": v(623.36, 265.61) * mm, "end": v(594.99, 265.61) * mm});
            skLineSegment(sketch, "E14.24.6.9", {"start": v(594.99, 265.61) * mm, "end": v(574.25, 252.15) * mm});
            skLineSegment(sketch, "E14.27.6.9", {"start": v(574.25, 252.15) * mm, "end": v(594.99, 238.69) * mm});
            skLineSegment(sketch, "E14.30.6.9", {"start": v(594.99, 238.69) * mm, "end": v(623.36, 238.69) * mm});
            skLineSegment(sketch, "E14.33.6.9", {"start": v(623.36, 238.69) * mm, "end": v(644.1, 252.15) * mm});
            skLineSegment(sketch, "E14.0.6.10", {"start": v(626.62, 297.05) * mm, "end": v(647.36, 310.5) * mm});
            skLineSegment(sketch, "E14.3.6.10", {"start": v(647.36, 310.5) * mm, "end": v(675.73, 310.5) * mm});
            skLineSegment(sketch, "E14.6.6.10", {"start": v(675.73, 310.5) * mm, "end": v(696.47, 297.05) * mm});
            skLineSegment(sketch, "E14.9.6.10", {"start": v(647.36, 283.58) * mm, "end": v(626.62, 297.05) * mm});
            skLineSegment(sketch, "E14.12.6.10", {"start": v(696.47, 297.05) * mm, "end": v(675.73, 283.58) * mm});
            skLineSegment(sketch, "E14.15.6.10", {"start": v(644.1, 282.1) * mm, "end": v(623.36, 295.56) * mm});
            skLineSegment(sketch, "E14.18.6.10", {"start": v(675.73, 283.58) * mm, "end": v(647.36, 283.58) * mm});
            skLineSegment(sketch, "E14.21.6.10", {"start": v(623.36, 295.56) * mm, "end": v(594.99, 295.56) * mm});
            skLineSegment(sketch, "E14.24.6.10", {"start": v(594.99, 295.56) * mm, "end": v(574.25, 282.1) * mm});
            skLineSegment(sketch, "E14.27.6.10", {"start": v(574.25, 282.1) * mm, "end": v(594.99, 268.64) * mm});
            skLineSegment(sketch, "E14.30.6.10", {"start": v(594.99, 268.64) * mm, "end": v(623.36, 268.64) * mm});
            skLineSegment(sketch, "E14.33.6.10", {"start": v(623.36, 268.64) * mm, "end": v(644.1, 282.1) * mm});
            skLineSegment(sketch, "E14.0.6.11", {"start": v(626.62, 327) * mm, "end": v(647.36, 340.45) * mm});
            skLineSegment(sketch, "E14.3.6.11", {"start": v(647.36, 340.45) * mm, "end": v(675.73, 340.45) * mm});
            skLineSegment(sketch, "E14.6.6.11", {"start": v(675.73, 340.45) * mm, "end": v(696.47, 327) * mm});
            skLineSegment(sketch, "E14.9.6.11", {"start": v(647.36, 313.53) * mm, "end": v(626.62, 327) * mm});
            skLineSegment(sketch, "E14.12.6.11", {"start": v(696.47, 327) * mm, "end": v(675.73, 313.53) * mm});
            skLineSegment(sketch, "E14.15.6.11", {"start": v(644.1, 312.04) * mm, "end": v(623.36, 325.5) * mm});
            skLineSegment(sketch, "E14.18.6.11", {"start": v(675.73, 313.53) * mm, "end": v(647.36, 313.53) * mm});
            skLineSegment(sketch, "E14.21.6.11", {"start": v(623.36, 325.5) * mm, "end": v(594.99, 325.5) * mm});
            skLineSegment(sketch, "E14.24.6.11", {"start": v(594.99, 325.5) * mm, "end": v(574.25, 312.04) * mm});
            skLineSegment(sketch, "E14.27.6.11", {"start": v(574.25, 312.04) * mm, "end": v(594.99, 298.58) * mm});
            skLineSegment(sketch, "E14.30.6.11", {"start": v(594.99, 298.58) * mm, "end": v(623.36, 298.58) * mm});
            skLineSegment(sketch, "E14.33.6.11", {"start": v(623.36, 298.58) * mm, "end": v(644.1, 312.04) * mm});
            skLineSegment(sketch, "E14.0.6.12", {"start": v(626.62, 356.94) * mm, "end": v(647.36, 370.4) * mm});
            skLineSegment(sketch, "E14.3.6.12", {"start": v(647.36, 370.4) * mm, "end": v(675.73, 370.4) * mm});
            skLineSegment(sketch, "E14.6.6.12", {"start": v(675.73, 370.4) * mm, "end": v(696.47, 356.94) * mm});
            skLineSegment(sketch, "E14.9.6.12", {"start": v(647.36, 343.48) * mm, "end": v(626.62, 356.94) * mm});
            skLineSegment(sketch, "E14.12.6.12", {"start": v(696.47, 356.94) * mm, "end": v(675.73, 343.48) * mm});
            skLineSegment(sketch, "E14.15.6.12", {"start": v(644.1, 342) * mm, "end": v(623.36, 355.45) * mm});
            skLineSegment(sketch, "E14.18.6.12", {"start": v(675.73, 343.48) * mm, "end": v(647.36, 343.48) * mm});
            skLineSegment(sketch, "E14.21.6.12", {"start": v(623.36, 355.45) * mm, "end": v(594.99, 355.45) * mm});
            skLineSegment(sketch, "E14.24.6.12", {"start": v(594.99, 355.45) * mm, "end": v(574.25, 342) * mm});
            skLineSegment(sketch, "E14.27.6.12", {"start": v(574.25, 342) * mm, "end": v(594.99, 328.53) * mm});
            skLineSegment(sketch, "E14.30.6.12", {"start": v(594.99, 328.53) * mm, "end": v(623.36, 328.53) * mm});
            skLineSegment(sketch, "E14.33.6.12", {"start": v(623.36, 328.53) * mm, "end": v(644.1, 342) * mm});
            skLineSegment(sketch, "E14.0.6.13", {"start": v(626.62, 386.89) * mm, "end": v(647.36, 400.35) * mm});
            skLineSegment(sketch, "E14.3.6.13", {"start": v(647.36, 400.35) * mm, "end": v(675.73, 400.35) * mm});
            skLineSegment(sketch, "E14.6.6.13", {"start": v(675.73, 400.35) * mm, "end": v(696.47, 386.89) * mm});
            skLineSegment(sketch, "E14.9.6.13", {"start": v(647.36, 373.42) * mm, "end": v(626.62, 386.89) * mm});
            skLineSegment(sketch, "E14.12.6.13", {"start": v(696.47, 386.89) * mm, "end": v(675.73, 373.42) * mm});
            skLineSegment(sketch, "E14.15.6.13", {"start": v(644.1, 371.94) * mm, "end": v(623.36, 385.4) * mm});
            skLineSegment(sketch, "E14.18.6.13", {"start": v(675.73, 373.42) * mm, "end": v(647.36, 373.42) * mm});
            skLineSegment(sketch, "E14.21.6.13", {"start": v(623.36, 385.4) * mm, "end": v(594.99, 385.4) * mm});
            skLineSegment(sketch, "E14.24.6.13", {"start": v(594.99, 385.4) * mm, "end": v(574.25, 371.94) * mm});
            skLineSegment(sketch, "E14.27.6.13", {"start": v(574.25, 371.94) * mm, "end": v(594.99, 358.48) * mm});
            skLineSegment(sketch, "E14.30.6.13", {"start": v(594.99, 358.48) * mm, "end": v(623.36, 358.48) * mm});
            skLineSegment(sketch, "E14.33.6.13", {"start": v(623.36, 358.48) * mm, "end": v(644.1, 371.94) * mm});
            skLineSegment(sketch, "E14.0.6.14", {"start": v(626.62, 416.83) * mm, "end": v(647.36, 430.3) * mm});
            skLineSegment(sketch, "E14.3.6.14", {"start": v(647.36, 430.3) * mm, "end": v(675.73, 430.3) * mm});
            skLineSegment(sketch, "E14.6.6.14", {"start": v(675.73, 430.3) * mm, "end": v(696.47, 416.83) * mm});
            skLineSegment(sketch, "E14.9.6.14", {"start": v(647.36, 403.37) * mm, "end": v(626.62, 416.83) * mm});
            skLineSegment(sketch, "E14.12.6.14", {"start": v(696.47, 416.83) * mm, "end": v(675.73, 403.37) * mm});
            skLineSegment(sketch, "E14.15.6.14", {"start": v(644.1, 401.88) * mm, "end": v(623.36, 415.35) * mm});
            skLineSegment(sketch, "E14.18.6.14", {"start": v(675.73, 403.37) * mm, "end": v(647.36, 403.37) * mm});
            skLineSegment(sketch, "E14.21.6.14", {"start": v(623.36, 415.35) * mm, "end": v(594.99, 415.35) * mm});
            skLineSegment(sketch, "E14.24.6.14", {"start": v(594.99, 415.35) * mm, "end": v(574.25, 401.88) * mm});
            skLineSegment(sketch, "E14.27.6.14", {"start": v(574.25, 401.88) * mm, "end": v(594.99, 388.42) * mm});
            skLineSegment(sketch, "E14.30.6.14", {"start": v(594.99, 388.42) * mm, "end": v(623.36, 388.42) * mm});
            skLineSegment(sketch, "E14.33.6.14", {"start": v(623.36, 388.42) * mm, "end": v(644.1, 401.88) * mm});
            skLineSegment(sketch, "E14.0.6.15", {"start": v(626.62, 446.78) * mm, "end": v(647.36, 460.24) * mm});
            skLineSegment(sketch, "E14.3.6.15", {"start": v(647.36, 460.24) * mm, "end": v(675.73, 460.24) * mm});
            skLineSegment(sketch, "E14.6.6.15", {"start": v(675.73, 460.24) * mm, "end": v(696.47, 446.78) * mm});
            skLineSegment(sketch, "E14.9.6.15", {"start": v(647.36, 433.32) * mm, "end": v(626.62, 446.78) * mm});
            skLineSegment(sketch, "E14.12.6.15", {"start": v(696.47, 446.78) * mm, "end": v(675.73, 433.32) * mm});
            skLineSegment(sketch, "E14.15.6.15", {"start": v(644.1, 431.83) * mm, "end": v(623.36, 445.3) * mm});
            skLineSegment(sketch, "E14.18.6.15", {"start": v(675.73, 433.32) * mm, "end": v(647.36, 433.32) * mm});
            skLineSegment(sketch, "E14.21.6.15", {"start": v(623.36, 445.3) * mm, "end": v(594.99, 445.3) * mm});
            skLineSegment(sketch, "E14.24.6.15", {"start": v(594.99, 445.3) * mm, "end": v(574.25, 431.83) * mm});
            skLineSegment(sketch, "E14.27.6.15", {"start": v(574.25, 431.83) * mm, "end": v(594.99, 418.37) * mm});
            skLineSegment(sketch, "E14.30.6.15", {"start": v(594.99, 418.37) * mm, "end": v(623.36, 418.37) * mm});
            skLineSegment(sketch, "E14.33.6.15", {"start": v(623.36, 418.37) * mm, "end": v(644.1, 431.83) * mm});
            skLineSegment(sketch, "E14.0.6.16", {"start": v(626.62, 476.73) * mm, "end": v(647.36, 490.19) * mm});
            skLineSegment(sketch, "E14.3.6.16", {"start": v(647.36, 490.19) * mm, "end": v(675.73, 490.19) * mm});
            skLineSegment(sketch, "E14.6.6.16", {"start": v(675.73, 490.19) * mm, "end": v(696.47, 476.73) * mm});
            skLineSegment(sketch, "E14.9.6.16", {"start": v(647.36, 463.26) * mm, "end": v(626.62, 476.73) * mm});
            skLineSegment(sketch, "E14.12.6.16", {"start": v(696.47, 476.73) * mm, "end": v(675.73, 463.26) * mm});
            skLineSegment(sketch, "E14.15.6.16", {"start": v(644.1, 461.78) * mm, "end": v(623.36, 475.24) * mm});
            skLineSegment(sketch, "E14.18.6.16", {"start": v(675.73, 463.26) * mm, "end": v(647.36, 463.26) * mm});
            skLineSegment(sketch, "E14.21.6.16", {"start": v(623.36, 475.24) * mm, "end": v(594.99, 475.24) * mm});
            skLineSegment(sketch, "E14.24.6.16", {"start": v(594.99, 475.24) * mm, "end": v(574.25, 461.78) * mm});
            skLineSegment(sketch, "E14.27.6.16", {"start": v(574.25, 461.78) * mm, "end": v(594.99, 448.32) * mm});
            skLineSegment(sketch, "E14.30.6.16", {"start": v(594.99, 448.32) * mm, "end": v(623.36, 448.32) * mm});
            skLineSegment(sketch, "E14.33.6.16", {"start": v(623.36, 448.32) * mm, "end": v(644.1, 461.78) * mm});
            skLineSegment(sketch, "E15.0.0.17", {"start": v(1.85, 509.1) * mm, "end": v(22.6, 522.55) * mm});
            skLineSegment(sketch, "E15.3.0.17", {"start": v(22.6, 522.55) * mm, "end": v(50.96, 522.55) * mm});
            skLineSegment(sketch, "E15.6.0.17", {"start": v(50.96, 522.55) * mm, "end": v(71.7, 509.1) * mm});
            skLineSegment(sketch, "E15.9.0.17", {"start": v(22.6, 495.63) * mm, "end": v(1.85, 509.1) * mm});
            skLineSegment(sketch, "E15.12.0.17", {"start": v(71.7, 509.1) * mm, "end": v(50.96, 495.63) * mm});
            skLineSegment(sketch, "E15.15.0.17", {"start": v(19.33, 494.14) * mm, "end": v(-1.41, 507.6) * mm});
            skLineSegment(sketch, "E15.18.0.17", {"start": v(50.96, 495.63) * mm, "end": v(22.6, 495.63) * mm});
            skLineSegment(sketch, "E15.21.0.17", {"start": v(-1.41, 507.6) * mm, "end": v(-29.78, 507.6) * mm});
            skLineSegment(sketch, "E15.24.0.17", {"start": v(-29.78, 507.6) * mm, "end": v(-50.52, 494.14) * mm});
            skLineSegment(sketch, "E15.27.0.17", {"start": v(-50.52, 494.14) * mm, "end": v(-29.78, 480.68) * mm});
            skLineSegment(sketch, "E15.30.0.17", {"start": v(-29.78, 480.68) * mm, "end": v(-1.41, 480.68) * mm});
            skLineSegment(sketch, "E15.33.0.17", {"start": v(-1.41, 480.68) * mm, "end": v(19.33, 494.14) * mm});
            skLineSegment(sketch, "E15.0.0.18", {"start": v(1.85, 539.04) * mm, "end": v(22.6, 552.5) * mm});
            skLineSegment(sketch, "E15.3.0.18", {"start": v(22.6, 552.5) * mm, "end": v(50.96, 552.5) * mm});
            skLineSegment(sketch, "E15.6.0.18", {"start": v(50.96, 552.5) * mm, "end": v(71.7, 539.04) * mm});
            skLineSegment(sketch, "E15.9.0.18", {"start": v(22.6, 525.58) * mm, "end": v(1.85, 539.04) * mm});
            skLineSegment(sketch, "E15.12.0.18", {"start": v(71.7, 539.04) * mm, "end": v(50.96, 525.58) * mm});
            skLineSegment(sketch, "E15.15.0.18", {"start": v(19.33, 524.1) * mm, "end": v(-1.41, 537.55) * mm});
            skLineSegment(sketch, "E15.18.0.18", {"start": v(50.96, 525.58) * mm, "end": v(22.6, 525.58) * mm});
            skLineSegment(sketch, "E15.21.0.18", {"start": v(-1.41, 537.55) * mm, "end": v(-29.78, 537.55) * mm});
            skLineSegment(sketch, "E15.24.0.18", {"start": v(-29.78, 537.55) * mm, "end": v(-50.52, 524.1) * mm});
            skLineSegment(sketch, "E15.27.0.18", {"start": v(-50.52, 524.1) * mm, "end": v(-29.78, 510.63) * mm});
            skLineSegment(sketch, "E15.30.0.18", {"start": v(-29.78, 510.63) * mm, "end": v(-1.41, 510.63) * mm});
            skLineSegment(sketch, "E15.33.0.18", {"start": v(-1.41, 510.63) * mm, "end": v(19.33, 524.1) * mm});
            skLineSegment(sketch, "E15.0.0.19", {"start": v(1.85, 568.99) * mm, "end": v(22.6, 582.45) * mm});
            skLineSegment(sketch, "E15.3.0.19", {"start": v(22.6, 582.45) * mm, "end": v(50.96, 582.45) * mm});
            skLineSegment(sketch, "E15.6.0.19", {"start": v(50.96, 582.45) * mm, "end": v(71.7, 568.99) * mm});
            skLineSegment(sketch, "E15.9.0.19", {"start": v(22.6, 555.52) * mm, "end": v(1.85, 568.99) * mm});
            skLineSegment(sketch, "E15.12.0.19", {"start": v(71.7, 568.99) * mm, "end": v(50.96, 555.52) * mm});
            skLineSegment(sketch, "E15.15.0.19", {"start": v(19.33, 554.04) * mm, "end": v(-1.41, 567.5) * mm});
            skLineSegment(sketch, "E15.18.0.19", {"start": v(50.96, 555.52) * mm, "end": v(22.6, 555.52) * mm});
            skLineSegment(sketch, "E15.21.0.19", {"start": v(-1.41, 567.5) * mm, "end": v(-29.78, 567.5) * mm});
            skLineSegment(sketch, "E15.24.0.19", {"start": v(-29.78, 567.5) * mm, "end": v(-50.52, 554.04) * mm});
            skLineSegment(sketch, "E15.27.0.19", {"start": v(-50.52, 554.04) * mm, "end": v(-29.78, 540.58) * mm});
            skLineSegment(sketch, "E15.30.0.19", {"start": v(-29.78, 540.58) * mm, "end": v(-1.41, 540.58) * mm});
            skLineSegment(sketch, "E15.33.0.19", {"start": v(-1.41, 540.58) * mm, "end": v(19.33, 554.04) * mm});
            skLineSegment(sketch, "E15.0.1.17", {"start": v(105.98, 508.69) * mm, "end": v(126.72, 522.15) * mm});
            skLineSegment(sketch, "E15.3.1.17", {"start": v(126.72, 522.15) * mm, "end": v(155.1, 522.15) * mm});
            skLineSegment(sketch, "E15.6.1.17", {"start": v(155.1, 522.15) * mm, "end": v(175.83, 508.69) * mm});
            skLineSegment(sketch, "E15.9.1.17", {"start": v(126.72, 495.23) * mm, "end": v(105.98, 508.69) * mm});
            skLineSegment(sketch, "E15.12.1.17", {"start": v(175.83, 508.69) * mm, "end": v(155.1, 495.23) * mm});
            skLineSegment(sketch, "E15.15.1.17", {"start": v(123.46, 493.74) * mm, "end": v(102.72, 507.2) * mm});
            skLineSegment(sketch, "E15.18.1.17", {"start": v(155.1, 495.23) * mm, "end": v(126.72, 495.23) * mm});
            skLineSegment(sketch, "E15.21.1.17", {"start": v(102.72, 507.2) * mm, "end": v(74.34, 507.2) * mm});
            skLineSegment(sketch, "E15.24.1.17", {"start": v(74.34, 507.2) * mm, "end": v(53.6, 493.74) * mm});
            skLineSegment(sketch, "E15.27.1.17", {"start": v(53.6, 493.74) * mm, "end": v(74.34, 480.28) * mm});
            skLineSegment(sketch, "E15.30.1.17", {"start": v(74.34, 480.28) * mm, "end": v(102.72, 480.28) * mm});
            skLineSegment(sketch, "E15.33.1.17", {"start": v(102.72, 480.28) * mm, "end": v(123.46, 493.74) * mm});
            skLineSegment(sketch, "E15.0.1.18", {"start": v(105.98, 538.64) * mm, "end": v(126.72, 552.1) * mm});
            skLineSegment(sketch, "E15.3.1.18", {"start": v(126.72, 552.1) * mm, "end": v(155.1, 552.1) * mm});
            skLineSegment(sketch, "E15.6.1.18", {"start": v(155.1, 552.1) * mm, "end": v(175.83, 538.64) * mm});
            skLineSegment(sketch, "E15.9.1.18", {"start": v(126.72, 525.17) * mm, "end": v(105.98, 538.64) * mm});
            skLineSegment(sketch, "E15.12.1.18", {"start": v(175.83, 538.64) * mm, "end": v(155.1, 525.17) * mm});
            skLineSegment(sketch, "E15.15.1.18", {"start": v(123.46, 523.69) * mm, "end": v(102.72, 537.15) * mm});
            skLineSegment(sketch, "E15.18.1.18", {"start": v(155.1, 525.17) * mm, "end": v(126.72, 525.17) * mm});
            skLineSegment(sketch, "E15.21.1.18", {"start": v(102.72, 537.15) * mm, "end": v(74.34, 537.15) * mm});
            skLineSegment(sketch, "E15.24.1.18", {"start": v(74.34, 537.15) * mm, "end": v(53.6, 523.69) * mm});
            skLineSegment(sketch, "E15.27.1.18", {"start": v(53.6, 523.69) * mm, "end": v(74.34, 510.23) * mm});
            skLineSegment(sketch, "E15.30.1.18", {"start": v(74.34, 510.23) * mm, "end": v(102.72, 510.23) * mm});
            skLineSegment(sketch, "E15.33.1.18", {"start": v(102.72, 510.23) * mm, "end": v(123.46, 523.69) * mm});
            skLineSegment(sketch, "E15.0.1.19", {"start": v(105.98, 568.58) * mm, "end": v(126.72, 582.04) * mm});
            skLineSegment(sketch, "E15.3.1.19", {"start": v(126.72, 582.04) * mm, "end": v(155.1, 582.04) * mm});
            skLineSegment(sketch, "E15.6.1.19", {"start": v(155.1, 582.04) * mm, "end": v(175.83, 568.58) * mm});
            skLineSegment(sketch, "E15.9.1.19", {"start": v(126.72, 555.12) * mm, "end": v(105.98, 568.58) * mm});
            skLineSegment(sketch, "E15.12.1.19", {"start": v(175.83, 568.58) * mm, "end": v(155.1, 555.12) * mm});
            skLineSegment(sketch, "E15.15.1.19", {"start": v(123.46, 553.63) * mm, "end": v(102.72, 567.1) * mm});
            skLineSegment(sketch, "E15.18.1.19", {"start": v(155.1, 555.12) * mm, "end": v(126.72, 555.12) * mm});
            skLineSegment(sketch, "E15.21.1.19", {"start": v(102.72, 567.1) * mm, "end": v(74.34, 567.1) * mm});
            skLineSegment(sketch, "E15.24.1.19", {"start": v(74.34, 567.1) * mm, "end": v(53.6, 553.63) * mm});
            skLineSegment(sketch, "E15.27.1.19", {"start": v(53.6, 553.63) * mm, "end": v(74.34, 540.17) * mm});
            skLineSegment(sketch, "E15.30.1.19", {"start": v(74.34, 540.17) * mm, "end": v(102.72, 540.17) * mm});
            skLineSegment(sketch, "E15.33.1.19", {"start": v(102.72, 540.17) * mm, "end": v(123.46, 553.63) * mm});
            skLineSegment(sketch, "E15.0.2.17", {"start": v(210.1, 508.29) * mm, "end": v(230.85, 521.75) * mm});
            skLineSegment(sketch, "E15.3.2.17", {"start": v(230.85, 521.75) * mm, "end": v(259.22, 521.75) * mm});
            skLineSegment(sketch, "E15.6.2.17", {"start": v(259.22, 521.75) * mm, "end": v(279.96, 508.29) * mm});
            skLineSegment(sketch, "E15.9.2.17", {"start": v(230.85, 494.82) * mm, "end": v(210.1, 508.29) * mm});
            skLineSegment(sketch, "E15.12.2.17", {"start": v(279.96, 508.29) * mm, "end": v(259.22, 494.82) * mm});
            skLineSegment(sketch, "E15.15.2.17", {"start": v(227.58, 493.34) * mm, "end": v(206.85, 506.8) * mm});
            skLineSegment(sketch, "E15.18.2.17", {"start": v(259.22, 494.82) * mm, "end": v(230.85, 494.82) * mm});
            skLineSegment(sketch, "E15.21.2.17", {"start": v(206.85, 506.8) * mm, "end": v(178.47, 506.8) * mm});
            skLineSegment(sketch, "E15.24.2.17", {"start": v(178.47, 506.8) * mm, "end": v(157.73, 493.34) * mm});
            skLineSegment(sketch, "E15.27.2.17", {"start": v(157.73, 493.34) * mm, "end": v(178.47, 479.88) * mm});
            skLineSegment(sketch, "E15.30.2.17", {"start": v(178.47, 479.88) * mm, "end": v(206.85, 479.88) * mm});
            skLineSegment(sketch, "E15.33.2.17", {"start": v(206.85, 479.88) * mm, "end": v(227.58, 493.34) * mm});
            skLineSegment(sketch, "E15.0.2.18", {"start": v(210.1, 538.23) * mm, "end": v(230.85, 551.7) * mm});
            skLineSegment(sketch, "E15.3.2.18", {"start": v(230.85, 551.7) * mm, "end": v(259.22, 551.7) * mm});
            skLineSegment(sketch, "E15.6.2.18", {"start": v(259.22, 551.7) * mm, "end": v(279.96, 538.23) * mm});
            skLineSegment(sketch, "E15.9.2.18", {"start": v(230.85, 524.77) * mm, "end": v(210.1, 538.23) * mm});
            skLineSegment(sketch, "E15.12.2.18", {"start": v(279.96, 538.23) * mm, "end": v(259.22, 524.77) * mm});
            skLineSegment(sketch, "E15.15.2.18", {"start": v(227.58, 523.28) * mm, "end": v(206.85, 536.75) * mm});
            skLineSegment(sketch, "E15.18.2.18", {"start": v(259.22, 524.77) * mm, "end": v(230.85, 524.77) * mm});
            skLineSegment(sketch, "E15.21.2.18", {"start": v(206.85, 536.75) * mm, "end": v(178.47, 536.75) * mm});
            skLineSegment(sketch, "E15.24.2.18", {"start": v(178.47, 536.75) * mm, "end": v(157.73, 523.28) * mm});
            skLineSegment(sketch, "E15.27.2.18", {"start": v(157.73, 523.28) * mm, "end": v(178.47, 509.82) * mm});
            skLineSegment(sketch, "E15.30.2.18", {"start": v(178.47, 509.82) * mm, "end": v(206.85, 509.82) * mm});
            skLineSegment(sketch, "E15.33.2.18", {"start": v(206.85, 509.82) * mm, "end": v(227.58, 523.28) * mm});
            skLineSegment(sketch, "E15.0.2.19", {"start": v(210.1, 568.18) * mm, "end": v(230.85, 581.64) * mm});
            skLineSegment(sketch, "E15.3.2.19", {"start": v(230.85, 581.64) * mm, "end": v(259.22, 581.64) * mm});
            skLineSegment(sketch, "E15.6.2.19", {"start": v(259.22, 581.64) * mm, "end": v(279.96, 568.18) * mm});
            skLineSegment(sketch, "E15.9.2.19", {"start": v(230.85, 554.72) * mm, "end": v(210.1, 568.18) * mm});
            skLineSegment(sketch, "E15.12.2.19", {"start": v(279.96, 568.18) * mm, "end": v(259.22, 554.72) * mm});
            skLineSegment(sketch, "E15.15.2.19", {"start": v(227.58, 553.23) * mm, "end": v(206.85, 566.7) * mm});
            skLineSegment(sketch, "E15.18.2.19", {"start": v(259.22, 554.72) * mm, "end": v(230.85, 554.72) * mm});
            skLineSegment(sketch, "E15.21.2.19", {"start": v(206.85, 566.7) * mm, "end": v(178.47, 566.7) * mm});
            skLineSegment(sketch, "E15.24.2.19", {"start": v(178.47, 566.7) * mm, "end": v(157.73, 553.23) * mm});
            skLineSegment(sketch, "E15.27.2.19", {"start": v(157.73, 553.23) * mm, "end": v(178.47, 539.77) * mm});
            skLineSegment(sketch, "E15.30.2.19", {"start": v(178.47, 539.77) * mm, "end": v(206.85, 539.77) * mm});
            skLineSegment(sketch, "E15.33.2.19", {"start": v(206.85, 539.77) * mm, "end": v(227.58, 553.23) * mm});
            skLineSegment(sketch, "E15.0.3.17", {"start": v(314.24, 507.88) * mm, "end": v(334.98, 521.34) * mm});
            skLineSegment(sketch, "E15.3.3.17", {"start": v(334.98, 521.34) * mm, "end": v(363.35, 521.34) * mm});
            skLineSegment(sketch, "E15.6.3.17", {"start": v(363.35, 521.34) * mm, "end": v(384.09, 507.88) * mm});
            skLineSegment(sketch, "E15.9.3.17", {"start": v(334.98, 494.42) * mm, "end": v(314.24, 507.88) * mm});
            skLineSegment(sketch, "E15.12.3.17", {"start": v(384.09, 507.88) * mm, "end": v(363.35, 494.42) * mm});
            skLineSegment(sketch, "E15.15.3.17", {"start": v(331.71, 492.93) * mm, "end": v(310.97, 506.4) * mm});
            skLineSegment(sketch, "E15.18.3.17", {"start": v(363.35, 494.42) * mm, "end": v(334.98, 494.42) * mm});
            skLineSegment(sketch, "E15.21.3.17", {"start": v(310.97, 506.4) * mm, "end": v(282.6, 506.4) * mm});
            skLineSegment(sketch, "E15.24.3.17", {"start": v(282.6, 506.4) * mm, "end": v(261.86, 492.93) * mm});
            skLineSegment(sketch, "E15.27.3.17", {"start": v(261.86, 492.93) * mm, "end": v(282.6, 479.47) * mm});
            skLineSegment(sketch, "E15.30.3.17", {"start": v(282.6, 479.47) * mm, "end": v(310.97, 479.47) * mm});
            skLineSegment(sketch, "E15.33.3.17", {"start": v(310.97, 479.47) * mm, "end": v(331.71, 492.93) * mm});
            skLineSegment(sketch, "E15.0.3.18", {"start": v(314.24, 537.83) * mm, "end": v(334.98, 551.3) * mm});
            skLineSegment(sketch, "E15.3.3.18", {"start": v(334.98, 551.3) * mm, "end": v(363.35, 551.3) * mm});
            skLineSegment(sketch, "E15.6.3.18", {"start": v(363.35, 551.3) * mm, "end": v(384.09, 537.83) * mm});
            skLineSegment(sketch, "E15.9.3.18", {"start": v(334.98, 524.37) * mm, "end": v(314.24, 537.83) * mm});
            skLineSegment(sketch, "E15.12.3.18", {"start": v(384.09, 537.83) * mm, "end": v(363.35, 524.37) * mm});
            skLineSegment(sketch, "E15.15.3.18", {"start": v(331.71, 522.88) * mm, "end": v(310.97, 536.34) * mm});
            skLineSegment(sketch, "E15.18.3.18", {"start": v(363.35, 524.37) * mm, "end": v(334.98, 524.37) * mm});
            skLineSegment(sketch, "E15.21.3.18", {"start": v(310.97, 536.34) * mm, "end": v(282.6, 536.34) * mm});
            skLineSegment(sketch, "E15.24.3.18", {"start": v(282.6, 536.34) * mm, "end": v(261.86, 522.88) * mm});
            skLineSegment(sketch, "E15.27.3.18", {"start": v(261.86, 522.88) * mm, "end": v(282.6, 509.42) * mm});
            skLineSegment(sketch, "E15.30.3.18", {"start": v(282.6, 509.42) * mm, "end": v(310.97, 509.42) * mm});
            skLineSegment(sketch, "E15.33.3.18", {"start": v(310.97, 509.42) * mm, "end": v(331.71, 522.88) * mm});
            skLineSegment(sketch, "E15.0.3.19", {"start": v(314.24, 567.78) * mm, "end": v(334.98, 581.24) * mm});
            skLineSegment(sketch, "E15.3.3.19", {"start": v(334.98, 581.24) * mm, "end": v(363.35, 581.24) * mm});
            skLineSegment(sketch, "E15.6.3.19", {"start": v(363.35, 581.24) * mm, "end": v(384.09, 567.78) * mm});
            skLineSegment(sketch, "E15.9.3.19", {"start": v(334.98, 554.31) * mm, "end": v(314.24, 567.78) * mm});
            skLineSegment(sketch, "E15.12.3.19", {"start": v(384.09, 567.78) * mm, "end": v(363.35, 554.31) * mm});
            skLineSegment(sketch, "E15.15.3.19", {"start": v(331.71, 552.83) * mm, "end": v(310.97, 566.29) * mm});
            skLineSegment(sketch, "E15.18.3.19", {"start": v(363.35, 554.31) * mm, "end": v(334.98, 554.31) * mm});
            skLineSegment(sketch, "E15.21.3.19", {"start": v(310.97, 566.29) * mm, "end": v(282.6, 566.29) * mm});
            skLineSegment(sketch, "E15.24.3.19", {"start": v(282.6, 566.29) * mm, "end": v(261.86, 552.83) * mm});
            skLineSegment(sketch, "E15.27.3.19", {"start": v(261.86, 552.83) * mm, "end": v(282.6, 539.37) * mm});
            skLineSegment(sketch, "E15.30.3.19", {"start": v(282.6, 539.37) * mm, "end": v(310.97, 539.37) * mm});
            skLineSegment(sketch, "E15.33.3.19", {"start": v(310.97, 539.37) * mm, "end": v(331.71, 552.83) * mm});
            skLineSegment(sketch, "E15.0.4.17", {"start": v(418.37, 507.48) * mm, "end": v(439.1, 520.94) * mm});
            skLineSegment(sketch, "E15.3.4.17", {"start": v(439.1, 520.94) * mm, "end": v(467.48, 520.94) * mm});
            skLineSegment(sketch, "E15.6.4.17", {"start": v(467.48, 520.94) * mm, "end": v(488.22, 507.48) * mm});
            skLineSegment(sketch, "E15.9.4.17", {"start": v(439.1, 494.02) * mm, "end": v(418.37, 507.48) * mm});
            skLineSegment(sketch, "E15.12.4.17", {"start": v(488.22, 507.48) * mm, "end": v(467.48, 494.02) * mm});
            skLineSegment(sketch, "E15.15.4.17", {"start": v(435.84, 492.53) * mm, "end": v(415.1, 506) * mm});
            skLineSegment(sketch, "E15.18.4.17", {"start": v(467.48, 494.02) * mm, "end": v(439.1, 494.02) * mm});
            skLineSegment(sketch, "E15.21.4.17", {"start": v(415.1, 506) * mm, "end": v(386.73, 506) * mm});
            skLineSegment(sketch, "E15.24.4.17", {"start": v(386.73, 506) * mm, "end": v(366, 492.53) * mm});
            skLineSegment(sketch, "E15.27.4.17", {"start": v(366, 492.53) * mm, "end": v(386.73, 479.07) * mm});
            skLineSegment(sketch, "E15.30.4.17", {"start": v(386.73, 479.07) * mm, "end": v(415.1, 479.07) * mm});
            skLineSegment(sketch, "E15.33.4.17", {"start": v(415.1, 479.07) * mm, "end": v(435.84, 492.53) * mm});
            skLineSegment(sketch, "E15.0.4.18", {"start": v(418.37, 537.43) * mm, "end": v(439.1, 550.89) * mm});
            skLineSegment(sketch, "E15.3.4.18", {"start": v(439.1, 550.89) * mm, "end": v(467.48, 550.89) * mm});
            skLineSegment(sketch, "E15.6.4.18", {"start": v(467.48, 550.89) * mm, "end": v(488.22, 537.43) * mm});
            skLineSegment(sketch, "E15.9.4.18", {"start": v(439.1, 523.96) * mm, "end": v(418.37, 537.43) * mm});
            skLineSegment(sketch, "E15.12.4.18", {"start": v(488.22, 537.43) * mm, "end": v(467.48, 523.96) * mm});
            skLineSegment(sketch, "E15.15.4.18", {"start": v(435.84, 522.48) * mm, "end": v(415.1, 535.94) * mm});
            skLineSegment(sketch, "E15.18.4.18", {"start": v(467.48, 523.96) * mm, "end": v(439.1, 523.96) * mm});
            skLineSegment(sketch, "E15.21.4.18", {"start": v(415.1, 535.94) * mm, "end": v(386.73, 535.94) * mm});
            skLineSegment(sketch, "E15.24.4.18", {"start": v(386.73, 535.94) * mm, "end": v(366, 522.48) * mm});
            skLineSegment(sketch, "E15.27.4.18", {"start": v(366, 522.48) * mm, "end": v(386.73, 509.02) * mm});
            skLineSegment(sketch, "E15.30.4.18", {"start": v(386.73, 509.02) * mm, "end": v(415.1, 509.02) * mm});
            skLineSegment(sketch, "E15.33.4.18", {"start": v(415.1, 509.02) * mm, "end": v(435.84, 522.48) * mm});
            skLineSegment(sketch, "E15.0.4.19", {"start": v(418.37, 567.37) * mm, "end": v(439.1, 580.83) * mm});
            skLineSegment(sketch, "E15.3.4.19", {"start": v(439.1, 580.83) * mm, "end": v(467.48, 580.83) * mm});
            skLineSegment(sketch, "E15.6.4.19", {"start": v(467.48, 580.83) * mm, "end": v(488.22, 567.37) * mm});
            skLineSegment(sketch, "E15.9.4.19", {"start": v(439.1, 553.9) * mm, "end": v(418.37, 567.37) * mm});
            skLineSegment(sketch, "E15.12.4.19", {"start": v(488.22, 567.37) * mm, "end": v(467.48, 553.9) * mm});
            skLineSegment(sketch, "E15.15.4.19", {"start": v(435.84, 552.42) * mm, "end": v(415.1, 565.89) * mm});
            skLineSegment(sketch, "E15.18.4.19", {"start": v(467.48, 553.9) * mm, "end": v(439.1, 553.9) * mm});
            skLineSegment(sketch, "E15.21.4.19", {"start": v(415.1, 565.89) * mm, "end": v(386.73, 565.89) * mm});
            skLineSegment(sketch, "E15.24.4.19", {"start": v(386.73, 565.89) * mm, "end": v(366, 552.42) * mm});
            skLineSegment(sketch, "E15.27.4.19", {"start": v(366, 552.42) * mm, "end": v(386.73, 538.96) * mm});
            skLineSegment(sketch, "E15.30.4.19", {"start": v(386.73, 538.96) * mm, "end": v(415.1, 538.96) * mm});
            skLineSegment(sketch, "E15.33.4.19", {"start": v(415.1, 538.96) * mm, "end": v(435.84, 552.42) * mm});
            skLineSegment(sketch, "E15.0.5.17", {"start": v(522.5, 507.08) * mm, "end": v(543.23, 520.54) * mm});
            skLineSegment(sketch, "E15.3.5.17", {"start": v(543.23, 520.54) * mm, "end": v(571.6, 520.54) * mm});
            skLineSegment(sketch, "E15.6.5.17", {"start": v(571.6, 520.54) * mm, "end": v(592.34, 507.08) * mm});
            skLineSegment(sketch, "E15.9.5.17", {"start": v(543.23, 493.61) * mm, "end": v(522.5, 507.08) * mm});
            skLineSegment(sketch, "E15.12.5.17", {"start": v(592.34, 507.08) * mm, "end": v(571.6, 493.61) * mm});
            skLineSegment(sketch, "E15.15.5.17", {"start": v(539.97, 492.13) * mm, "end": v(519.23, 505.59) * mm});
            skLineSegment(sketch, "E15.18.5.17", {"start": v(571.6, 493.61) * mm, "end": v(543.23, 493.61) * mm});
            skLineSegment(sketch, "E15.21.5.17", {"start": v(519.23, 505.59) * mm, "end": v(490.86, 505.59) * mm});
            skLineSegment(sketch, "E15.24.5.17", {"start": v(490.86, 505.59) * mm, "end": v(470.12, 492.13) * mm});
            skLineSegment(sketch, "E15.27.5.17", {"start": v(470.12, 492.13) * mm, "end": v(490.86, 478.67) * mm});
            skLineSegment(sketch, "E15.30.5.17", {"start": v(490.86, 478.67) * mm, "end": v(519.23, 478.67) * mm});
            skLineSegment(sketch, "E15.33.5.17", {"start": v(519.23, 478.67) * mm, "end": v(539.97, 492.13) * mm});
            skLineSegment(sketch, "E15.0.5.18", {"start": v(522.5, 537.02) * mm, "end": v(543.23, 550.48) * mm});
            skLineSegment(sketch, "E15.3.5.18", {"start": v(543.23, 550.48) * mm, "end": v(571.6, 550.48) * mm});
            skLineSegment(sketch, "E15.6.5.18", {"start": v(571.6, 550.48) * mm, "end": v(592.34, 537.02) * mm});
            skLineSegment(sketch, "E15.9.5.18", {"start": v(543.23, 523.56) * mm, "end": v(522.5, 537.02) * mm});
            skLineSegment(sketch, "E15.12.5.18", {"start": v(592.34, 537.02) * mm, "end": v(571.6, 523.56) * mm});
            skLineSegment(sketch, "E15.15.5.18", {"start": v(539.97, 522.07) * mm, "end": v(519.23, 535.54) * mm});
            skLineSegment(sketch, "E15.18.5.18", {"start": v(571.6, 523.56) * mm, "end": v(543.23, 523.56) * mm});
            skLineSegment(sketch, "E15.21.5.18", {"start": v(519.23, 535.54) * mm, "end": v(490.86, 535.54) * mm});
            skLineSegment(sketch, "E15.24.5.18", {"start": v(490.86, 535.54) * mm, "end": v(470.12, 522.07) * mm});
            skLineSegment(sketch, "E15.27.5.18", {"start": v(470.12, 522.07) * mm, "end": v(490.86, 508.61) * mm});
            skLineSegment(sketch, "E15.30.5.18", {"start": v(490.86, 508.61) * mm, "end": v(519.23, 508.61) * mm});
            skLineSegment(sketch, "E15.33.5.18", {"start": v(519.23, 508.61) * mm, "end": v(539.97, 522.07) * mm});
            skLineSegment(sketch, "E15.0.5.19", {"start": v(522.5, 566.97) * mm, "end": v(543.23, 580.43) * mm});
            skLineSegment(sketch, "E15.3.5.19", {"start": v(543.23, 580.43) * mm, "end": v(571.6, 580.43) * mm});
            skLineSegment(sketch, "E15.6.5.19", {"start": v(571.6, 580.43) * mm, "end": v(592.34, 566.97) * mm});
            skLineSegment(sketch, "E15.9.5.19", {"start": v(543.23, 553.5) * mm, "end": v(522.5, 566.97) * mm});
            skLineSegment(sketch, "E15.12.5.19", {"start": v(592.34, 566.97) * mm, "end": v(571.6, 553.5) * mm});
            skLineSegment(sketch, "E15.15.5.19", {"start": v(539.97, 552.02) * mm, "end": v(519.23, 565.48) * mm});
            skLineSegment(sketch, "E15.18.5.19", {"start": v(571.6, 553.5) * mm, "end": v(543.23, 553.5) * mm});
            skLineSegment(sketch, "E15.21.5.19", {"start": v(519.23, 565.48) * mm, "end": v(490.86, 565.48) * mm});
            skLineSegment(sketch, "E15.24.5.19", {"start": v(490.86, 565.48) * mm, "end": v(470.12, 552.02) * mm});
            skLineSegment(sketch, "E15.27.5.19", {"start": v(470.12, 552.02) * mm, "end": v(490.86, 538.56) * mm});
            skLineSegment(sketch, "E15.30.5.19", {"start": v(490.86, 538.56) * mm, "end": v(519.23, 538.56) * mm});
            skLineSegment(sketch, "E15.33.5.19", {"start": v(519.23, 538.56) * mm, "end": v(539.97, 552.02) * mm});
            skLineSegment(sketch, "E15.0.6.17", {"start": v(626.62, 506.67) * mm, "end": v(647.36, 520.13) * mm});
            skLineSegment(sketch, "E15.3.6.17", {"start": v(647.36, 520.13) * mm, "end": v(675.73, 520.13) * mm});
            skLineSegment(sketch, "E15.6.6.17", {"start": v(675.73, 520.13) * mm, "end": v(696.47, 506.67) * mm});
            skLineSegment(sketch, "E15.9.6.17", {"start": v(647.36, 493.2) * mm, "end": v(626.62, 506.67) * mm});
            skLineSegment(sketch, "E15.12.6.17", {"start": v(696.47, 506.67) * mm, "end": v(675.73, 493.2) * mm});
            skLineSegment(sketch, "E15.15.6.17", {"start": v(644.1, 491.72) * mm, "end": v(623.36, 505.19) * mm});
            skLineSegment(sketch, "E15.18.6.17", {"start": v(675.73, 493.2) * mm, "end": v(647.36, 493.2) * mm});
            skLineSegment(sketch, "E15.21.6.17", {"start": v(623.36, 505.19) * mm, "end": v(594.99, 505.19) * mm});
            skLineSegment(sketch, "E15.24.6.17", {"start": v(594.99, 505.19) * mm, "end": v(574.25, 491.72) * mm});
            skLineSegment(sketch, "E15.27.6.17", {"start": v(574.25, 491.72) * mm, "end": v(594.99, 478.26) * mm});
            skLineSegment(sketch, "E15.30.6.17", {"start": v(594.99, 478.26) * mm, "end": v(623.36, 478.26) * mm});
            skLineSegment(sketch, "E15.33.6.17", {"start": v(623.36, 478.26) * mm, "end": v(644.1, 491.72) * mm});
            skLineSegment(sketch, "E15.0.6.18", {"start": v(626.62, 536.62) * mm, "end": v(647.36, 550.08) * mm});
            skLineSegment(sketch, "E15.3.6.18", {"start": v(647.36, 550.08) * mm, "end": v(675.73, 550.08) * mm});
            skLineSegment(sketch, "E15.6.6.18", {"start": v(675.73, 550.08) * mm, "end": v(696.47, 536.62) * mm});
            skLineSegment(sketch, "E15.9.6.18", {"start": v(647.36, 523.16) * mm, "end": v(626.62, 536.62) * mm});
            skLineSegment(sketch, "E15.12.6.18", {"start": v(696.47, 536.62) * mm, "end": v(675.73, 523.16) * mm});
            skLineSegment(sketch, "E15.15.6.18", {"start": v(644.1, 521.67) * mm, "end": v(623.36, 535.13) * mm});
            skLineSegment(sketch, "E15.18.6.18", {"start": v(675.73, 523.16) * mm, "end": v(647.36, 523.16) * mm});
            skLineSegment(sketch, "E15.21.6.18", {"start": v(623.36, 535.13) * mm, "end": v(594.99, 535.13) * mm});
            skLineSegment(sketch, "E15.24.6.18", {"start": v(594.99, 535.13) * mm, "end": v(574.25, 521.67) * mm});
            skLineSegment(sketch, "E15.27.6.18", {"start": v(574.25, 521.67) * mm, "end": v(594.99, 508.2) * mm});
            skLineSegment(sketch, "E15.30.6.18", {"start": v(594.99, 508.2) * mm, "end": v(623.36, 508.2) * mm});
            skLineSegment(sketch, "E15.33.6.18", {"start": v(623.36, 508.2) * mm, "end": v(644.1, 521.67) * mm});
            skLineSegment(sketch, "E15.0.6.19", {"start": v(626.62, 566.56) * mm, "end": v(647.36, 580.03) * mm});
            skLineSegment(sketch, "E15.3.6.19", {"start": v(647.36, 580.03) * mm, "end": v(675.73, 580.03) * mm});
            skLineSegment(sketch, "E15.6.6.19", {"start": v(675.73, 580.03) * mm, "end": v(696.47, 566.56) * mm});
            skLineSegment(sketch, "E15.9.6.19", {"start": v(647.36, 553.1) * mm, "end": v(626.62, 566.56) * mm});
            skLineSegment(sketch, "E15.12.6.19", {"start": v(696.47, 566.56) * mm, "end": v(675.73, 553.1) * mm});
            skLineSegment(sketch, "E15.15.6.19", {"start": v(644.1, 551.62) * mm, "end": v(623.36, 565.08) * mm});
            skLineSegment(sketch, "E15.18.6.19", {"start": v(675.73, 553.1) * mm, "end": v(647.36, 553.1) * mm});
            skLineSegment(sketch, "E15.21.6.19", {"start": v(623.36, 565.08) * mm, "end": v(594.99, 565.08) * mm});
            skLineSegment(sketch, "E15.24.6.19", {"start": v(594.99, 565.08) * mm, "end": v(574.25, 551.62) * mm});
            skLineSegment(sketch, "E15.27.6.19", {"start": v(574.25, 551.62) * mm, "end": v(594.99, 538.16) * mm});
            skLineSegment(sketch, "E15.30.6.19", {"start": v(594.99, 538.16) * mm, "end": v(623.36, 538.16) * mm});
            skLineSegment(sketch, "E15.33.6.19", {"start": v(623.36, 538.16) * mm, "end": v(644.1, 551.62) * mm});
            skLineSegment(sketch, "E16.0.0.20", {"start": v(1.85, 598.93) * mm, "end": v(22.6, 612.4) * mm});
            skLineSegment(sketch, "E16.3.0.20", {"start": v(22.6, 612.4) * mm, "end": v(50.96, 612.4) * mm});
            skLineSegment(sketch, "E16.6.0.20", {"start": v(50.96, 612.4) * mm, "end": v(71.7, 598.93) * mm});
            skLineSegment(sketch, "E16.9.0.20", {"start": v(22.6, 585.47) * mm, "end": v(1.85, 598.93) * mm});
            skLineSegment(sketch, "E16.12.0.20", {"start": v(71.7, 598.93) * mm, "end": v(50.96, 585.47) * mm});
            skLineSegment(sketch, "E16.15.0.20", {"start": v(19.33, 583.98) * mm, "end": v(-1.41, 597.45) * mm});
            skLineSegment(sketch, "E16.18.0.20", {"start": v(50.96, 585.47) * mm, "end": v(22.6, 585.47) * mm});
            skLineSegment(sketch, "E16.21.0.20", {"start": v(-1.41, 597.45) * mm, "end": v(-29.78, 597.45) * mm});
            skLineSegment(sketch, "E16.24.0.20", {"start": v(-29.78, 597.45) * mm, "end": v(-50.52, 583.98) * mm});
            skLineSegment(sketch, "E16.27.0.20", {"start": v(-50.52, 583.98) * mm, "end": v(-29.78, 570.52) * mm});
            skLineSegment(sketch, "E16.30.0.20", {"start": v(-29.78, 570.52) * mm, "end": v(-1.41, 570.52) * mm});
            skLineSegment(sketch, "E16.33.0.20", {"start": v(-1.41, 570.52) * mm, "end": v(19.33, 583.98) * mm});
            skLineSegment(sketch, "E16.0.0.21", {"start": v(1.85, 628.88) * mm, "end": v(22.6, 642.34) * mm});
            skLineSegment(sketch, "E16.3.0.21", {"start": v(22.6, 642.34) * mm, "end": v(50.96, 642.34) * mm});
            skLineSegment(sketch, "E16.6.0.21", {"start": v(50.96, 642.34) * mm, "end": v(71.7, 628.88) * mm});
            skLineSegment(sketch, "E16.9.0.21", {"start": v(22.6, 615.42) * mm, "end": v(1.85, 628.88) * mm});
            skLineSegment(sketch, "E16.12.0.21", {"start": v(71.7, 628.88) * mm, "end": v(50.96, 615.42) * mm});
            skLineSegment(sketch, "E16.15.0.21", {"start": v(19.33, 613.93) * mm, "end": v(-1.41, 627.4) * mm});
            skLineSegment(sketch, "E16.18.0.21", {"start": v(50.96, 615.42) * mm, "end": v(22.6, 615.42) * mm});
            skLineSegment(sketch, "E16.21.0.21", {"start": v(-1.41, 627.4) * mm, "end": v(-29.78, 627.4) * mm});
            skLineSegment(sketch, "E16.24.0.21", {"start": v(-29.78, 627.4) * mm, "end": v(-50.52, 613.93) * mm});
            skLineSegment(sketch, "E16.27.0.21", {"start": v(-50.52, 613.93) * mm, "end": v(-29.78, 600.47) * mm});
            skLineSegment(sketch, "E16.30.0.21", {"start": v(-29.78, 600.47) * mm, "end": v(-1.41, 600.47) * mm});
            skLineSegment(sketch, "E16.33.0.21", {"start": v(-1.41, 600.47) * mm, "end": v(19.33, 613.93) * mm});
            skLineSegment(sketch, "E16.0.0.22", {"start": v(1.85, 658.83) * mm, "end": v(22.6, 672.29) * mm});
            skLineSegment(sketch, "E16.3.0.22", {"start": v(22.6, 672.29) * mm, "end": v(50.96, 672.29) * mm});
            skLineSegment(sketch, "E16.6.0.22", {"start": v(50.96, 672.29) * mm, "end": v(71.7, 658.83) * mm});
            skLineSegment(sketch, "E16.9.0.22", {"start": v(22.6, 645.36) * mm, "end": v(1.85, 658.83) * mm});
            skLineSegment(sketch, "E16.12.0.22", {"start": v(71.7, 658.83) * mm, "end": v(50.96, 645.36) * mm});
            skLineSegment(sketch, "E16.15.0.22", {"start": v(19.33, 643.88) * mm, "end": v(-1.41, 657.34) * mm});
            skLineSegment(sketch, "E16.18.0.22", {"start": v(50.96, 645.36) * mm, "end": v(22.6, 645.36) * mm});
            skLineSegment(sketch, "E16.21.0.22", {"start": v(-1.41, 657.34) * mm, "end": v(-29.78, 657.34) * mm});
            skLineSegment(sketch, "E16.24.0.22", {"start": v(-29.78, 657.34) * mm, "end": v(-50.52, 643.88) * mm});
            skLineSegment(sketch, "E16.27.0.22", {"start": v(-50.52, 643.88) * mm, "end": v(-29.78, 630.42) * mm});
            skLineSegment(sketch, "E16.30.0.22", {"start": v(-29.78, 630.42) * mm, "end": v(-1.41, 630.42) * mm});
            skLineSegment(sketch, "E16.33.0.22", {"start": v(-1.41, 630.42) * mm, "end": v(19.33, 643.88) * mm});
            skLineSegment(sketch, "E16.0.1.20", {"start": v(105.98, 598.53) * mm, "end": v(126.72, 612) * mm});
            skLineSegment(sketch, "E16.3.1.20", {"start": v(126.72, 612) * mm, "end": v(155.1, 612) * mm});
            skLineSegment(sketch, "E16.6.1.20", {"start": v(155.1, 612) * mm, "end": v(175.83, 598.53) * mm});
            skLineSegment(sketch, "E16.9.1.20", {"start": v(126.72, 585.07) * mm, "end": v(105.98, 598.53) * mm});
            skLineSegment(sketch, "E16.12.1.20", {"start": v(175.83, 598.53) * mm, "end": v(155.1, 585.07) * mm});
            skLineSegment(sketch, "E16.15.1.20", {"start": v(123.46, 583.58) * mm, "end": v(102.72, 597.04) * mm});
            skLineSegment(sketch, "E16.18.1.20", {"start": v(155.1, 585.07) * mm, "end": v(126.72, 585.07) * mm});
            skLineSegment(sketch, "E16.21.1.20", {"start": v(102.72, 597.04) * mm, "end": v(74.34, 597.04) * mm});
            skLineSegment(sketch, "E16.24.1.20", {"start": v(74.34, 597.04) * mm, "end": v(53.6, 583.58) * mm});
            skLineSegment(sketch, "E16.27.1.20", {"start": v(53.6, 583.58) * mm, "end": v(74.34, 570.12) * mm});
            skLineSegment(sketch, "E16.30.1.20", {"start": v(74.34, 570.12) * mm, "end": v(102.72, 570.12) * mm});
            skLineSegment(sketch, "E16.33.1.20", {"start": v(102.72, 570.12) * mm, "end": v(123.46, 583.58) * mm});
            skLineSegment(sketch, "E16.0.1.21", {"start": v(105.98, 628.48) * mm, "end": v(126.72, 641.94) * mm});
            skLineSegment(sketch, "E16.3.1.21", {"start": v(126.72, 641.94) * mm, "end": v(155.1, 641.94) * mm});
            skLineSegment(sketch, "E16.6.1.21", {"start": v(155.1, 641.94) * mm, "end": v(175.83, 628.48) * mm});
            skLineSegment(sketch, "E16.9.1.21", {"start": v(126.72, 615.01) * mm, "end": v(105.98, 628.48) * mm});
            skLineSegment(sketch, "E16.12.1.21", {"start": v(175.83, 628.48) * mm, "end": v(155.1, 615.01) * mm});
            skLineSegment(sketch, "E16.15.1.21", {"start": v(123.46, 613.53) * mm, "end": v(102.72, 626.99) * mm});
            skLineSegment(sketch, "E16.18.1.21", {"start": v(155.1, 615.01) * mm, "end": v(126.72, 615.01) * mm});
            skLineSegment(sketch, "E16.21.1.21", {"start": v(102.72, 626.99) * mm, "end": v(74.34, 626.99) * mm});
            skLineSegment(sketch, "E16.24.1.21", {"start": v(74.34, 626.99) * mm, "end": v(53.6, 613.53) * mm});
            skLineSegment(sketch, "E16.27.1.21", {"start": v(53.6, 613.53) * mm, "end": v(74.34, 600.07) * mm});
            skLineSegment(sketch, "E16.30.1.21", {"start": v(74.34, 600.07) * mm, "end": v(102.72, 600.07) * mm});
            skLineSegment(sketch, "E16.33.1.21", {"start": v(102.72, 600.07) * mm, "end": v(123.46, 613.53) * mm});
            skLineSegment(sketch, "E16.0.1.22", {"start": v(105.98, 658.42) * mm, "end": v(126.72, 671.88) * mm});
            skLineSegment(sketch, "E16.3.1.22", {"start": v(126.72, 671.88) * mm, "end": v(155.1, 671.88) * mm});
            skLineSegment(sketch, "E16.6.1.22", {"start": v(155.1, 671.88) * mm, "end": v(175.83, 658.42) * mm});
            skLineSegment(sketch, "E16.9.1.22", {"start": v(126.72, 644.96) * mm, "end": v(105.98, 658.42) * mm});
            skLineSegment(sketch, "E16.12.1.22", {"start": v(175.83, 658.42) * mm, "end": v(155.1, 644.96) * mm});
            skLineSegment(sketch, "E16.15.1.22", {"start": v(123.46, 643.47) * mm, "end": v(102.72, 656.94) * mm});
            skLineSegment(sketch, "E16.18.1.22", {"start": v(155.1, 644.96) * mm, "end": v(126.72, 644.96) * mm});
            skLineSegment(sketch, "E16.21.1.22", {"start": v(102.72, 656.94) * mm, "end": v(74.34, 656.94) * mm});
            skLineSegment(sketch, "E16.24.1.22", {"start": v(74.34, 656.94) * mm, "end": v(53.6, 643.47) * mm});
            skLineSegment(sketch, "E16.27.1.22", {"start": v(53.6, 643.47) * mm, "end": v(74.34, 630.01) * mm});
            skLineSegment(sketch, "E16.30.1.22", {"start": v(74.34, 630.01) * mm, "end": v(102.72, 630.01) * mm});
            skLineSegment(sketch, "E16.33.1.22", {"start": v(102.72, 630.01) * mm, "end": v(123.46, 643.47) * mm});
            skLineSegment(sketch, "E16.0.2.20", {"start": v(210.1, 598.13) * mm, "end": v(230.85, 611.59) * mm});
            skLineSegment(sketch, "E16.3.2.20", {"start": v(230.85, 611.59) * mm, "end": v(259.22, 611.59) * mm});
            skLineSegment(sketch, "E16.6.2.20", {"start": v(259.22, 611.59) * mm, "end": v(279.96, 598.13) * mm});
            skLineSegment(sketch, "E16.9.2.20", {"start": v(230.85, 584.66) * mm, "end": v(210.1, 598.13) * mm});
            skLineSegment(sketch, "E16.12.2.20", {"start": v(279.96, 598.13) * mm, "end": v(259.22, 584.66) * mm});
            skLineSegment(sketch, "E16.15.2.20", {"start": v(227.58, 583.18) * mm, "end": v(206.85, 596.64) * mm});
            skLineSegment(sketch, "E16.18.2.20", {"start": v(259.22, 584.66) * mm, "end": v(230.85, 584.66) * mm});
            skLineSegment(sketch, "E16.21.2.20", {"start": v(206.85, 596.64) * mm, "end": v(178.47, 596.64) * mm});
            skLineSegment(sketch, "E16.24.2.20", {"start": v(178.47, 596.64) * mm, "end": v(157.73, 583.18) * mm});
            skLineSegment(sketch, "E16.27.2.20", {"start": v(157.73, 583.18) * mm, "end": v(178.47, 569.72) * mm});
            skLineSegment(sketch, "E16.30.2.20", {"start": v(178.47, 569.72) * mm, "end": v(206.85, 569.72) * mm});
            skLineSegment(sketch, "E16.33.2.20", {"start": v(206.85, 569.72) * mm, "end": v(227.58, 583.18) * mm});
            skLineSegment(sketch, "E16.0.2.21", {"start": v(210.1, 628.07) * mm, "end": v(230.85, 641.53) * mm});
            skLineSegment(sketch, "E16.3.2.21", {"start": v(230.85, 641.53) * mm, "end": v(259.22, 641.53) * mm});
            skLineSegment(sketch, "E16.6.2.21", {"start": v(259.22, 641.53) * mm, "end": v(279.96, 628.07) * mm});
            skLineSegment(sketch, "E16.9.2.21", {"start": v(230.85, 614.6) * mm, "end": v(210.1, 628.07) * mm});
            skLineSegment(sketch, "E16.12.2.21", {"start": v(279.96, 628.07) * mm, "end": v(259.22, 614.6) * mm});
            skLineSegment(sketch, "E16.15.2.21", {"start": v(227.58, 613.12) * mm, "end": v(206.85, 626.59) * mm});
            skLineSegment(sketch, "E16.18.2.21", {"start": v(259.22, 614.6) * mm, "end": v(230.85, 614.6) * mm});
            skLineSegment(sketch, "E16.21.2.21", {"start": v(206.85, 626.59) * mm, "end": v(178.47, 626.59) * mm});
            skLineSegment(sketch, "E16.24.2.21", {"start": v(178.47, 626.59) * mm, "end": v(157.73, 613.12) * mm});
            skLineSegment(sketch, "E16.27.2.21", {"start": v(157.73, 613.12) * mm, "end": v(178.47, 599.66) * mm});
            skLineSegment(sketch, "E16.30.2.21", {"start": v(178.47, 599.66) * mm, "end": v(206.85, 599.66) * mm});
            skLineSegment(sketch, "E16.33.2.21", {"start": v(206.85, 599.66) * mm, "end": v(227.58, 613.12) * mm});
            skLineSegment(sketch, "E16.0.2.22", {"start": v(210.1, 658.02) * mm, "end": v(230.85, 671.48) * mm});
            skLineSegment(sketch, "E16.3.2.22", {"start": v(230.85, 671.48) * mm, "end": v(259.22, 671.48) * mm});
            skLineSegment(sketch, "E16.6.2.22", {"start": v(259.22, 671.48) * mm, "end": v(279.96, 658.02) * mm});
            skLineSegment(sketch, "E16.9.2.22", {"start": v(230.85, 644.56) * mm, "end": v(210.1, 658.02) * mm});
            skLineSegment(sketch, "E16.12.2.22", {"start": v(279.96, 658.02) * mm, "end": v(259.22, 644.56) * mm});
            skLineSegment(sketch, "E16.15.2.22", {"start": v(227.58, 643.07) * mm, "end": v(206.85, 656.53) * mm});
            skLineSegment(sketch, "E16.18.2.22", {"start": v(259.22, 644.56) * mm, "end": v(230.85, 644.56) * mm});
            skLineSegment(sketch, "E16.21.2.22", {"start": v(206.85, 656.53) * mm, "end": v(178.47, 656.53) * mm});
            skLineSegment(sketch, "E16.24.2.22", {"start": v(178.47, 656.53) * mm, "end": v(157.73, 643.07) * mm});
            skLineSegment(sketch, "E16.27.2.22", {"start": v(157.73, 643.07) * mm, "end": v(178.47, 629.6) * mm});
            skLineSegment(sketch, "E16.30.2.22", {"start": v(178.47, 629.6) * mm, "end": v(206.85, 629.6) * mm});
            skLineSegment(sketch, "E16.33.2.22", {"start": v(206.85, 629.6) * mm, "end": v(227.58, 643.07) * mm});
            skLineSegment(sketch, "E16.0.3.20", {"start": v(314.24, 597.72) * mm, "end": v(334.98, 611.18) * mm});
            skLineSegment(sketch, "E16.3.3.20", {"start": v(334.98, 611.18) * mm, "end": v(363.35, 611.18) * mm});
            skLineSegment(sketch, "E16.6.3.20", {"start": v(363.35, 611.18) * mm, "end": v(384.09, 597.72) * mm});
            skLineSegment(sketch, "E16.9.3.20", {"start": v(334.98, 584.26) * mm, "end": v(314.24, 597.72) * mm});
            skLineSegment(sketch, "E16.12.3.20", {"start": v(384.09, 597.72) * mm, "end": v(363.35, 584.26) * mm});
            skLineSegment(sketch, "E16.15.3.20", {"start": v(331.71, 582.77) * mm, "end": v(310.97, 596.24) * mm});
            skLineSegment(sketch, "E16.18.3.20", {"start": v(363.35, 584.26) * mm, "end": v(334.98, 584.26) * mm});
            skLineSegment(sketch, "E16.21.3.20", {"start": v(310.97, 596.24) * mm, "end": v(282.6, 596.24) * mm});
            skLineSegment(sketch, "E16.24.3.20", {"start": v(282.6, 596.24) * mm, "end": v(261.86, 582.77) * mm});
            skLineSegment(sketch, "E16.27.3.20", {"start": v(261.86, 582.77) * mm, "end": v(282.6, 569.31) * mm});
            skLineSegment(sketch, "E16.30.3.20", {"start": v(282.6, 569.31) * mm, "end": v(310.97, 569.31) * mm});
            skLineSegment(sketch, "E16.33.3.20", {"start": v(310.97, 569.31) * mm, "end": v(331.71, 582.77) * mm});
            skLineSegment(sketch, "E16.0.3.21", {"start": v(314.24, 627.67) * mm, "end": v(334.98, 641.13) * mm});
            skLineSegment(sketch, "E16.3.3.21", {"start": v(334.98, 641.13) * mm, "end": v(363.35, 641.13) * mm});
            skLineSegment(sketch, "E16.6.3.21", {"start": v(363.35, 641.13) * mm, "end": v(384.09, 627.67) * mm});
            skLineSegment(sketch, "E16.9.3.21", {"start": v(334.98, 614.2) * mm, "end": v(314.24, 627.67) * mm});
            skLineSegment(sketch, "E16.12.3.21", {"start": v(384.09, 627.67) * mm, "end": v(363.35, 614.2) * mm});
            skLineSegment(sketch, "E16.15.3.21", {"start": v(331.71, 612.72) * mm, "end": v(310.97, 626.18) * mm});
            skLineSegment(sketch, "E16.18.3.21", {"start": v(363.35, 614.2) * mm, "end": v(334.98, 614.2) * mm});
            skLineSegment(sketch, "E16.21.3.21", {"start": v(310.97, 626.18) * mm, "end": v(282.6, 626.18) * mm});
            skLineSegment(sketch, "E16.24.3.21", {"start": v(282.6, 626.18) * mm, "end": v(261.86, 612.72) * mm});
            skLineSegment(sketch, "E16.27.3.21", {"start": v(261.86, 612.72) * mm, "end": v(282.6, 599.26) * mm});
            skLineSegment(sketch, "E16.30.3.21", {"start": v(282.6, 599.26) * mm, "end": v(310.97, 599.26) * mm});
            skLineSegment(sketch, "E16.33.3.21", {"start": v(310.97, 599.26) * mm, "end": v(331.71, 612.72) * mm});
            skLineSegment(sketch, "E16.0.3.22", {"start": v(314.24, 657.61) * mm, "end": v(334.98, 671.08) * mm});
            skLineSegment(sketch, "E16.3.3.22", {"start": v(334.98, 671.08) * mm, "end": v(363.35, 671.08) * mm});
            skLineSegment(sketch, "E16.6.3.22", {"start": v(363.35, 671.08) * mm, "end": v(384.09, 657.61) * mm});
            skLineSegment(sketch, "E16.9.3.22", {"start": v(334.98, 644.15) * mm, "end": v(314.24, 657.61) * mm});
            skLineSegment(sketch, "E16.12.3.22", {"start": v(384.09, 657.61) * mm, "end": v(363.35, 644.15) * mm});
            skLineSegment(sketch, "E16.15.3.22", {"start": v(331.71, 642.67) * mm, "end": v(310.97, 656.13) * mm});
            skLineSegment(sketch, "E16.18.3.22", {"start": v(363.35, 644.15) * mm, "end": v(334.98, 644.15) * mm});
            skLineSegment(sketch, "E16.21.3.22", {"start": v(310.97, 656.13) * mm, "end": v(282.6, 656.13) * mm});
            skLineSegment(sketch, "E16.24.3.22", {"start": v(282.6, 656.13) * mm, "end": v(261.86, 642.67) * mm});
            skLineSegment(sketch, "E16.27.3.22", {"start": v(261.86, 642.67) * mm, "end": v(282.6, 629.2) * mm});
            skLineSegment(sketch, "E16.30.3.22", {"start": v(282.6, 629.2) * mm, "end": v(310.97, 629.2) * mm});
            skLineSegment(sketch, "E16.33.3.22", {"start": v(310.97, 629.2) * mm, "end": v(331.71, 642.67) * mm});
            skLineSegment(sketch, "E16.0.4.20", {"start": v(418.37, 597.32) * mm, "end": v(439.1, 610.78) * mm});
            skLineSegment(sketch, "E16.3.4.20", {"start": v(439.1, 610.78) * mm, "end": v(467.48, 610.78) * mm});
            skLineSegment(sketch, "E16.6.4.20", {"start": v(467.48, 610.78) * mm, "end": v(488.22, 597.32) * mm});
            skLineSegment(sketch, "E16.9.4.20", {"start": v(439.1, 583.86) * mm, "end": v(418.37, 597.32) * mm});
            skLineSegment(sketch, "E16.12.4.20", {"start": v(488.22, 597.32) * mm, "end": v(467.48, 583.86) * mm});
            skLineSegment(sketch, "E16.15.4.20", {"start": v(435.84, 582.37) * mm, "end": v(415.1, 595.83) * mm});
            skLineSegment(sketch, "E16.18.4.20", {"start": v(467.48, 583.86) * mm, "end": v(439.1, 583.86) * mm});
            skLineSegment(sketch, "E16.21.4.20", {"start": v(415.1, 595.83) * mm, "end": v(386.73, 595.83) * mm});
            skLineSegment(sketch, "E16.24.4.20", {"start": v(386.73, 595.83) * mm, "end": v(366, 582.37) * mm});
            skLineSegment(sketch, "E16.27.4.20", {"start": v(366, 582.37) * mm, "end": v(386.73, 568.9) * mm});
            skLineSegment(sketch, "E16.30.4.20", {"start": v(386.73, 568.9) * mm, "end": v(415.1, 568.9) * mm});
            skLineSegment(sketch, "E16.33.4.20", {"start": v(415.1, 568.9) * mm, "end": v(435.84, 582.37) * mm});
            skLineSegment(sketch, "E16.0.4.21", {"start": v(418.37, 627.26) * mm, "end": v(439.1, 640.73) * mm});
            skLineSegment(sketch, "E16.3.4.21", {"start": v(439.1, 640.73) * mm, "end": v(467.48, 640.73) * mm});
            skLineSegment(sketch, "E16.6.4.21", {"start": v(467.48, 640.73) * mm, "end": v(488.22, 627.26) * mm});
            skLineSegment(sketch, "E16.9.4.21", {"start": v(439.1, 613.8) * mm, "end": v(418.37, 627.26) * mm});
            skLineSegment(sketch, "E16.12.4.21", {"start": v(488.22, 627.26) * mm, "end": v(467.48, 613.8) * mm});
            skLineSegment(sketch, "E16.15.4.21", {"start": v(435.84, 612.32) * mm, "end": v(415.1, 625.78) * mm});
            skLineSegment(sketch, "E16.18.4.21", {"start": v(467.48, 613.8) * mm, "end": v(439.1, 613.8) * mm});
            skLineSegment(sketch, "E16.21.4.21", {"start": v(415.1, 625.78) * mm, "end": v(386.73, 625.78) * mm});
            skLineSegment(sketch, "E16.24.4.21", {"start": v(386.73, 625.78) * mm, "end": v(366, 612.32) * mm});
            skLineSegment(sketch, "E16.27.4.21", {"start": v(366, 612.32) * mm, "end": v(386.73, 598.86) * mm});
            skLineSegment(sketch, "E16.30.4.21", {"start": v(386.73, 598.86) * mm, "end": v(415.1, 598.86) * mm});
            skLineSegment(sketch, "E16.33.4.21", {"start": v(415.1, 598.86) * mm, "end": v(435.84, 612.32) * mm});
            skLineSegment(sketch, "E16.0.4.22", {"start": v(418.37, 657.21) * mm, "end": v(439.1, 670.67) * mm});
            skLineSegment(sketch, "E16.3.4.22", {"start": v(439.1, 670.67) * mm, "end": v(467.48, 670.67) * mm});
            skLineSegment(sketch, "E16.6.4.22", {"start": v(467.48, 670.67) * mm, "end": v(488.22, 657.21) * mm});
            skLineSegment(sketch, "E16.9.4.22", {"start": v(439.1, 643.75) * mm, "end": v(418.37, 657.21) * mm});
            skLineSegment(sketch, "E16.12.4.22", {"start": v(488.22, 657.21) * mm, "end": v(467.48, 643.75) * mm});
            skLineSegment(sketch, "E16.15.4.22", {"start": v(435.84, 642.26) * mm, "end": v(415.1, 655.73) * mm});
            skLineSegment(sketch, "E16.18.4.22", {"start": v(467.48, 643.75) * mm, "end": v(439.1, 643.75) * mm});
            skLineSegment(sketch, "E16.21.4.22", {"start": v(415.1, 655.73) * mm, "end": v(386.73, 655.73) * mm});
            skLineSegment(sketch, "E16.24.4.22", {"start": v(386.73, 655.73) * mm, "end": v(366, 642.26) * mm});
            skLineSegment(sketch, "E16.27.4.22", {"start": v(366, 642.26) * mm, "end": v(386.73, 628.8) * mm});
            skLineSegment(sketch, "E16.30.4.22", {"start": v(386.73, 628.8) * mm, "end": v(415.1, 628.8) * mm});
            skLineSegment(sketch, "E16.33.4.22", {"start": v(415.1, 628.8) * mm, "end": v(435.84, 642.26) * mm});
            skLineSegment(sketch, "E16.0.5.20", {"start": v(522.5, 596.91) * mm, "end": v(543.23, 610.38) * mm});
            skLineSegment(sketch, "E16.3.5.20", {"start": v(543.23, 610.38) * mm, "end": v(571.6, 610.38) * mm});
            skLineSegment(sketch, "E16.6.5.20", {"start": v(571.6, 610.38) * mm, "end": v(592.34, 596.91) * mm});
            skLineSegment(sketch, "E16.9.5.20", {"start": v(543.23, 583.45) * mm, "end": v(522.5, 596.91) * mm});
            skLineSegment(sketch, "E16.12.5.20", {"start": v(592.34, 596.91) * mm, "end": v(571.6, 583.45) * mm});
            skLineSegment(sketch, "E16.15.5.20", {"start": v(539.97, 581.97) * mm, "end": v(519.23, 595.43) * mm});
            skLineSegment(sketch, "E16.18.5.20", {"start": v(571.6, 583.45) * mm, "end": v(543.23, 583.45) * mm});
            skLineSegment(sketch, "E16.21.5.20", {"start": v(519.23, 595.43) * mm, "end": v(490.86, 595.43) * mm});
            skLineSegment(sketch, "E16.24.5.20", {"start": v(490.86, 595.43) * mm, "end": v(470.12, 581.97) * mm});
            skLineSegment(sketch, "E16.27.5.20", {"start": v(470.12, 581.97) * mm, "end": v(490.86, 568.5) * mm});
            skLineSegment(sketch, "E16.30.5.20", {"start": v(490.86, 568.5) * mm, "end": v(519.23, 568.5) * mm});
            skLineSegment(sketch, "E16.33.5.20", {"start": v(519.23, 568.5) * mm, "end": v(539.97, 581.97) * mm});
            skLineSegment(sketch, "E16.0.5.21", {"start": v(522.5, 626.86) * mm, "end": v(543.23, 640.32) * mm});
            skLineSegment(sketch, "E16.3.5.21", {"start": v(543.23, 640.32) * mm, "end": v(571.6, 640.32) * mm});
            skLineSegment(sketch, "E16.6.5.21", {"start": v(571.6, 640.32) * mm, "end": v(592.34, 626.86) * mm});
            skLineSegment(sketch, "E16.9.5.21", {"start": v(543.23, 613.4) * mm, "end": v(522.5, 626.86) * mm});
            skLineSegment(sketch, "E16.12.5.21", {"start": v(592.34, 626.86) * mm, "end": v(571.6, 613.4) * mm});
            skLineSegment(sketch, "E16.15.5.21", {"start": v(539.97, 611.91) * mm, "end": v(519.23, 625.38) * mm});
            skLineSegment(sketch, "E16.18.5.21", {"start": v(571.6, 613.4) * mm, "end": v(543.23, 613.4) * mm});
            skLineSegment(sketch, "E16.21.5.21", {"start": v(519.23, 625.38) * mm, "end": v(490.86, 625.38) * mm});
            skLineSegment(sketch, "E16.24.5.21", {"start": v(490.86, 625.38) * mm, "end": v(470.12, 611.91) * mm});
            skLineSegment(sketch, "E16.27.5.21", {"start": v(470.12, 611.91) * mm, "end": v(490.86, 598.45) * mm});
            skLineSegment(sketch, "E16.30.5.21", {"start": v(490.86, 598.45) * mm, "end": v(519.23, 598.45) * mm});
            skLineSegment(sketch, "E16.33.5.21", {"start": v(519.23, 598.45) * mm, "end": v(539.97, 611.91) * mm});
            skLineSegment(sketch, "E16.0.5.22", {"start": v(522.5, 656.8) * mm, "end": v(543.23, 670.27) * mm});
            skLineSegment(sketch, "E16.3.5.22", {"start": v(543.23, 670.27) * mm, "end": v(571.6, 670.27) * mm});
            skLineSegment(sketch, "E16.6.5.22", {"start": v(571.6, 670.27) * mm, "end": v(592.34, 656.8) * mm});
            skLineSegment(sketch, "E16.9.5.22", {"start": v(543.23, 643.35) * mm, "end": v(522.5, 656.8) * mm});
            skLineSegment(sketch, "E16.12.5.22", {"start": v(592.34, 656.8) * mm, "end": v(571.6, 643.35) * mm});
            skLineSegment(sketch, "E16.15.5.22", {"start": v(539.97, 641.86) * mm, "end": v(519.23, 655.32) * mm});
            skLineSegment(sketch, "E16.18.5.22", {"start": v(571.6, 643.35) * mm, "end": v(543.23, 643.35) * mm});
            skLineSegment(sketch, "E16.21.5.22", {"start": v(519.23, 655.32) * mm, "end": v(490.86, 655.32) * mm});
            skLineSegment(sketch, "E16.24.5.22", {"start": v(490.86, 655.32) * mm, "end": v(470.12, 641.86) * mm});
            skLineSegment(sketch, "E16.27.5.22", {"start": v(470.12, 641.86) * mm, "end": v(490.86, 628.4) * mm});
            skLineSegment(sketch, "E16.30.5.22", {"start": v(490.86, 628.4) * mm, "end": v(519.23, 628.4) * mm});
            skLineSegment(sketch, "E16.33.5.22", {"start": v(519.23, 628.4) * mm, "end": v(539.97, 641.86) * mm});
            skLineSegment(sketch, "E16.0.6.20", {"start": v(626.62, 596.51) * mm, "end": v(647.36, 609.97) * mm});
            skLineSegment(sketch, "E16.3.6.20", {"start": v(647.36, 609.97) * mm, "end": v(675.73, 609.97) * mm});
            skLineSegment(sketch, "E16.6.6.20", {"start": v(675.73, 609.97) * mm, "end": v(696.47, 596.51) * mm});
            skLineSegment(sketch, "E16.9.6.20", {"start": v(647.36, 583.05) * mm, "end": v(626.62, 596.51) * mm});
            skLineSegment(sketch, "E16.12.6.20", {"start": v(696.47, 596.51) * mm, "end": v(675.73, 583.05) * mm});
            skLineSegment(sketch, "E16.15.6.20", {"start": v(644.1, 581.56) * mm, "end": v(623.36, 595.03) * mm});
            skLineSegment(sketch, "E16.18.6.20", {"start": v(675.73, 583.05) * mm, "end": v(647.36, 583.05) * mm});
            skLineSegment(sketch, "E16.21.6.20", {"start": v(623.36, 595.03) * mm, "end": v(594.99, 595.03) * mm});
            skLineSegment(sketch, "E16.24.6.20", {"start": v(594.99, 595.03) * mm, "end": v(574.25, 581.56) * mm});
            skLineSegment(sketch, "E16.27.6.20", {"start": v(574.25, 581.56) * mm, "end": v(594.99, 568.1) * mm});
            skLineSegment(sketch, "E16.30.6.20", {"start": v(594.99, 568.1) * mm, "end": v(623.36, 568.1) * mm});
            skLineSegment(sketch, "E16.33.6.20", {"start": v(623.36, 568.1) * mm, "end": v(644.1, 581.56) * mm});
            skLineSegment(sketch, "E16.0.6.21", {"start": v(626.62, 626.46) * mm, "end": v(647.36, 639.92) * mm});
            skLineSegment(sketch, "E16.3.6.21", {"start": v(647.36, 639.92) * mm, "end": v(675.73, 639.92) * mm});
            skLineSegment(sketch, "E16.6.6.21", {"start": v(675.73, 639.92) * mm, "end": v(696.47, 626.46) * mm});
            skLineSegment(sketch, "E16.9.6.21", {"start": v(647.36, 613) * mm, "end": v(626.62, 626.46) * mm});
            skLineSegment(sketch, "E16.12.6.21", {"start": v(696.47, 626.46) * mm, "end": v(675.73, 613) * mm});
            skLineSegment(sketch, "E16.15.6.21", {"start": v(644.1, 611.51) * mm, "end": v(623.36, 624.97) * mm});
            skLineSegment(sketch, "E16.18.6.21", {"start": v(675.73, 613) * mm, "end": v(647.36, 613) * mm});
            skLineSegment(sketch, "E16.21.6.21", {"start": v(623.36, 624.97) * mm, "end": v(594.99, 624.97) * mm});
            skLineSegment(sketch, "E16.24.6.21", {"start": v(594.99, 624.97) * mm, "end": v(574.25, 611.51) * mm});
            skLineSegment(sketch, "E16.27.6.21", {"start": v(574.25, 611.51) * mm, "end": v(594.99, 598.05) * mm});
            skLineSegment(sketch, "E16.30.6.21", {"start": v(594.99, 598.05) * mm, "end": v(623.36, 598.05) * mm});
            skLineSegment(sketch, "E16.33.6.21", {"start": v(623.36, 598.05) * mm, "end": v(644.1, 611.51) * mm});
            skLineSegment(sketch, "E16.0.6.22", {"start": v(626.62, 656.4) * mm, "end": v(647.36, 669.87) * mm});
            skLineSegment(sketch, "E16.3.6.22", {"start": v(647.36, 669.87) * mm, "end": v(675.73, 669.87) * mm});
            skLineSegment(sketch, "E16.6.6.22", {"start": v(675.73, 669.87) * mm, "end": v(696.47, 656.4) * mm});
            skLineSegment(sketch, "E16.9.6.22", {"start": v(647.36, 642.94) * mm, "end": v(626.62, 656.4) * mm});
            skLineSegment(sketch, "E16.12.6.22", {"start": v(696.47, 656.4) * mm, "end": v(675.73, 642.94) * mm});
            skLineSegment(sketch, "E16.15.6.22", {"start": v(644.1, 641.46) * mm, "end": v(623.36, 654.92) * mm});
            skLineSegment(sketch, "E16.18.6.22", {"start": v(675.73, 642.94) * mm, "end": v(647.36, 642.94) * mm});
            skLineSegment(sketch, "E16.21.6.22", {"start": v(623.36, 654.92) * mm, "end": v(594.99, 654.92) * mm});
            skLineSegment(sketch, "E16.24.6.22", {"start": v(594.99, 654.92) * mm, "end": v(574.25, 641.46) * mm});
            skLineSegment(sketch, "E16.27.6.22", {"start": v(574.25, 641.46) * mm, "end": v(594.99, 628) * mm});
            skLineSegment(sketch, "E16.30.6.22", {"start": v(594.99, 628) * mm, "end": v(623.36, 628) * mm});
            skLineSegment(sketch, "E16.33.6.22", {"start": v(623.36, 628) * mm, "end": v(644.1, 641.46) * mm});
            skSolve(sketch);
        }
        {
            var Q0;
            Q0=qCreatedBy(makeId("Top.planeOp"),FACE);
            var sketch = newSketch(context, id + "F1", { "sketchPlane" : qUnion([Q0])});
            skLineSegment(sketch, "E17.bottom", {"start": v(0, 0) * mm, "end": v(609.6, 0) * mm});
            skLineSegment(sketch, "E17.top", {"start": v(0, 609.6) * mm, "end": v(609.6, 609.6) * mm});
            skLineSegment(sketch, "E17.left", {"start": v(0, 0) * mm, "end": v(0, 609.6) * mm});
            skLineSegment(sketch, "E17.right", {"start": v(609.6, 0) * mm, "end": v(609.6, 609.6) * mm});
            skSolve(sketch);
        }
        {
            var Q0;
            Q0 = qSketchRegion(id + "F1", true);
            extrude(context, id + "F2", {"entities" : qUnion([Q0]), "depth" : 1.22 * mm});
        }
        {
            var Q0;
            Q0 = qSketchRegion(id + "F0", true);
            var Q1;
            Q1=makeQuery(id+"F2.opExtrude","CAP_FACE",FACE,{"disambiguationData":[OSD([sQuery(id+"F1.wireOp",EDGE,"E17.bottom"),sQuery(id+"F1.wireOp",EDGE,"E17.top"),sQuery(id+"F1.wireOp",EDGE,"E17.left"),sQuery(id+"F1.wireOp",EDGE,"E17.right")])],"isStart":false});
            extrude(context, id + "F3", {"entities" : qUnion([Q0]), "operationType" : NewBodyOperationType.REMOVE, "endBound" : BoundingType.UP_TO_SURFACE, "endBoundEntityFace" : qUnion([Q1]), "depth" : 25.4 * mm});
        }
    });
